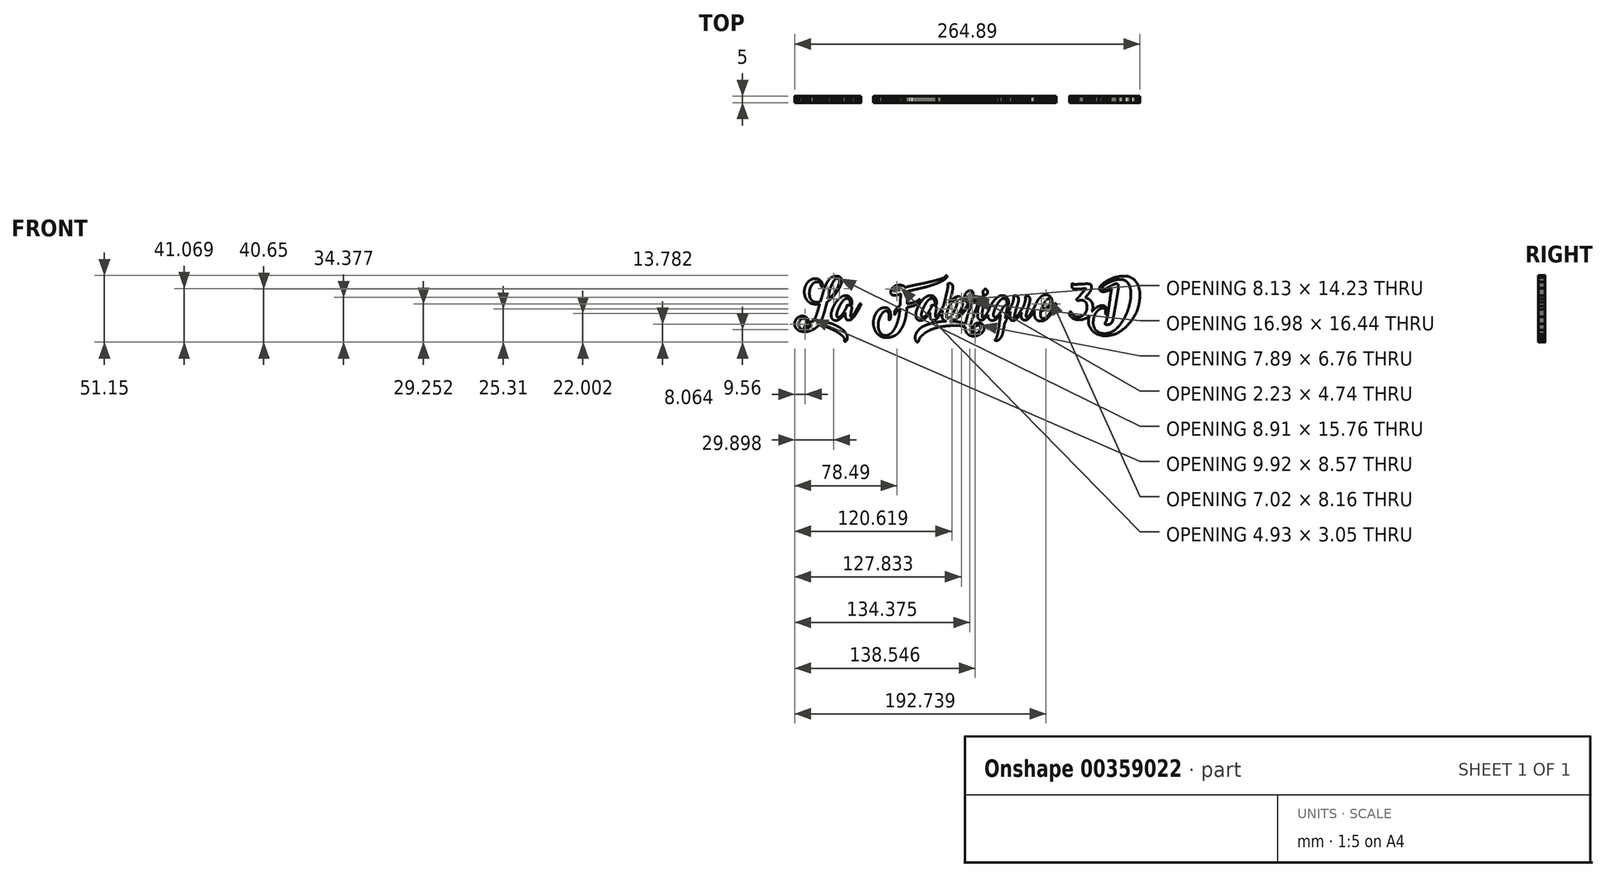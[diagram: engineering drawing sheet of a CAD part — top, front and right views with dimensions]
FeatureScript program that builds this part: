
annotation { "Feature Type Name" : "Feature", "Feature Type Description" : "" }
export const myFeature = defineFeature(function(context is Context, id is Id, definition is map)
    precondition{}
    {
        {
            var Q0;
            Q0=qCreatedBy(makeId("Front.planeOp"),FACE);
            var sketch = newSketch(context, id + "F0", { "sketchPlane" : qUnion([Q0])});
            skLineSegment(sketch, "E0", {"start": v(-112.6, 5.58) * mm, "end": v(-111.78, 8.4) * mm});
            skLineSegment(sketch, "E1", {"start": v(-107.62, 5.33) * mm, "end": v(-108.37, 2.37) * mm});
            skLineSegment(sketch, "E2", {"start": v(-126.72, -17.45) * mm, "end": v(-126.72, -17.45) * mm});
            skLineSegment(sketch, "E3", {"start": v(-106.57, 9.68) * mm, "end": v(-107, 7.62) * mm});
            skLineSegment(sketch, "E4", {"start": v(-125.15, -13.95) * mm, "end": v(-125.15, -13.93) * mm});
            skLineSegment(sketch, "E5", {"start": v(-81.47, 3.42) * mm, "end": v(-81.73, 2.87) * mm});
            skLineSegment(sketch, "E6", {"start": v(-88.86, 2.94) * mm, "end": v(-88.89, 2.92) * mm});
            skLineSegment(sketch, "E7", {"start": v(-19.52, 23.18) * mm, "end": v(-19.54, 23.18) * mm});
            skLineSegment(sketch, "E8", {"start": v(-16.3, 25.55) * mm, "end": v(-16.34, 25.55) * mm});
            skLineSegment(sketch, "E9", {"start": v(-40.07, 14.74) * mm, "end": v(-41.35, 14.43) * mm});
            skLineSegment(sketch, "E10", {"start": v(-45.54, 3.9) * mm, "end": v(-45.56, 3.9) * mm});
            skLineSegment(sketch, "E11", {"start": v(-44.8, 1.44) * mm, "end": v(-45.54, 1.31) * mm});
            skLineSegment(sketch, "E12", {"start": v(-46.28, 1.16) * mm, "end": v(-46.28, 0.6) * mm});
            skLineSegment(sketch, "E13", {"start": v(-46.3, 0.48) * mm, "end": v(-46.3, 0.38) * mm});
            skLineSegment(sketch, "E14", {"start": v(-46.3, 0.38) * mm, "end": v(-46.28, 0.38) * mm});
            skLineSegment(sketch, "E15", {"start": v(-61.75, -22.15) * mm, "end": v(-62.86, -22.15) * mm});
            skLineSegment(sketch, "E16", {"start": v(-58.98, -7.82) * mm, "end": v(-58.98, -7.8) * mm});
            skLineSegment(sketch, "E17", {"start": v(-60.11, -7.9) * mm, "end": v(-60.11, -6.28) * mm});
            skLineSegment(sketch, "E18", {"start": v(-51.67, -0.47) * mm, "end": v(-51.72, -0.45) * mm});
            skLineSegment(sketch, "E19", {"start": v(-51.72, -0.45) * mm, "end": v(-51.72, -0.45) * mm});
            skLineSegment(sketch, "E20", {"start": v(-53.83, 14.06) * mm, "end": v(-53.39, 14.18) * mm});
            skLineSegment(sketch, "E21", {"start": v(-51.52, 14.94) * mm, "end": v(-51.52, 14.96) * mm});
            skLineSegment(sketch, "E22", {"start": v(-23.91, 2.94) * mm, "end": v(-23.94, 2.92) * mm});
            skLineSegment(sketch, "E23", {"start": v(0.38, 3.72) * mm, "end": v(0.4, 3.75) * mm});
            skLineSegment(sketch, "E24", {"start": v(0.4, 3.75) * mm, "end": v(0.4, 3.75) * mm});
            skLineSegment(sketch, "E25", {"start": v(-14.71, 0.48) * mm, "end": v(-14.69, 0.5) * mm});
            skLineSegment(sketch, "E26", {"start": v(-14.69, 0.5) * mm, "end": v(-14.84, -0.1) * mm});
            skLineSegment(sketch, "E27", {"start": v(-9, 6.84) * mm, "end": v(-9, 6.84) * mm});
            skLineSegment(sketch, "E28", {"start": v(2.1, 4.65) * mm, "end": v(0.36, 1.1) * mm});
            skLineSegment(sketch, "E29", {"start": v(4.87, -20.97) * mm, "end": v(4.87, -20.97) * mm});
            skLineSegment(sketch, "E30", {"start": v(5.62, -17.67) * mm, "end": v(5.6, -17.65) * mm});
            skLineSegment(sketch, "E31", {"start": v(4.7, -18) * mm, "end": v(4.7, -17.97) * mm});
            skLineSegment(sketch, "E32", {"start": v(10.17, 6.56) * mm, "end": v(10.53, 7.72) * mm});
            skLineSegment(sketch, "E33", {"start": v(10.53, 7.72) * mm, "end": v(10.53, 7.7) * mm});
            skLineSegment(sketch, "E34", {"start": v(10.53, 7.7) * mm, "end": v(10.53, 7.7) * mm});
            skLineSegment(sketch, "E35", {"start": v(26.44, -1.03) * mm, "end": v(26.41, -1.03) * mm});
            skLineSegment(sketch, "E36", {"start": v(27.8, 1.46) * mm, "end": v(27.8, 1.44) * mm});
            skLineSegment(sketch, "E37", {"start": v(27.8, 1.44) * mm, "end": v(27.93, 1.71) * mm});
            skLineSegment(sketch, "E38", {"start": v(27.93, 1.71) * mm, "end": v(28.03, 1.71) * mm});
            skLineSegment(sketch, "E39", {"start": v(29.19, -7.29) * mm, "end": v(29.29, -7.04) * mm});
            skLineSegment(sketch, "E40", {"start": v(28.52, -11.59) * mm, "end": v(28.52, -11.56) * mm});
            skLineSegment(sketch, "E41", {"start": v(24, -15.66) * mm, "end": v(24.46, -12.22) * mm});
            skLineSegment(sketch, "E42", {"start": v(43.3, 2.14) * mm, "end": v(43.28, 2.11) * mm});
            skLineSegment(sketch, "E43", {"start": v(41.36, -5.43) * mm, "end": v(41.36, -4.7) * mm});
            skLineSegment(sketch, "E44", {"start": v(35.43, 9.18) * mm, "end": v(35.43, 9.15) * mm});
            skLineSegment(sketch, "E45", {"start": v(38.13, 9.7) * mm, "end": v(38.13, 9.7) * mm});
            skLineSegment(sketch, "E46", {"start": v(51.34, -1.5) * mm, "end": v(51.34, -1.53) * mm});
            skLineSegment(sketch, "E47", {"start": v(64.2, -1.8) * mm, "end": v(64.2, -1.83) * mm});
            skLineSegment(sketch, "E48", {"start": v(68.22, 3.42) * mm, "end": v(67.97, 2.87) * mm});
            skLineSegment(sketch, "E49", {"start": v(79.76, -2.84) * mm, "end": v(79.79, -2.84) * mm});
            skLineSegment(sketch, "E50", {"start": v(115.95, 16.04) * mm, "end": v(115.97, 16.04) * mm});
            skLineSegment(sketch, "E51", {"start": v(111.69, -8.77) * mm, "end": v(111.69, -8.75) * mm});
            skLineSegment(sketch, "E52", {"start": v(106.55, -12.24) * mm, "end": v(106.58, -12.24) * mm});
            skLineSegment(sketch, "E53", {"start": v(109.22, 5.6) * mm, "end": v(109.4, 6.97) * mm});
            skLineSegment(sketch, "E54", {"start": v(107.12, -3.77) * mm, "end": v(107.12, -3.74) * mm});
            skLineSegment(sketch, "E55", {"start": v(109.69, 17.25) * mm, "end": v(110.74, 17.85) * mm});
            skLineSegment(sketch, "E56", {"start": v(115.97, 16.07) * mm, "end": v(115.95, 16.04) * mm});
            skFitSpline(sketch, "E57", {"points": [v(-126.72, -17.45) * mm, v(-127.8, -17.21) * mm, v(-128.7, -16.88) * mm, v(-129.46, -16.47) * mm]});
            skFitSpline(sketch, "E58", {"points": [v(-129.46, -16.47) * mm, v(-130.2, -16.05) * mm, v(-130.8, -15.56) * mm, v(-131.26, -15) * mm]});
            skFitSpline(sketch, "E59", {"points": [v(-131.26, -15) * mm, v(-131.7, -14.47) * mm, v(-132.02, -13.9) * mm, v(-132.2, -13.27) * mm]});
            skFitSpline(sketch, "E60", {"points": [v(-132.2, -13.27) * mm, v(-132.38, -12.65) * mm, v(-132.45, -12.02) * mm, v(-132.41, -11.39) * mm]});
            skFitSpline(sketch, "E61", {"points": [v(-132.41, -11.39) * mm, v(-132.38, -10.7) * mm, v(-132.23, -10.03) * mm, v(-131.98, -9.38) * mm]});
            skFitSpline(sketch, "E62", {"points": [v(-131.98, -9.38) * mm, v(-131.7, -8.72) * mm, v(-131.34, -8.13) * mm, v(-130.9, -7.6) * mm]});
            skFitSpline(sketch, "E63", {"points": [v(-130.9, -7.6) * mm, v(-130.32, -6.95) * mm, v(-129.63, -6.47) * mm, v(-128.85, -6.13) * mm]});
            skFitSpline(sketch, "E64", {"points": [v(-128.85, -6.13) * mm, v(-128.04, -5.78) * mm, v(-127.25, -5.6) * mm, v(-126.48, -5.6) * mm]});
            skFitSpline(sketch, "E65", {"points": [v(-126.48, -5.6) * mm, v(-125.94, -5.6) * mm, v(-125.4, -5.69) * mm, v(-124.9, -5.86) * mm]});
            skFitSpline(sketch, "E66", {"points": [v(-124.9, -5.86) * mm, v(-124.38, -6) * mm, v(-123.93, -6.24) * mm, v(-123.53, -6.56) * mm]});
            skFitSpline(sketch, "E67", {"points": [v(-123.53, -6.56) * mm, v(-123.12, -6.88) * mm, v(-122.79, -7.28) * mm, v(-122.53, -7.77) * mm]});
            skFitSpline(sketch, "E68", {"points": [v(-122.53, -7.77) * mm, v(-122.28, -8.24) * mm, v(-122.12, -8.78) * mm, v(-122.07, -9.4) * mm]});
            skFitSpline(sketch, "E69", {"points": [v(-122.07, -9.4) * mm, v(-122.07, -10.04) * mm, v(-122.2, -10.62) * mm, v(-122.43, -11.16) * mm]});
            skFitSpline(sketch, "E70", {"points": [v(-122.43, -11.16) * mm, v(-121.81, -10.72) * mm, v(-121.13, -10.37) * mm, v(-120.38, -10.1) * mm]});
            skFitSpline(sketch, "E71", {"points": [v(-120.38, -10.1) * mm, v(-119.6, -9.85) * mm, v(-118.76, -9.66) * mm, v(-117.84, -9.53) * mm]});
            skFitSpline(sketch, "E72", {"points": [v(-117.84, -9.53) * mm, v(-117.32, -8.55) * mm, v(-116.85, -7.5) * mm, v(-116.43, -6.38) * mm]});
            skFitSpline(sketch, "E73", {"points": [v(-116.43, -6.38) * mm, v(-115.98, -5.26) * mm, v(-115.58, -4.14) * mm, v(-115.22, -3.01) * mm]});
            skFitSpline(sketch, "E74", {"points": [v(-115.22, -3.01) * mm, v(-114.84, -1.87) * mm, v(-114.5, -0.77) * mm, v(-114.22, 0.3) * mm]});
            skFitSpline(sketch, "E75", {"points": [v(-114.22, 0.3) * mm, v(-113.91, 1.4) * mm, v(-113.64, 2.38) * mm, v(-113.4, 3.27) * mm]});
            skFitSpline(sketch, "E76", {"points": [v(-113.4, 3.27) * mm, v(-113.36, 3.35) * mm, v(-113.34, 3.44) * mm, v(-113.32, 3.52) * mm]});
            skFitSpline(sketch, "E77", {"points": [v(-113.32, 3.52) * mm, v(-113.29, 3.6) * mm, v(-113.26, 3.69) * mm, v(-113.24, 3.77) * mm]});
            skFitSpline(sketch, "E78", {"points": [v(-113.24, 3.77) * mm, v(-113.65, 3.64) * mm, v(-114.06, 3.55) * mm, v(-114.45, 3.5) * mm]});
            skFitSpline(sketch, "E79", {"points": [v(-114.45, 3.5) * mm, v(-114.84, 3.45) * mm, v(-115.25, 3.42) * mm, v(-115.66, 3.42) * mm]});
            skFitSpline(sketch, "E80", {"points": [v(-115.66, 3.42) * mm, v(-116.12, 3.42) * mm, v(-116.57, 3.45) * mm, v(-117.02, 3.5) * mm]});
            skFitSpline(sketch, "E81", {"points": [v(-117.02, 3.5) * mm, v(-117.46, 3.56) * mm, v(-117.89, 3.64) * mm, v(-118.3, 3.72) * mm]});
            skFitSpline(sketch, "E82", {"points": [v(-118.3, 3.72) * mm, v(-119.51, 4) * mm, v(-120.56, 4.45) * mm, v(-121.43, 5.1) * mm]});
            skFitSpline(sketch, "E83", {"points": [v(-121.43, 5.1) * mm, v(-122.28, 5.78) * mm, v(-122.99, 6.56) * mm, v(-123.53, 7.44) * mm]});
            skFitSpline(sketch, "E84", {"points": [v(-123.53, 7.44) * mm, v(-124.08, 8.33) * mm, v(-124.47, 9.3) * mm, v(-124.71, 10.36) * mm]});
            skFitSpline(sketch, "E85", {"points": [v(-124.71, 10.36) * mm, v(-124.95, 11.42) * mm, v(-125.05, 12.49) * mm, v(-125, 13.58) * mm]});
            skFitSpline(sketch, "E86", {"points": [v(-125, 13.58) * mm, v(-124.94, 14.69) * mm, v(-124.74, 15.77) * mm, v(-124.38, 16.82) * mm]});
            skFitSpline(sketch, "E87", {"points": [v(-124.38, 16.82) * mm, v(-124, 17.88) * mm, v(-123.5, 18.83) * mm, v(-122.87, 19.69) * mm]});
            skFitSpline(sketch, "E88", {"points": [v(-122.87, 19.69) * mm, v(-122.23, 20.56) * mm, v(-121.47, 21.29) * mm, v(-120.58, 21.88) * mm]});
            skFitSpline(sketch, "E89", {"points": [v(-120.58, 21.88) * mm, v(-119.7, 22.46) * mm, v(-118.7, 22.85) * mm, v(-117.58, 23.03) * mm]});
            skFitSpline(sketch, "E90", {"points": [v(-117.58, 23.03) * mm, v(-117.44, 23.07) * mm, v(-117.29, 23.08) * mm, v(-117.12, 23.08) * mm]});
            skFitSpline(sketch, "E91", {"points": [v(-117.12, 23.08) * mm, v(-116.93, 23.1) * mm, v(-116.77, 23.1) * mm, v(-116.63, 23.1) * mm]});
            skFitSpline(sketch, "E92", {"points": [v(-116.63, 23.1) * mm, v(-115.7, 23.1) * mm, v(-114.89, 22.92) * mm, v(-114.17, 22.56) * mm]});
            skFitSpline(sketch, "E93", {"points": [v(-114.17, 22.56) * mm, v(-113.43, 22.2) * mm, v(-112.82, 21.75) * mm, v(-112.35, 21.2) * mm]});
            skFitSpline(sketch, "E94", {"points": [v(-112.35, 21.2) * mm, v(-111.85, 20.64) * mm, v(-111.5, 20.04) * mm, v(-111.27, 19.39) * mm]});
            skFitSpline(sketch, "E95", {"points": [v(-111.27, 19.39) * mm, v(-111.05, 18.73) * mm, v(-110.99, 18.12) * mm, v(-111.09, 17.55) * mm]});
            skFitSpline(sketch, "E96", {"points": [v(-111.09, 17.55) * mm, v(-111.28, 17.15) * mm, v(-111.46, 16.95) * mm, v(-111.63, 16.95) * mm]});
            skFitSpline(sketch, "E97", {"points": [v(-111.63, 16.95) * mm, v(-111.8, 16.97) * mm, v(-111.96, 17.05) * mm, v(-112.11, 17.2) * mm]});
            skFitSpline(sketch, "E98", {"points": [v(-112.11, 17.2) * mm, v(-112.13, 17.79) * mm, v(-112.22, 18.28) * mm, v(-112.37, 18.68) * mm]});
            skFitSpline(sketch, "E99", {"points": [v(-112.37, 18.68) * mm, v(-112.5, 19.09) * mm, v(-112.69, 19.41) * mm, v(-112.91, 19.66) * mm]});
            skFitSpline(sketch, "E100", {"points": [v(-112.91, 19.66) * mm, v(-113.12, 19.93) * mm, v(-113.34, 20.12) * mm, v(-113.58, 20.24) * mm]});
            skFitSpline(sketch, "E101", {"points": [v(-113.58, 20.24) * mm, v(-113.8, 20.38) * mm, v(-114.01, 20.47) * mm, v(-114.22, 20.52) * mm]});
            skFitSpline(sketch, "E102", {"points": [v(-114.22, 20.52) * mm, v(-114.5, 20.57) * mm, v(-114.8, 20.6) * mm, v(-115.1, 20.6) * mm]});
            skFitSpline(sketch, "E103", {"points": [v(-115.1, 20.6) * mm, v(-116, 20.6) * mm, v(-116.82, 20.35) * mm, v(-117.55, 19.87) * mm]});
            skFitSpline(sketch, "E104", {"points": [v(-117.55, 19.87) * mm, v(-118.27, 19.4) * mm, v(-118.89, 18.78) * mm, v(-119.4, 18) * mm]});
            skFitSpline(sketch, "E105", {"points": [v(-119.4, 18) * mm, v(-119.92, 17.25) * mm, v(-120.33, 16.39) * mm, v(-120.63, 15.41) * mm]});
            skFitSpline(sketch, "E106", {"points": [v(-120.63, 15.41) * mm, v(-120.92, 14.44) * mm, v(-121.1, 13.46) * mm, v(-121.15, 12.47) * mm]});
            skFitSpline(sketch, "E107", {"points": [v(-121.15, 12.47) * mm, v(-121.18, 11.82) * mm, v(-121.16, 11.17) * mm, v(-121.1, 10.54) * mm]});
            skFitSpline(sketch, "E108", {"points": [v(-121.1, 10.54) * mm, v(-121.01, 9.9) * mm, v(-120.87, 9.3) * mm, v(-120.69, 8.73) * mm]});
            skFitSpline(sketch, "E109", {"points": [v(-120.69, 8.73) * mm, v(-120.48, 8.16) * mm, v(-120.22, 7.64) * mm, v(-119.92, 7.17) * mm]});
            skFitSpline(sketch, "E110", {"points": [v(-119.92, 7.17) * mm, v(-119.6, 6.7) * mm, v(-119.24, 6.31) * mm, v(-118.81, 6.01) * mm]});
            skFitSpline(sketch, "E111", {"points": [v(-118.81, 6.01) * mm, v(-118.35, 5.68) * mm, v(-117.84, 5.4) * mm, v(-117.27, 5.2) * mm]});
            skFitSpline(sketch, "E112", {"points": [v(-117.27, 5.2) * mm, v(-116.7, 5.02) * mm, v(-116.1, 4.93) * mm, v(-115.48, 4.93) * mm]});
            skFitSpline(sketch, "E113", {"points": [v(-115.48, 4.93) * mm, v(-115.05, 4.93) * mm, v(-114.59, 4.99) * mm, v(-114.1, 5.1) * mm]});
            skFitSpline(sketch, "E114", {"points": [v(-114.1, 5.1) * mm, v(-113.58, 5.24) * mm, v(-113.08, 5.4) * mm, v(-112.6, 5.58) * mm]});
            skFitSpline(sketch, "E115", {"points": [v(-111.78, 8.4) * mm, v(-111.35, 9.98) * mm, v(-110.9, 11.56) * mm, v(-110.42, 13.15) * mm]});
            skFitSpline(sketch, "E116", {"points": [v(-110.42, 13.15) * mm, v(-109.94, 14.74) * mm, v(-109.41, 16.24) * mm, v(-108.83, 17.63) * mm]});
            skFitSpline(sketch, "E117", {"points": [v(-108.83, 17.63) * mm, v(-108.25, 19.04) * mm, v(-107.6, 20.28) * mm, v(-106.88, 21.37) * mm]});
            skFitSpline(sketch, "E118", {"points": [v(-106.88, 21.37) * mm, v(-106.16, 22.46) * mm, v(-105.34, 23.3) * mm, v(-104.42, 23.91) * mm]});
            skFitSpline(sketch, "E119", {"points": [v(-104.42, 23.91) * mm, v(-103.83, 24.25) * mm, v(-103.18, 24.52) * mm, v(-102.47, 24.72) * mm]});
            skFitSpline(sketch, "E120", {"points": [v(-102.47, 24.72) * mm, v(-101.75, 24.94) * mm, v(-101.04, 25.04) * mm, v(-100.34, 25.04) * mm]});
            skFitSpline(sketch, "E121", {"points": [v(-100.34, 25.04) * mm, v(-99.5, 25.04) * mm, v(-98.74, 24.86) * mm, v(-98.05, 24.5) * mm]});
            skFitSpline(sketch, "E122", {"points": [v(-98.05, 24.5) * mm, v(-97.37, 24.12) * mm, v(-96.9, 23.51) * mm, v(-96.67, 22.66) * mm]});
            skFitSpline(sketch, "E123", {"points": [v(-96.67, 22.66) * mm, v(-96.55, 22.19) * mm, v(-96.5, 21.67) * mm, v(-96.51, 21.1) * mm]});
            skFitSpline(sketch, "E124", {"points": [v(-96.51, 21.1) * mm, v(-96.56, 20.28) * mm, v(-96.77, 19.37) * mm, v(-97.13, 18.38) * mm]});
            skFitSpline(sketch, "E125", {"points": [v(-97.13, 18.38) * mm, v(-97.49, 17.4) * mm, v(-97.96, 16.38) * mm, v(-98.54, 15.34) * mm]});
            skFitSpline(sketch, "E126", {"points": [v(-98.54, 15.34) * mm, v(-99.12, 14.3) * mm, v(-99.79, 13.27) * mm, v(-100.54, 12.25) * mm]});
            skFitSpline(sketch, "E127", {"points": [v(-100.54, 12.25) * mm, v(-101.28, 11.22) * mm, v(-102.06, 10.26) * mm, v(-102.88, 9.36) * mm]});
            skFitSpline(sketch, "E128", {"points": [v(-102.88, 9.36) * mm, v(-103.68, 8.47) * mm, v(-104.5, 7.67) * mm, v(-105.31, 6.97) * mm]});
            skFitSpline(sketch, "E129", {"points": [v(-105.31, 6.97) * mm, v(-106.14, 6.26) * mm, v(-106.9, 5.72) * mm, v(-107.62, 5.33) * mm]});
            skFitSpline(sketch, "E130", {"points": [v(-108.37, 2.37) * mm, v(-108.6, 1.48) * mm, v(-108.86, 0.54) * mm, v(-109.11, -0.45) * mm]});
            skFitSpline(sketch, "E131", {"points": [v(-109.11, -0.45) * mm, v(-109.37, -1.44) * mm, v(-109.65, -2.44) * mm, v(-109.96, -3.47) * mm]});
            skFitSpline(sketch, "E132", {"points": [v(-109.96, -3.47) * mm, v(-110.27, -4.47) * mm, v(-110.6, -5.49) * mm, v(-110.99, -6.5) * mm]});
            skFitSpline(sketch, "E133", {"points": [v(-110.99, -6.5) * mm, v(-111.36, -7.53) * mm, v(-111.79, -8.52) * mm, v(-112.27, -9.48) * mm]});
            skFitSpline(sketch, "E134", {"points": [v(-112.27, -9.48) * mm, v(-111.12, -9.56) * mm, v(-110.02, -9.74) * mm, v(-108.96, -10) * mm]});
            skFitSpline(sketch, "E135", {"points": [v(-108.96, -10) * mm, v(-107.88, -10.27) * mm, v(-106.77, -10.58) * mm, v(-105.62, -10.93) * mm]});
            skFitSpline(sketch, "E136", {"points": [v(-105.62, -10.93) * mm, v(-103.8, -11.5) * mm, v(-102.07, -12.2) * mm, v(-100.41, -13.05) * mm]});
            skFitSpline(sketch, "E137", {"points": [v(-100.41, -13.05) * mm, v(-98.75, -13.88) * mm, v(-97.3, -14.8) * mm, v(-96.05, -15.81) * mm]});
            skFitSpline(sketch, "E138", {"points": [v(-96.05, -15.81) * mm, v(-94.79, -16.82) * mm, v(-93.8, -17.9) * mm, v(-93.07, -19.03) * mm]});
            skFitSpline(sketch, "E139", {"points": [v(-93.07, -19.03) * mm, v(-92.34, -20.17) * mm, v(-92, -21.33) * mm, v(-92.07, -22.52) * mm]});
            skFitSpline(sketch, "E140", {"points": [v(-92.07, -22.52) * mm, v(-92.1, -22.68) * mm, v(-92.1, -22.84) * mm, v(-92.13, -23) * mm]});
            skFitSpline(sketch, "E141", {"points": [v(-92.13, -23) * mm, v(-92.14, -23.19) * mm, v(-92.17, -23.35) * mm, v(-92.2, -23.48) * mm]});
            skFitSpline(sketch, "E142", {"points": [v(-92.2, -23.48) * mm, v(-92.24, -23.61) * mm, v(-92.31, -23.78) * mm, v(-92.43, -23.98) * mm]});
            skFitSpline(sketch, "E143", {"points": [v(-92.43, -23.98) * mm, v(-92.55, -24.18) * mm, v(-92.7, -24.38) * mm, v(-92.87, -24.56) * mm]});
            skFitSpline(sketch, "E144", {"points": [v(-92.87, -24.56) * mm, v(-93.04, -24.76) * mm, v(-93.22, -24.92) * mm, v(-93.4, -25.04) * mm]});
            skFitSpline(sketch, "E145", {"points": [v(-93.4, -25.04) * mm, v(-93.6, -25.17) * mm, v(-93.76, -25.22) * mm, v(-93.9, -25.2) * mm]});
            skFitSpline(sketch, "E146", {"points": [v(-93.9, -25.2) * mm, v(-94.02, -25.16) * mm, v(-94.1, -25.09) * mm, v(-94.15, -24.99) * mm]});
            skFitSpline(sketch, "E147", {"points": [v(-94.15, -24.99) * mm, v(-94.2, -24.89) * mm, v(-94.24, -24.78) * mm, v(-94.26, -24.66) * mm]});
            skFitSpline(sketch, "E148", {"points": [v(-94.26, -24.66) * mm, v(-94.26, -24.54) * mm, v(-94.25, -24.43) * mm, v(-94.23, -24.31) * mm]});
            skFitSpline(sketch, "E149", {"points": [v(-94.23, -24.31) * mm, v(-94.21, -24.2) * mm, v(-94.19, -24.1) * mm, v(-94.15, -24.03) * mm]});
            skFitSpline(sketch, "E150", {"points": [v(-94.15, -24.03) * mm, v(-94.12, -23.45) * mm, v(-94.29, -22.85) * mm, v(-94.67, -22.25) * mm]});
            skFitSpline(sketch, "E151", {"points": [v(-94.67, -22.25) * mm, v(-95.04, -21.66) * mm, v(-95.56, -21.07) * mm, v(-96.2, -20.46) * mm]});
            skFitSpline(sketch, "E152", {"points": [v(-96.2, -20.46) * mm, v(-96.84, -19.88) * mm, v(-97.58, -19.3) * mm, v(-98.44, -18.73) * mm]});
            skFitSpline(sketch, "E153", {"points": [v(-98.44, -18.73) * mm, v(-99.3, -18.18) * mm, v(-100.18, -17.64) * mm, v(-101.1, -17.12) * mm]});
            skFitSpline(sketch, "E154", {"points": [v(-101.1, -17.12) * mm, v(-102.03, -16.62) * mm, v(-102.96, -16.14) * mm, v(-103.9, -15.69) * mm]});
            skFitSpline(sketch, "E155", {"points": [v(-103.9, -15.69) * mm, v(-104.84, -15.25) * mm, v(-105.73, -14.86) * mm, v(-106.55, -14.5) * mm]});
            skFitSpline(sketch, "E156", {"points": [v(-106.55, -14.5) * mm, v(-107.37, -14.17) * mm, v(-108.1, -13.88) * mm, v(-108.75, -13.65) * mm]});
            skFitSpline(sketch, "E157", {"points": [v(-108.75, -13.65) * mm, v(-109.39, -13.42) * mm, v(-109.87, -13.26) * mm, v(-110.2, -13.17) * mm]});
            skFitSpline(sketch, "E158", {"points": [v(-110.2, -13.17) * mm, v(-110.52, -13.05) * mm, v(-110.8, -12.96) * mm, v(-111.04, -12.9) * mm]});
            skFitSpline(sketch, "E159", {"points": [v(-111.04, -12.9) * mm, v(-111.28, -12.83) * mm, v(-111.5, -12.77) * mm, v(-111.7, -12.72) * mm]});
            skFitSpline(sketch, "E160", {"points": [v(-111.7, -12.72) * mm, v(-111.9, -12.69) * mm, v(-112.1, -12.65) * mm, v(-112.3, -12.62) * mm]});
            skFitSpline(sketch, "E161", {"points": [v(-112.3, -12.62) * mm, v(-112.48, -12.6) * mm, v(-112.69, -12.58) * mm, v(-112.91, -12.54) * mm]});
            skFitSpline(sketch, "E162", {"points": [v(-112.91, -12.54) * mm, v(-113.06, -12.5) * mm, v(-113.23, -12.48) * mm, v(-113.4, -12.47) * mm]});
            skFitSpline(sketch, "E163", {"points": [v(-113.4, -12.47) * mm, v(-113.55, -12.45) * mm, v(-113.73, -12.43) * mm, v(-113.94, -12.4) * mm]});
            skFitSpline(sketch, "E164", {"points": [v(-113.94, -12.4) * mm, v(-114.57, -13.16) * mm, v(-115.3, -13.87) * mm, v(-116.14, -14.5) * mm]});
            skFitSpline(sketch, "E165", {"points": [v(-116.14, -14.5) * mm, v(-116.98, -15.14) * mm, v(-117.88, -15.69) * mm, v(-118.84, -16.14) * mm]});
            skFitSpline(sketch, "E166", {"points": [v(-118.84, -16.14) * mm, v(-119.78, -16.6) * mm, v(-120.75, -16.97) * mm, v(-121.76, -17.22) * mm]});
            skFitSpline(sketch, "E167", {"points": [v(-121.76, -17.22) * mm, v(-122.76, -17.49) * mm, v(-123.74, -17.62) * mm, v(-124.71, -17.62) * mm]});
            skFitSpline(sketch, "E168", {"points": [v(-124.71, -17.62) * mm, v(-125.06, -17.62) * mm, v(-125.4, -17.6) * mm, v(-125.74, -17.57) * mm]});
            skFitSpline(sketch, "E169", {"points": [v(-125.74, -17.57) * mm, v(-126.07, -17.56) * mm, v(-126.4, -17.51) * mm, v(-126.72, -17.45) * mm]});
            skFitSpline(sketch, "E170", {"points": [v(-107, 7.62) * mm, v(-106.5, 7.84) * mm, v(-105.93, 8.2) * mm, v(-105.31, 8.73) * mm]});
            skFitSpline(sketch, "E171", {"points": [v(-105.31, 8.73) * mm, v(-104.68, 9.26) * mm, v(-104.05, 9.9) * mm, v(-103.42, 10.61) * mm]});
            skFitSpline(sketch, "E172", {"points": [v(-103.42, 10.61) * mm, v(-102.77, 11.35) * mm, v(-102.13, 12.15) * mm, v(-101.52, 13.03) * mm]});
            skFitSpline(sketch, "E173", {"points": [v(-101.52, 13.03) * mm, v(-100.9, 13.9) * mm, v(-100.35, 14.79) * mm, v(-99.87, 15.7) * mm]});
            skFitSpline(sketch, "E174", {"points": [v(-99.87, 15.7) * mm, v(-99.38, 16.6) * mm, v(-98.98, 17.48) * mm, v(-98.67, 18.36) * mm]});
            skFitSpline(sketch, "E175", {"points": [v(-98.67, 18.36) * mm, v(-98.34, 19.24) * mm, v(-98.16, 20.07) * mm, v(-98.13, 20.82) * mm]});
            skFitSpline(sketch, "E176", {"points": [v(-98.13, 20.82) * mm, v(-98.1, 21.37) * mm, v(-98.15, 21.85) * mm, v(-98.28, 22.25) * mm]});
            skFitSpline(sketch, "E177", {"points": [v(-98.28, 22.25) * mm, v(-98.42, 22.66) * mm, v(-98.63, 22.95) * mm, v(-98.9, 23.13) * mm]});
            skFitSpline(sketch, "E178", {"points": [v(-98.9, 23.13) * mm, v(-99.16, 23.32) * mm, v(-99.48, 23.38) * mm, v(-99.87, 23.3) * mm]});
            skFitSpline(sketch, "E179", {"points": [v(-99.87, 23.3) * mm, v(-100.25, 23.24) * mm, v(-100.67, 23.02) * mm, v(-101.13, 22.63) * mm]});
            skFitSpline(sketch, "E180", {"points": [v(-101.13, 22.63) * mm, v(-101.97, 21.9) * mm, v(-102.69, 21.01) * mm, v(-103.29, 19.94) * mm]});
            skFitSpline(sketch, "E181", {"points": [v(-103.29, 19.94) * mm, v(-103.87, 18.87) * mm, v(-104.37, 17.73) * mm, v(-104.8, 16.52) * mm]});
            skFitSpline(sketch, "E182", {"points": [v(-104.8, 16.52) * mm, v(-105.23, 15.33) * mm, v(-105.58, 14.13) * mm, v(-105.85, 12.93) * mm]});
            skFitSpline(sketch, "E183", {"points": [v(-105.85, 12.93) * mm, v(-106.13, 11.72) * mm, v(-106.37, 10.64) * mm, v(-106.57, 9.68) * mm]});
            skFitSpline(sketch, "E184", {"points": [v(-125.15, -13.93) * mm, v(-124.94, -13.67) * mm, v(-124.74, -13.4) * mm, v(-124.53, -13.1) * mm]});
            skFitSpline(sketch, "E185", {"points": [v(-124.53, -13.1) * mm, v(-124.33, -12.8) * mm, v(-124.14, -12.48) * mm, v(-123.97, -12.14) * mm]});
            skFitSpline(sketch, "E186", {"points": [v(-123.97, -12.14) * mm, v(-123.8, -11.82) * mm, v(-123.66, -11.5) * mm, v(-123.56, -11.16) * mm]});
            skFitSpline(sketch, "E187", {"points": [v(-123.56, -11.16) * mm, v(-123.44, -10.83) * mm, v(-123.37, -10.5) * mm, v(-123.35, -10.16) * mm]});
            skFitSpline(sketch, "E188", {"points": [v(-123.35, -10.16) * mm, v(-123.34, -9.9) * mm, v(-123.35, -9.64) * mm, v(-123.4, -9.35) * mm]});
            skFitSpline(sketch, "E189", {"points": [v(-123.4, -9.35) * mm, v(-123.56, -8.73) * mm, v(-123.88, -8.27) * mm, v(-124.35, -7.97) * mm]});
            skFitSpline(sketch, "E190", {"points": [v(-124.35, -7.97) * mm, v(-124.82, -7.67) * mm, v(-125.32, -7.52) * mm, v(-125.87, -7.52) * mm]});
            skFitSpline(sketch, "E191", {"points": [v(-125.87, -7.52) * mm, v(-126.3, -7.52) * mm, v(-126.72, -7.6) * mm, v(-127.15, -7.8) * mm]});
            skFitSpline(sketch, "E192", {"points": [v(-127.15, -7.8) * mm, v(-127.56, -7.98) * mm, v(-127.91, -8.24) * mm, v(-128.2, -8.57) * mm]});
            skFitSpline(sketch, "E193", {"points": [v(-128.2, -8.57) * mm, v(-128.55, -8.96) * mm, v(-128.81, -9.4) * mm, v(-129, -9.9) * mm]});
            skFitSpline(sketch, "E194", {"points": [v(-129, -9.9) * mm, v(-129.17, -10.42) * mm, v(-129.27, -10.94) * mm, v(-129.3, -11.46) * mm]});
            skFitSpline(sketch, "E195", {"points": [v(-129.3, -11.46) * mm, v(-129.34, -12.23) * mm, v(-129.22, -12.98) * mm, v(-128.95, -13.7) * mm]});
            skFitSpline(sketch, "E196", {"points": [v(-128.95, -13.7) * mm, v(-128.67, -14.42) * mm, v(-128.21, -14.97) * mm, v(-127.56, -15.36) * mm]});
            skFitSpline(sketch, "E197", {"points": [v(-127.56, -15.36) * mm, v(-127.17, -15.61) * mm, v(-126.78, -15.79) * mm, v(-126.4, -15.89) * mm]});
            skFitSpline(sketch, "E198", {"points": [v(-126.4, -15.89) * mm, v(-126.01, -16) * mm, v(-125.64, -16.06) * mm, v(-125.28, -16.06) * mm]});
            skFitSpline(sketch, "E199", {"points": [v(-125.28, -16.06) * mm, v(-124.7, -16.06) * mm, v(-124.13, -15.95) * mm, v(-123.58, -15.71) * mm]});
            skFitSpline(sketch, "E200", {"points": [v(-123.58, -15.71) * mm, v(-123.04, -15.48) * mm, v(-122.52, -15.17) * mm, v(-122.02, -14.78) * mm]});
            skFitSpline(sketch, "E201", {"points": [v(-122.02, -14.78) * mm, v(-121.52, -14.41) * mm, v(-121.06, -14) * mm, v(-120.63, -13.52) * mm]});
            skFitSpline(sketch, "E202", {"points": [v(-120.63, -13.52) * mm, v(-120.19, -13.07) * mm, v(-119.79, -12.61) * mm, v(-119.43, -12.14) * mm]});
            skFitSpline(sketch, "E203", {"points": [v(-119.43, -12.14) * mm, v(-120.44, -12.24) * mm, v(-121.33, -12.48) * mm, v(-122.1, -12.85) * mm]});
            skFitSpline(sketch, "E204", {"points": [v(-122.1, -12.85) * mm, v(-122.87, -13.21) * mm, v(-123.45, -13.73) * mm, v(-123.84, -14.4) * mm]});
            skFitSpline(sketch, "E205", {"points": [v(-123.84, -14.4) * mm, v(-123.98, -14.52) * mm, v(-124.12, -14.59) * mm, v(-124.28, -14.6) * mm]});
            skFitSpline(sketch, "E206", {"points": [v(-124.28, -14.6) * mm, v(-124.43, -14.64) * mm, v(-124.58, -14.63) * mm, v(-124.71, -14.58) * mm]});
            skFitSpline(sketch, "E207", {"points": [v(-124.71, -14.58) * mm, v(-124.85, -14.55) * mm, v(-124.96, -14.47) * mm, v(-125.05, -14.35) * mm]});
            skFitSpline(sketch, "E208", {"points": [v(-125.05, -14.35) * mm, v(-125.13, -14.25) * mm, v(-125.17, -14.12) * mm, v(-125.15, -13.95) * mm]});
            skFitSpline(sketch, "E209", {"points": [v(-88.89, 2.92) * mm, v(-88.92, 2.87) * mm, v(-89.03, 2.82) * mm, v(-89.2, 2.77) * mm]});
            skFitSpline(sketch, "E210", {"points": [v(-89.2, 2.77) * mm, v(-89.35, 2.72) * mm, v(-89.46, 2.7) * mm, v(-89.53, 2.7) * mm]});
            skFitSpline(sketch, "E211", {"points": [v(-89.53, 2.7) * mm, v(-89.74, 2.7) * mm, v(-89.92, 2.8) * mm, v(-90.07, 3) * mm]});
            skFitSpline(sketch, "E212", {"points": [v(-90.07, 3) * mm, v(-90, 3.18) * mm, v(-89.96, 3.35) * mm, v(-89.94, 3.5) * mm]});
            skFitSpline(sketch, "E213", {"points": [v(-89.94, 3.5) * mm, v(-89.9, 3.66) * mm, v(-89.87, 3.84) * mm, v(-89.84, 4.03) * mm]});
            skFitSpline(sketch, "E214", {"points": [v(-89.84, 4.03) * mm, v(-89.82, 4.44) * mm, v(-89.86, 4.88) * mm, v(-89.94, 5.33) * mm]});
            skFitSpline(sketch, "E215", {"points": [v(-89.94, 5.33) * mm, v(-90, 5.8) * mm, v(-90.15, 6.22) * mm, v(-90.35, 6.59) * mm]});
            skFitSpline(sketch, "E216", {"points": [v(-90.35, 6.59) * mm, v(-90.56, 6.96) * mm, v(-90.82, 7.26) * mm, v(-91.15, 7.5) * mm]});
            skFitSpline(sketch, "E217", {"points": [v(-91.15, 7.5) * mm, v(-91.47, 7.75) * mm, v(-91.87, 7.87) * mm, v(-92.33, 7.87) * mm]});
            skFitSpline(sketch, "E218", {"points": [v(-92.33, 7.87) * mm, v(-92.93, 7.87) * mm, v(-93.53, 7.64) * mm, v(-94.15, 7.17) * mm]});
            skFitSpline(sketch, "E219", {"points": [v(-94.15, 7.17) * mm, v(-94.77, 6.72) * mm, v(-95.36, 6.12) * mm, v(-95.92, 5.38) * mm]});
            skFitSpline(sketch, "E220", {"points": [v(-95.92, 5.38) * mm, v(-96.48, 4.66) * mm, v(-97.02, 3.85) * mm, v(-97.51, 2.94) * mm]});
            skFitSpline(sketch, "E221", {"points": [v(-97.51, 2.94) * mm, v(-98, 2.04) * mm, v(-98.45, 1.13) * mm, v(-98.85, 0.23) * mm]});
            skFitSpline(sketch, "E222", {"points": [v(-98.85, 0.23) * mm, v(-99.22, -0.66) * mm, v(-99.53, -1.5) * mm, v(-99.77, -2.29) * mm]});
            skFitSpline(sketch, "E223", {"points": [v(-99.77, -2.29) * mm, v(-100, -3.07) * mm, v(-100.15, -3.71) * mm, v(-100.18, -4.2) * mm]});
            skFitSpline(sketch, "E224", {"points": [v(-100.18, -4.2) * mm, v(-100.2, -4.43) * mm, v(-100.2, -4.68) * mm, v(-100.2, -4.95) * mm]});
            skFitSpline(sketch, "E225", {"points": [v(-100.2, -4.95) * mm, v(-100.19, -5.22) * mm, v(-100.14, -5.47) * mm, v(-100.05, -5.7) * mm]});
            skFitSpline(sketch, "E226", {"points": [v(-100.05, -5.7) * mm, v(-99.97, -5.92) * mm, v(-99.84, -6.1) * mm, v(-99.67, -6.26) * mm]});
            skFitSpline(sketch, "E227", {"points": [v(-99.67, -6.26) * mm, v(-99.5, -6.4) * mm, v(-99.26, -6.46) * mm, v(-98.95, -6.46) * mm]});
            skFitSpline(sketch, "E228", {"points": [v(-98.95, -6.46) * mm, v(-98.42, -6.46) * mm, v(-97.86, -6.2) * mm, v(-97.28, -5.68) * mm]});
            skFitSpline(sketch, "E229", {"points": [v(-97.28, -5.68) * mm, v(-96.68, -5.14) * mm, v(-96.1, -4.5) * mm, v(-95.56, -3.74) * mm]});
            skFitSpline(sketch, "E230", {"points": [v(-95.56, -3.74) * mm, v(-95, -2.99) * mm, v(-94.47, -2.2) * mm, v(-94, -1.38) * mm]});
            skFitSpline(sketch, "E231", {"points": [v(-94, -1.38) * mm, v(-93.52, -0.54) * mm, v(-93.11, 0.19) * mm, v(-92.79, 0.8) * mm]});
            skFitSpline(sketch, "E232", {"points": [v(-92.79, 0.8) * mm, v(-92.74, 1) * mm, v(-92.66, 1.2) * mm, v(-92.56, 1.46) * mm]});
            skFitSpline(sketch, "E233", {"points": [v(-92.56, 1.46) * mm, v(-92.44, 1.71) * mm, v(-92.4, 1.99) * mm, v(-92.43, 2.3) * mm]});
            skFitSpline(sketch, "E234", {"points": [v(-92.43, 2.3) * mm, v(-92.46, 2.53) * mm, v(-92.37, 2.68) * mm, v(-92.15, 2.74) * mm]});
            skFitSpline(sketch, "E235", {"points": [v(-92.15, 2.74) * mm, v(-91.93, 2.83) * mm, v(-91.69, 2.88) * mm, v(-91.43, 2.9) * mm]});
            skFitSpline(sketch, "E236", {"points": [v(-91.43, 2.9) * mm, v(-90.42, 2.8) * mm, v(-89.72, 2.58) * mm, v(-89.33, 2.19) * mm]});
            skFitSpline(sketch, "E237", {"points": [v(-89.33, 2.19) * mm, v(-88.92, 1.82) * mm, v(-88.68, 1.38) * mm, v(-88.63, 0.86) * mm]});
            skFitSpline(sketch, "E238", {"points": [v(-88.63, 0.86) * mm, v(-88.58, 0.32) * mm, v(-88.64, -0.26) * mm, v(-88.81, -0.88) * mm]});
            skFitSpline(sketch, "E239", {"points": [v(-88.81, -0.88) * mm, v(-88.97, -1.5) * mm, v(-89.09, -2.08) * mm, v(-89.17, -2.61) * mm]});
            skFitSpline(sketch, "E240", {"points": [v(-89.17, -2.61) * mm, v(-89.19, -2.73) * mm, v(-89.22, -2.92) * mm, v(-89.27, -3.2) * mm]});
            skFitSpline(sketch, "E241", {"points": [v(-89.27, -3.2) * mm, v(-89.3, -3.46) * mm, v(-89.34, -3.75) * mm, v(-89.38, -4.07) * mm]});
            skFitSpline(sketch, "E242", {"points": [v(-89.38, -4.07) * mm, v(-89.41, -4.39) * mm, v(-89.44, -4.72) * mm, v(-89.45, -5.05) * mm]});
            skFitSpline(sketch, "E243", {"points": [v(-89.45, -5.05) * mm, v(-89.47, -5.37) * mm, v(-89.46, -5.64) * mm, v(-89.43, -5.86) * mm]});
            skFitSpline(sketch, "E244", {"points": [v(-89.43, -5.86) * mm, v(-89.38, -6.07) * mm, v(-89.3, -6.22) * mm, v(-89.2, -6.28) * mm]});
            skFitSpline(sketch, "E245", {"points": [v(-89.2, -6.28) * mm, v(-89.08, -6.35) * mm, v(-88.9, -6.3) * mm, v(-88.68, -6.1) * mm]});
            skFitSpline(sketch, "E246", {"points": [v(-88.68, -6.1) * mm, v(-88.27, -5.7) * mm, v(-87.84, -5.19) * mm, v(-87.38, -4.55) * mm]});
            skFitSpline(sketch, "E247", {"points": [v(-87.38, -4.55) * mm, v(-86.91, -3.9) * mm, v(-86.46, -3.2) * mm, v(-86.02, -2.49) * mm]});
            skFitSpline(sketch, "E248", {"points": [v(-86.02, -2.49) * mm, v(-85.55, -1.75) * mm, v(-85.12, -1.01) * mm, v(-84.7, -0.27) * mm]});
            skFitSpline(sketch, "E249", {"points": [v(-84.7, -0.27) * mm, v(-84.28, 0.48) * mm, v(-83.9, 1.17) * mm, v(-83.55, 1.79) * mm]});
            skFitSpline(sketch, "E250", {"points": [v(-83.55, 1.79) * mm, v(-83.36, 2.19) * mm, v(-83.18, 2.57) * mm, v(-82.99, 2.92) * mm]});
            skFitSpline(sketch, "E251", {"points": [v(-82.99, 2.92) * mm, v(-82.78, 3.29) * mm, v(-82.61, 3.59) * mm, v(-82.47, 3.82) * mm]});
            skFitSpline(sketch, "E252", {"points": [v(-82.47, 3.82) * mm, v(-82.35, 3.87) * mm, v(-82.23, 3.9) * mm, v(-82.09, 3.9) * mm]});
            skFitSpline(sketch, "E253", {"points": [v(-82.09, 3.9) * mm, v(-81.94, 3.9) * mm, v(-81.82, 3.85) * mm, v(-81.73, 3.75) * mm]});
            skFitSpline(sketch, "E254", {"points": [v(-81.73, 3.75) * mm, v(-81.63, 3.66) * mm, v(-81.54, 3.56) * mm, v(-81.47, 3.42) * mm]});
            skFitSpline(sketch, "E255", {"points": [v(-81.73, 2.87) * mm, v(-81.97, 2.4) * mm, v(-82.25, 1.85) * mm, v(-82.58, 1.23) * mm]});
            skFitSpline(sketch, "E256", {"points": [v(-82.58, 1.23) * mm, v(-82.88, 0.61) * mm, v(-83.23, -0.04) * mm, v(-83.6, -0.73) * mm]});
            skFitSpline(sketch, "E257", {"points": [v(-83.6, -0.73) * mm, v(-83.96, -1.41) * mm, v(-84.36, -2.1) * mm, v(-84.78, -2.81) * mm]});
            skFitSpline(sketch, "E258", {"points": [v(-84.78, -2.81) * mm, v(-85.2, -3.52) * mm, v(-85.61, -4.19) * mm, v(-86.04, -4.82) * mm]});
            skFitSpline(sketch, "E259", {"points": [v(-86.04, -4.82) * mm, v(-86.45, -5.46) * mm, v(-86.88, -6.05) * mm, v(-87.32, -6.58) * mm]});
            skFitSpline(sketch, "E260", {"points": [v(-87.32, -6.58) * mm, v(-87.75, -7.1) * mm, v(-88.16, -7.52) * mm, v(-88.56, -7.84) * mm]});
            skFitSpline(sketch, "E261", {"points": [v(-88.56, -7.84) * mm, v(-88.9, -8.13) * mm, v(-89.3, -8.36) * mm, v(-89.79, -8.55) * mm]});
            skFitSpline(sketch, "E262", {"points": [v(-89.79, -8.55) * mm, v(-90.27, -8.73) * mm, v(-90.74, -8.82) * mm, v(-91.2, -8.82) * mm]});
            skFitSpline(sketch, "E263", {"points": [v(-91.2, -8.82) * mm, v(-91.81, -8.82) * mm, v(-92.3, -8.61) * mm, v(-92.64, -8.2) * mm]});
            skFitSpline(sketch, "E264", {"points": [v(-92.64, -8.2) * mm, v(-92.98, -7.76) * mm, v(-93.23, -7.25) * mm, v(-93.4, -6.66) * mm]});
            skFitSpline(sketch, "E265", {"points": [v(-93.4, -6.66) * mm, v(-93.56, -6.06) * mm, v(-93.65, -5.44) * mm, v(-93.66, -4.8) * mm]});
            skFitSpline(sketch, "E266", {"points": [v(-93.66, -4.8) * mm, v(-93.68, -4.16) * mm, v(-93.65, -3.63) * mm, v(-93.59, -3.22) * mm]});
            skFitSpline(sketch, "E267", {"points": [v(-93.59, -3.22) * mm, v(-93.59, -3.18) * mm, v(-93.59, -3.17) * mm]});
            skFitSpline(sketch, "E268", {"points": [v(-93.59, -3.17) * mm, v(-93.59, -3.15) * mm, v(-93.58, -3.08) * mm, v(-93.56, -2.96) * mm]});
            skFitSpline(sketch, "E269", {"points": [v(-93.56, -2.96) * mm, v(-94.02, -3.72) * mm, v(-94.53, -4.46) * mm, v(-95.1, -5.18) * mm]});
            skFitSpline(sketch, "E270", {"points": [v(-95.1, -5.18) * mm, v(-95.65, -5.88) * mm, v(-96.24, -6.5) * mm, v(-96.87, -7.06) * mm]});
            skFitSpline(sketch, "E271", {"points": [v(-96.87, -7.06) * mm, v(-97.49, -7.62) * mm, v(-98.14, -8.07) * mm, v(-98.82, -8.42) * mm]});
            skFitSpline(sketch, "E272", {"points": [v(-98.82, -8.42) * mm, v(-99.5, -8.76) * mm, v(-100.2, -8.92) * mm, v(-100.92, -8.92) * mm]});
            skFitSpline(sketch, "E273", {"points": [v(-100.92, -8.92) * mm, v(-101.6, -8.92) * mm, v(-102.16, -8.8) * mm, v(-102.62, -8.57) * mm]});
            skFitSpline(sketch, "E274", {"points": [v(-102.62, -8.57) * mm, v(-103.08, -8.34) * mm, v(-103.45, -8.03) * mm, v(-103.72, -7.64) * mm]});
            skFitSpline(sketch, "E275", {"points": [v(-103.72, -7.64) * mm, v(-104, -7.26) * mm, v(-104.2, -6.8) * mm, v(-104.31, -6.28) * mm]});
            skFitSpline(sketch, "E276", {"points": [v(-104.31, -6.28) * mm, v(-104.43, -5.76) * mm, v(-104.5, -5.22) * mm, v(-104.5, -4.65) * mm]});
            skFitSpline(sketch, "E277", {"points": [v(-104.5, -4.65) * mm, v(-104.5, -4.55) * mm, v(-104.5, -4.43) * mm, v(-104.5, -4.3) * mm]});
            skFitSpline(sketch, "E278", {"points": [v(-104.5, -4.3) * mm, v(-104.5, -4.16) * mm, v(-104.48, -4.04) * mm, v(-104.47, -3.92) * mm]});
            skFitSpline(sketch, "E279", {"points": [v(-104.47, -3.92) * mm, v(-104.36, -3.08) * mm, v(-104.14, -2.15) * mm, v(-103.8, -1.13) * mm]});
            skFitSpline(sketch, "E280", {"points": [v(-103.8, -1.13) * mm, v(-103.47, -0.1) * mm, v(-103.05, 0.92) * mm, v(-102.54, 1.96) * mm]});
            skFitSpline(sketch, "E281", {"points": [v(-102.54, 1.96) * mm, v(-102.01, 3.02) * mm, v(-101.4, 4.04) * mm, v(-100.72, 5.03) * mm]});
            skFitSpline(sketch, "E282", {"points": [v(-100.72, 5.03) * mm, v(-100.03, 6.02) * mm, v(-99.3, 6.9) * mm, v(-98.49, 7.65) * mm]});
            skFitSpline(sketch, "E283", {"points": [v(-98.49, 7.65) * mm, v(-97.67, 8.42) * mm, v(-96.8, 9.03) * mm, v(-95.9, 9.48) * mm]});
            skFitSpline(sketch, "E284", {"points": [v(-95.9, 9.48) * mm, v(-94.99, 9.95) * mm, v(-94.05, 10.19) * mm, v(-93.07, 10.19) * mm]});
            skFitSpline(sketch, "E285", {"points": [v(-93.07, 10.19) * mm, v(-92.32, 10.19) * mm, v(-91.65, 10) * mm, v(-91.07, 9.66) * mm]});
            skFitSpline(sketch, "E286", {"points": [v(-91.07, 9.66) * mm, v(-90.49, 9.3) * mm, v(-90, 8.84) * mm, v(-89.6, 8.27) * mm]});
            skFitSpline(sketch, "E287", {"points": [v(-89.6, 8.27) * mm, v(-89.21, 7.72) * mm, v(-88.93, 7.1) * mm, v(-88.76, 6.39) * mm]});
            skFitSpline(sketch, "E288", {"points": [v(-88.76, 6.39) * mm, v(-88.57, 5.7) * mm, v(-88.5, 5) * mm, v(-88.56, 4.3) * mm]});
            skFitSpline(sketch, "E289", {"points": [v(-88.56, 4.3) * mm, v(-88.6, 3.82) * mm, v(-88.7, 3.36) * mm, v(-88.86, 2.94) * mm]});
            skFitSpline(sketch, "E290", {"points": [v(-51.72, -0.45) * mm, v(-52.53, -0.87) * mm, v(-53.25, -1.4) * mm, v(-53.9, -2.03) * mm]});
            skFitSpline(sketch, "E291", {"points": [v(-53.9, -2.03) * mm, v(-54.54, -2.67) * mm, v(-55.03, -3.43) * mm, v(-55.4, -4.32) * mm]});
            skFitSpline(sketch, "E292", {"points": [v(-55.4, -4.32) * mm, v(-55.5, -4.44) * mm, v(-55.63, -4.45) * mm, v(-55.8, -4.35) * mm]});
            skFitSpline(sketch, "E293", {"points": [v(-55.8, -4.35) * mm, v(-55.96, -4.25) * mm, v(-56.05, -4.12) * mm, v(-56.08, -3.97) * mm]});
            skFitSpline(sketch, "E294", {"points": [v(-56.08, -3.97) * mm, v(-55.86, -2.41) * mm, v(-55.34, -1.09) * mm, v(-54.52, 0) * mm]});
            skFitSpline(sketch, "E295", {"points": [v(-54.52, 0) * mm, v(-53.68, 1.1) * mm, v(-52.68, 1.89) * mm, v(-51.52, 2.4) * mm]});
            skFitSpline(sketch, "E296", {"points": [v(-51.52, 2.4) * mm, v(-51.48, 2.81) * mm, v(-51.46, 3.24) * mm, v(-51.46, 3.67) * mm]});
            skFitSpline(sketch, "E297", {"points": [v(-51.46, 3.67) * mm, v(-51.45, 4.1) * mm, v(-51.43, 4.55) * mm, v(-51.41, 5) * mm]});
            skFitSpline(sketch, "E298", {"points": [v(-51.41, 5) * mm, v(-51.41, 5.07) * mm, v(-51.41, 5.16) * mm, v(-51.41, 5.26) * mm]});
            skFitSpline(sketch, "E299", {"points": [v(-51.41, 5.26) * mm, v(-51.4, 5.37) * mm, v(-51.39, 5.47) * mm, v(-51.39, 5.53) * mm]});
            skFitSpline(sketch, "E300", {"points": [v(-51.39, 5.53) * mm, v(-51.37, 5.62) * mm, v(-51.36, 5.7) * mm, v(-51.36, 5.81) * mm]});
            skFitSpline(sketch, "E301", {"points": [v(-51.36, 5.81) * mm, v(-51.36, 5.93) * mm, v(-51.36, 6.03) * mm, v(-51.36, 6.11) * mm]});
            skFitSpline(sketch, "E302", {"points": [v(-51.36, 6.11) * mm, v(-51.36, 6.33) * mm, v(-51.35, 6.54) * mm, v(-51.34, 6.74) * mm]});
            skFitSpline(sketch, "E303", {"points": [v(-51.34, 6.74) * mm, v(-51.32, 6.96) * mm, v(-51.31, 7.18) * mm, v(-51.31, 7.4) * mm]});
            skFitSpline(sketch, "E304", {"points": [v(-51.31, 7.4) * mm, v(-51.26, 8.58) * mm, v(-51.18, 9.95) * mm, v(-51.08, 11.5) * mm]});
            skFitSpline(sketch, "E305", {"points": [v(-51.08, 11.5) * mm, v(-51.35, 11.36) * mm, v(-51.68, 11.22) * mm, v(-52.05, 11.07) * mm]});
            skFitSpline(sketch, "E306", {"points": [v(-52.05, 11.07) * mm, v(-52.43, 10.93) * mm, v(-52.84, 10.8) * mm, v(-53.29, 10.69) * mm]});
            skFitSpline(sketch, "E307", {"points": [v(-53.29, 10.69) * mm, v(-53.71, 10.59) * mm, v(-54.16, 10.5) * mm, v(-54.62, 10.41) * mm]});
            skFitSpline(sketch, "E308", {"points": [v(-54.62, 10.41) * mm, v(-55.08, 10.34) * mm, v(-55.54, 10.31) * mm, v(-55.98, 10.31) * mm]});
            skFitSpline(sketch, "E309", {"points": [v(-55.98, 10.31) * mm, v(-56.61, 10.31) * mm, v(-57.18, 10.44) * mm, v(-57.67, 10.69) * mm]});
            skFitSpline(sketch, "E310", {"points": [v(-57.67, 10.69) * mm, v(-58.17, 10.96) * mm, v(-58.48, 11.38) * mm, v(-58.6, 11.95) * mm]});
            skFitSpline(sketch, "E311", {"points": [v(-58.6, 11.95) * mm, v(-58.67, 12.21) * mm, v(-58.7, 12.5) * mm, v(-58.7, 12.8) * mm]});
            skFitSpline(sketch, "E312", {"points": [v(-58.7, 12.8) * mm, v(-58.7, 13.44) * mm, v(-58.55, 14.05) * mm, v(-58.24, 14.64) * mm]});
            skFitSpline(sketch, "E313", {"points": [v(-58.24, 14.64) * mm, v(-57.91, 15.24) * mm, v(-57.5, 15.78) * mm, v(-57, 16.24) * mm]});
            skFitSpline(sketch, "E314", {"points": [v(-57, 16.24) * mm, v(-56.5, 16.73) * mm, v(-55.93, 17.13) * mm, v(-55.31, 17.45) * mm]});
            skFitSpline(sketch, "E315", {"points": [v(-55.31, 17.45) * mm, v(-54.68, 17.77) * mm, v(-54.05, 17.97) * mm, v(-53.41, 18.05) * mm]});
            skFitSpline(sketch, "E316", {"points": [v(-53.41, 18.05) * mm, v(-53.35, 18.05) * mm, v(-53.27, 18.05) * mm, v(-53.18, 18.05) * mm]});
            skFitSpline(sketch, "E317", {"points": [v(-53.18, 18.05) * mm, v(-53.08, 18.07) * mm, v(-52.99, 18.09) * mm, v(-52.9, 18.1) * mm]});
            skFitSpline(sketch, "E318", {"points": [v(-52.9, 18.1) * mm, v(-52.76, 18.12) * mm, v(-52.63, 18.13) * mm, v(-52.5, 18.13) * mm]});
            skFitSpline(sketch, "E319", {"points": [v(-52.5, 18.13) * mm, v(-52.34, 18.15) * mm, v(-52.2, 18.16) * mm, v(-52.05, 18.16) * mm]});
            skFitSpline(sketch, "E320", {"points": [v(-52.05, 18.16) * mm, v(-51.22, 18.16) * mm, v(-50.41, 18.01) * mm, v(-49.64, 17.73) * mm]});
            skFitSpline(sketch, "E321", {"points": [v(-49.64, 17.73) * mm, v(-48.86, 17.46) * mm, v(-48.15, 17.02) * mm, v(-47.51, 16.42) * mm]});
            skFitSpline(sketch, "E322", {"points": [v(-47.51, 16.42) * mm, v(-45.78, 16.9) * mm, v(-43.97, 17.36) * mm, v(-42.07, 17.78) * mm]});
            skFitSpline(sketch, "E323", {"points": [v(-42.07, 17.78) * mm, v(-40.17, 18.2) * mm, v(-38.25, 18.6) * mm, v(-36.3, 18.99) * mm]});
            skFitSpline(sketch, "E324", {"points": [v(-36.3, 18.99) * mm, v(-34.9, 19.27) * mm, v(-33.46, 19.57) * mm, v(-31.99, 19.9) * mm]});
            skFitSpline(sketch, "E325", {"points": [v(-31.99, 19.9) * mm, v(-30.52, 20.2) * mm, v(-29.06, 20.54) * mm, v(-27.63, 20.87) * mm]});
            skFitSpline(sketch, "E326", {"points": [v(-27.63, 20.87) * mm, v(-26.19, 21.22) * mm, v(-24.79, 21.6) * mm, v(-23.42, 21.98) * mm]});
            skFitSpline(sketch, "E327", {"points": [v(-23.42, 21.98) * mm, v(-22.03, 22.36) * mm, v(-20.73, 22.76) * mm, v(-19.52, 23.18) * mm]});
            skFitSpline(sketch, "E328", {"points": [v(-19.54, 23.18) * mm, v(-19.4, 23.23) * mm, v(-19.2, 23.3) * mm, v(-18.9, 23.41) * mm]});
            skFitSpline(sketch, "E329", {"points": [v(-18.9, 23.41) * mm, v(-18.6, 23.53) * mm, v(-18.29, 23.65) * mm, v(-17.98, 23.79) * mm]});
            skFitSpline(sketch, "E330", {"points": [v(-17.98, 23.79) * mm, v(-17.65, 23.92) * mm, v(-17.36, 24.07) * mm, v(-17.1, 24.24) * mm]});
            skFitSpline(sketch, "E331", {"points": [v(-17.1, 24.24) * mm, v(-16.83, 24.4) * mm, v(-16.66, 24.58) * mm, v(-16.6, 24.77) * mm]});
            skFitSpline(sketch, "E332", {"points": [v(-16.6, 24.77) * mm, v(-16.57, 24.85) * mm, v(-16.56, 24.93) * mm, v(-16.54, 25) * mm]});
            skFitSpline(sketch, "E333", {"points": [v(-16.54, 25) * mm, v(-16.52, 25.06) * mm, v(-16.52, 25.12) * mm, v(-16.52, 25.17) * mm]});
            skFitSpline(sketch, "E334", {"points": [v(-16.52, 25.17) * mm, v(-16.52, 25.25) * mm, v(-16.5, 25.33) * mm, v(-16.49, 25.4) * mm]});
            skFitSpline(sketch, "E335", {"points": [v(-16.49, 25.4) * mm, v(-16.47, 25.46) * mm, v(-16.41, 25.51) * mm, v(-16.3, 25.55) * mm]});
            skFitSpline(sketch, "E336", {"points": [v(-16.34, 25.55) * mm, v(-16.23, 25.58) * mm, v(-16.12, 25.57) * mm, v(-16, 25.52) * mm]});
            skFitSpline(sketch, "E337", {"points": [v(-16, 25.52) * mm, v(-15.88, 25.47) * mm, v(-15.79, 25.38) * mm, v(-15.72, 25.25) * mm]});
            skFitSpline(sketch, "E338", {"points": [v(-15.72, 25.25) * mm, v(-15.55, 24.94) * mm, v(-15.56, 24.62) * mm, v(-15.75, 24.26) * mm]});
            skFitSpline(sketch, "E339", {"points": [v(-15.75, 24.26) * mm, v(-15.92, 23.91) * mm, v(-16.16, 23.57) * mm, v(-16.49, 23.23) * mm]});
            skFitSpline(sketch, "E340", {"points": [v(-16.49, 23.23) * mm, v(-16.81, 22.92) * mm, v(-17.17, 22.63) * mm, v(-17.54, 22.38) * mm]});
            skFitSpline(sketch, "E341", {"points": [v(-17.54, 22.38) * mm, v(-17.9, 22.13) * mm, v(-18.17, 21.94) * mm, v(-18.36, 21.83) * mm]});
            skFitSpline(sketch, "E342", {"points": [v(-18.36, 21.83) * mm, v(-19.8, 20.97) * mm, v(-21.44, 20.2) * mm, v(-23.29, 19.49) * mm]});
            skFitSpline(sketch, "E343", {"points": [v(-23.29, 19.49) * mm, v(-25.14, 18.78) * mm, v(-27.04, 18.14) * mm, v(-29.01, 17.55) * mm]});
            skFitSpline(sketch, "E344", {"points": [v(-29.01, 17.55) * mm, v(-30.96, 16.97) * mm, v(-32.9, 16.44) * mm, v(-34.81, 15.97) * mm]});
            skFitSpline(sketch, "E345", {"points": [v(-34.81, 15.97) * mm, v(-36.73, 15.52) * mm, v(-38.48, 15.1) * mm, v(-40.07, 14.74) * mm]});
            skFitSpline(sketch, "E346", {"points": [v(-41.35, 14.43) * mm, v(-42.28, 14.23) * mm, v(-43.13, 14.04) * mm, v(-43.92, 13.86) * mm]});
            skFitSpline(sketch, "E347", {"points": [v(-43.92, 13.86) * mm, v(-44.7, 13.67) * mm, v(-45.35, 13.48) * mm, v(-45.9, 13.28) * mm]});
            skFitSpline(sketch, "E348", {"points": [v(-45.9, 13.28) * mm, v(-45.9, 13.18) * mm, v(-45.9, 13.08) * mm, v(-45.9, 12.98) * mm]});
            skFitSpline(sketch, "E349", {"points": [v(-45.9, 12.98) * mm, v(-45.88, 12.88) * mm, v(-45.87, 12.74) * mm, v(-45.87, 12.57) * mm]});
            skFitSpline(sketch, "E350", {"points": [v(-45.87, 12.57) * mm, v(-45.85, 12.42) * mm, v(-45.84, 12.23) * mm, v(-45.84, 12) * mm]});
            skFitSpline(sketch, "E351", {"points": [v(-45.84, 12) * mm, v(-45.83, 11.76) * mm, v(-45.82, 11.47) * mm, v(-45.82, 11.12) * mm]});
            skFitSpline(sketch, "E352", {"points": [v(-45.82, 11.12) * mm, v(-45.82, 10.8) * mm, v(-45.82, 10.42) * mm, v(-45.82, 9.98) * mm]});
            skFitSpline(sketch, "E353", {"points": [v(-45.82, 9.98) * mm, v(-45.82, 9.57) * mm, v(-45.83, 9.06) * mm, v(-45.84, 8.48) * mm]});
            skFitSpline(sketch, "E354", {"points": [v(-45.84, 8.48) * mm, v(-45.86, 7.9) * mm, v(-45.89, 7.24) * mm, v(-45.92, 6.46) * mm]});
            skFitSpline(sketch, "E355", {"points": [v(-45.92, 6.46) * mm, v(-45.94, 5.7) * mm, v(-45.98, 4.84) * mm, v(-46.05, 3.85) * mm]});
            skFitSpline(sketch, "E356", {"points": [v(-46.05, 3.85) * mm, v(-46.02, 3.85) * mm, v(-45.96, 3.85) * mm, v(-45.9, 3.85) * mm]});
            skFitSpline(sketch, "E357", {"points": [v(-45.9, 3.85) * mm, v(-45.83, 3.85) * mm, v(-45.77, 3.86) * mm, v(-45.72, 3.87) * mm]});
            skFitSpline(sketch, "E358", {"points": [v(-45.72, 3.87) * mm, v(-45.68, 3.87) * mm, v(-45.65, 3.87) * mm, v(-45.61, 3.87) * mm]});
            skFitSpline(sketch, "E359", {"points": [v(-45.61, 3.87) * mm, v(-45.58, 3.87) * mm, v(-45.55, 3.88) * mm, v(-45.54, 3.9) * mm]});
            skFitSpline(sketch, "E360", {"points": [v(-45.56, 3.9) * mm, v(-44.76, 4.05) * mm, v(-43.95, 4.2) * mm, v(-43.15, 4.38) * mm]});
            skFitSpline(sketch, "E361", {"points": [v(-43.15, 4.38) * mm, v(-42.35, 4.54) * mm, v(-41.58, 4.75) * mm, v(-40.84, 4.98) * mm]});
            skFitSpline(sketch, "E362", {"points": [v(-40.84, 4.98) * mm, v(-40.09, 5.23) * mm, v(-39.4, 5.52) * mm, v(-38.76, 5.84) * mm]});
            skFitSpline(sketch, "E363", {"points": [v(-38.76, 5.84) * mm, v(-38.13, 6.17) * mm, v(-37.6, 6.57) * mm, v(-37.15, 7.04) * mm]});
            skFitSpline(sketch, "E364", {"points": [v(-37.15, 7.04) * mm, v(-37.06, 7.16) * mm, v(-36.98, 7.22) * mm, v(-36.91, 7.22) * mm]});
            skFitSpline(sketch, "E365", {"points": [v(-36.91, 7.22) * mm, v(-36.85, 7.22) * mm, v(-36.79, 7.18) * mm, v(-36.74, 7.1) * mm]});
            skFitSpline(sketch, "E366", {"points": [v(-36.74, 7.1) * mm, v(-36.68, 7.03) * mm, v(-36.64, 6.93) * mm, v(-36.6, 6.82) * mm]});
            skFitSpline(sketch, "E367", {"points": [v(-36.6, 6.82) * mm, v(-36.57, 6.7) * mm, v(-36.55, 6.59) * mm, v(-36.53, 6.49) * mm]});
            skFitSpline(sketch, "E368", {"points": [v(-36.53, 6.49) * mm, v(-36.65, 5.7) * mm, v(-36.97, 5.03) * mm, v(-37.48, 4.48) * mm]});
            skFitSpline(sketch, "E369", {"points": [v(-37.48, 4.48) * mm, v(-38, 3.92) * mm, v(-38.63, 3.46) * mm, v(-39.38, 3.07) * mm]});
            skFitSpline(sketch, "E370", {"points": [v(-39.38, 3.07) * mm, v(-40.13, 2.7) * mm, v(-40.98, 2.38) * mm, v(-41.92, 2.11) * mm]});
            skFitSpline(sketch, "E371", {"points": [v(-41.92, 2.11) * mm, v(-42.86, 1.86) * mm, v(-43.82, 1.64) * mm, v(-44.8, 1.44) * mm]});
            skFitSpline(sketch, "E372", {"points": [v(-45.54, 1.31) * mm, v(-45.64, 1.28) * mm, v(-45.74, 1.24) * mm, v(-45.84, 1.2) * mm]});
            skFitSpline(sketch, "E373", {"points": [v(-45.84, 1.2) * mm, v(-45.95, 1.2) * mm, v(-46.1, 1.18) * mm, v(-46.28, 1.16) * mm]});
            skFitSpline(sketch, "E374", {"points": [v(-46.28, 0.6) * mm, v(-46.28, 0.57) * mm, v(-46.29, 0.55) * mm, v(-46.3, 0.53) * mm]});
            skFitSpline(sketch, "E375", {"points": [v(-46.3, 0.53) * mm, v(-46.3, 0.51) * mm, v(-46.3, 0.5) * mm, v(-46.3, 0.48) * mm]});
            skFitSpline(sketch, "E376", {"points": [v(-46.28, 0.38) * mm, v(-46.45, -1.35) * mm, v(-46.7, -3.15) * mm, v(-47.03, -5.03) * mm]});
            skFitSpline(sketch, "E377", {"points": [v(-47.03, -5.03) * mm, v(-47.35, -6.9) * mm, v(-47.82, -8.74) * mm, v(-48.44, -10.53) * mm]});
            skFitSpline(sketch, "E378", {"points": [v(-48.44, -10.53) * mm, v(-49.05, -12.33) * mm, v(-49.85, -14.03) * mm, v(-50.82, -15.64) * mm]});
            skFitSpline(sketch, "E379", {"points": [v(-50.82, -15.64) * mm, v(-51.78, -17.24) * mm, v(-52.98, -18.64) * mm, v(-54.42, -19.8) * mm]});
            skFitSpline(sketch, "E380", {"points": [v(-54.42, -19.8) * mm, v(-54.91, -20.16) * mm, v(-55.45, -20.48) * mm, v(-56.03, -20.76) * mm]});
            skFitSpline(sketch, "E381", {"points": [v(-56.03, -20.76) * mm, v(-56.61, -21.05) * mm, v(-57.22, -21.3) * mm, v(-57.85, -21.5) * mm]});
            skFitSpline(sketch, "E382", {"points": [v(-57.85, -21.5) * mm, v(-58.49, -21.7) * mm, v(-59.14, -21.85) * mm, v(-59.8, -21.97) * mm]});
            skFitSpline(sketch, "E383", {"points": [v(-59.8, -21.97) * mm, v(-60.47, -22.09) * mm, v(-61.12, -22.15) * mm, v(-61.75, -22.15) * mm]});
            skFitSpline(sketch, "E384", {"points": [v(-62.86, -22.15) * mm, v(-64.3, -21.95) * mm, v(-65.59, -21.51) * mm, v(-66.73, -20.84) * mm]});
            skFitSpline(sketch, "E385", {"points": [v(-66.73, -20.84) * mm, v(-67.86, -20.17) * mm, v(-68.82, -19.32) * mm, v(-69.6, -18.3) * mm]});
            skFitSpline(sketch, "E386", {"points": [v(-69.6, -18.3) * mm, v(-70.4, -17.28) * mm, v(-71, -16.1) * mm, v(-71.4, -14.78) * mm]});
            skFitSpline(sketch, "E387", {"points": [v(-71.4, -14.78) * mm, v(-71.83, -13.46) * mm, v(-72.04, -12.05) * mm, v(-72.04, -10.56) * mm]});
            skFitSpline(sketch, "E388", {"points": [v(-72.04, -10.56) * mm, v(-72.04, -9.37) * mm, v(-71.88, -8.19) * mm, v(-71.56, -7.01) * mm]});
            skFitSpline(sketch, "E389", {"points": [v(-71.56, -7.01) * mm, v(-71.25, -5.84) * mm, v(-70.8, -4.75) * mm, v(-70.22, -3.74) * mm]});
            skFitSpline(sketch, "E390", {"points": [v(-70.22, -3.74) * mm, v(-69.62, -2.74) * mm, v(-68.9, -1.85) * mm, v(-68.04, -1.08) * mm]});
            skFitSpline(sketch, "E391", {"points": [v(-68.04, -1.08) * mm, v(-67.19, -0.3) * mm, v(-66.22, 0.27) * mm, v(-65.14, 0.66) * mm]});
            skFitSpline(sketch, "E392", {"points": [v(-65.14, 0.66) * mm, v(-64.8, 0.77) * mm, v(-64.47, 0.85) * mm, v(-64.14, 0.88) * mm]});
            skFitSpline(sketch, "E393", {"points": [v(-64.14, 0.88) * mm, v(-63.8, 0.93) * mm, v(-63.47, 0.96) * mm, v(-63.17, 0.96) * mm]});
            skFitSpline(sketch, "E394", {"points": [v(-63.17, 0.96) * mm, v(-62.36, 0.96) * mm, v(-61.69, 0.8) * mm, v(-61.14, 0.46) * mm]});
            skFitSpline(sketch, "E395", {"points": [v(-61.14, 0.46) * mm, v(-60.6, 0.14) * mm, v(-60.15, -0.3) * mm, v(-59.8, -0.85) * mm]});
            skFitSpline(sketch, "E396", {"points": [v(-59.8, -0.85) * mm, v(-59.46, -1.4) * mm, v(-59.21, -2.05) * mm, v(-59.06, -2.79) * mm]});
            skFitSpline(sketch, "E397", {"points": [v(-59.06, -2.79) * mm, v(-58.9, -3.5) * mm, v(-58.83, -4.27) * mm, v(-58.83, -5.08) * mm]});
            skFitSpline(sketch, "E398", {"points": [v(-58.83, -5.08) * mm, v(-58.83, -5.66) * mm, v(-58.85, -6.18) * mm, v(-58.88, -6.63) * mm]});
            skFitSpline(sketch, "E399", {"points": [v(-58.88, -6.63) * mm, v(-58.91, -7.09) * mm, v(-58.95, -7.48) * mm, v(-58.98, -7.82) * mm]});
            skFitSpline(sketch, "E400", {"points": [v(-58.98, -7.8) * mm, v(-59.09, -8) * mm, v(-59.2, -8.17) * mm, v(-59.32, -8.27) * mm]});
            skFitSpline(sketch, "E401", {"points": [v(-59.32, -8.27) * mm, v(-59.42, -8.37) * mm, v(-59.52, -8.44) * mm, v(-59.62, -8.47) * mm]});
            skFitSpline(sketch, "E402", {"points": [v(-59.62, -8.47) * mm, v(-59.73, -8.49) * mm, v(-59.82, -8.49) * mm, v(-59.9, -8.47) * mm]});
            skFitSpline(sketch, "E403", {"points": [v(-59.9, -8.47) * mm, v(-60, -8.44) * mm, v(-60.06, -8.4) * mm, v(-60.11, -8.37) * mm]});
            skFitSpline(sketch, "E404", {"points": [v(-60.11, -8.37) * mm, v(-60.13, -8.29) * mm, v(-60.14, -8.21) * mm, v(-60.14, -8.14) * mm]});
            skFitSpline(sketch, "E405", {"points": [v(-60.14, -8.14) * mm, v(-60.12, -8.06) * mm, v(-60.11, -7.98) * mm, v(-60.11, -7.9) * mm]});
            skFitSpline(sketch, "E406", {"points": [v(-60.11, -6.28) * mm, v(-60.11, -6.23) * mm, v(-60.11, -6.18) * mm, v(-60.11, -6.13) * mm]});
            skFitSpline(sketch, "E407", {"points": [v(-60.11, -6.13) * mm, v(-60.1, -6.08) * mm, v(-60.09, -6.02) * mm, v(-60.09, -5.96) * mm]});
            skFitSpline(sketch, "E408", {"points": [v(-60.09, -5.96) * mm, v(-60.09, -5.45) * mm, v(-60.11, -4.95) * mm, v(-60.16, -4.45) * mm]});
            skFitSpline(sketch, "E409", {"points": [v(-60.16, -4.45) * mm, v(-60.2, -3.94) * mm, v(-60.3, -3.5) * mm, v(-60.45, -3.09) * mm]});
            skFitSpline(sketch, "E410", {"points": [v(-60.45, -3.09) * mm, v(-60.6, -2.69) * mm, v(-60.82, -2.36) * mm, v(-61.11, -2.1) * mm]});
            skFitSpline(sketch, "E411", {"points": [v(-61.11, -2.1) * mm, v(-61.39, -1.84) * mm, v(-61.76, -1.7) * mm, v(-62.24, -1.68) * mm]});
            skFitSpline(sketch, "E412", {"points": [v(-62.24, -1.68) * mm, v(-62.67, -1.65) * mm, v(-63.1, -1.74) * mm, v(-63.52, -1.96) * mm]});
            skFitSpline(sketch, "E413", {"points": [v(-63.52, -1.96) * mm, v(-63.94, -2.18) * mm, v(-64.35, -2.5) * mm, v(-64.76, -2.91) * mm]});
            skFitSpline(sketch, "E414", {"points": [v(-64.76, -2.91) * mm, v(-65.17, -3.33) * mm, v(-65.56, -3.84) * mm, v(-65.94, -4.42) * mm]});
            skFitSpline(sketch, "E415", {"points": [v(-65.94, -4.42) * mm, v(-66.3, -5) * mm, v(-66.63, -5.62) * mm, v(-66.94, -6.3) * mm]});
            skFitSpline(sketch, "E416", {"points": [v(-66.94, -6.3) * mm, v(-67.25, -6.98) * mm, v(-67.52, -7.7) * mm, v(-67.76, -8.45) * mm]});
            skFitSpline(sketch, "E417", {"points": [v(-67.76, -8.45) * mm, v(-67.98, -9.18) * mm, v(-68.15, -9.93) * mm, v(-68.27, -10.68) * mm]});
            skFitSpline(sketch, "E418", {"points": [v(-68.27, -10.68) * mm, v(-68.34, -11.12) * mm, v(-68.38, -11.48) * mm, v(-68.4, -11.76) * mm]});
            skFitSpline(sketch, "E419", {"points": [v(-68.4, -11.76) * mm, v(-68.42, -12.05) * mm, v(-68.43, -12.28) * mm, v(-68.43, -12.44) * mm]});
            skFitSpline(sketch, "E420", {"points": [v(-68.43, -12.44) * mm, v(-68.43, -13.53) * mm, v(-68.29, -14.56) * mm, v(-68.02, -15.54) * mm]});
            skFitSpline(sketch, "E421", {"points": [v(-68.02, -15.54) * mm, v(-67.74, -16.5) * mm, v(-67.37, -17.36) * mm, v(-66.89, -18.1) * mm]});
            skFitSpline(sketch, "E422", {"points": [v(-66.89, -18.1) * mm, v(-66.4, -18.84) * mm, v(-65.8, -19.42) * mm, v(-65.14, -19.86) * mm]});
            skFitSpline(sketch, "E423", {"points": [v(-65.14, -19.86) * mm, v(-64.47, -20.31) * mm, v(-63.74, -20.55) * mm, v(-62.93, -20.56) * mm]});
            skFitSpline(sketch, "E424", {"points": [v(-62.93, -20.56) * mm, v(-61.87, -20.5) * mm, v(-60.9, -20.21) * mm, v(-60.03, -19.7) * mm]});
            skFitSpline(sketch, "E425", {"points": [v(-60.03, -19.7) * mm, v(-59.15, -19.22) * mm, v(-58.34, -18.58) * mm, v(-57.62, -17.77) * mm]});
            skFitSpline(sketch, "E426", {"points": [v(-57.62, -17.77) * mm, v(-56.89, -16.99) * mm, v(-56.24, -16.07) * mm, v(-55.67, -15.03) * mm]});
            skFitSpline(sketch, "E427", {"points": [v(-55.67, -15.03) * mm, v(-55.1, -14) * mm, v(-54.61, -12.93) * mm, v(-54.18, -11.79) * mm]});
            skFitSpline(sketch, "E428", {"points": [v(-54.18, -11.79) * mm, v(-53.74, -10.65) * mm, v(-53.36, -9.48) * mm, v(-53.06, -8.3) * mm]});
            skFitSpline(sketch, "E429", {"points": [v(-53.06, -8.3) * mm, v(-52.75, -7.1) * mm, v(-52.5, -5.96) * mm, v(-52.29, -4.85) * mm]});
            skFitSpline(sketch, "E430", {"points": [v(-52.29, -4.85) * mm, v(-52.01, -3.37) * mm, v(-51.8, -1.92) * mm, v(-51.67, -0.47) * mm]});
            skFitSpline(sketch, "E431", {"points": [v(-51.52, 14.96) * mm, v(-51.55, 15.53) * mm, v(-51.72, 15.94) * mm, v(-52.03, 16.2) * mm]});
            skFitSpline(sketch, "E432", {"points": [v(-52.03, 16.2) * mm, v(-52.32, 16.46) * mm, v(-52.66, 16.6) * mm, v(-53.06, 16.6) * mm]});
            skFitSpline(sketch, "E433", {"points": [v(-53.06, 16.6) * mm, v(-53.38, 16.6) * mm, v(-53.72, 16.52) * mm, v(-54.08, 16.37) * mm]});
            skFitSpline(sketch, "E434", {"points": [v(-54.08, 16.37) * mm, v(-54.44, 16.24) * mm, v(-54.78, 16.03) * mm, v(-55.1, 15.77) * mm]});
            skFitSpline(sketch, "E435", {"points": [v(-55.1, 15.77) * mm, v(-55.43, 15.52) * mm, v(-55.72, 15.21) * mm, v(-55.96, 14.86) * mm]});
            skFitSpline(sketch, "E436", {"points": [v(-55.96, 14.86) * mm, v(-56.2, 14.5) * mm, v(-56.35, 14.13) * mm, v(-56.42, 13.73) * mm]});
            skFitSpline(sketch, "E437", {"points": [v(-56.42, 13.73) * mm, v(-56.42, 13.63) * mm, v(-56.34, 13.57) * mm, v(-56.19, 13.55) * mm]});
            skFitSpline(sketch, "E438", {"points": [v(-56.19, 13.55) * mm, v(-56.02, 13.55) * mm, v(-55.8, 13.57) * mm, v(-55.57, 13.6) * mm]});
            skFitSpline(sketch, "E439", {"points": [v(-55.57, 13.6) * mm, v(-55.31, 13.65) * mm, v(-55.04, 13.72) * mm, v(-54.75, 13.8) * mm]});
            skFitSpline(sketch, "E440", {"points": [v(-54.75, 13.8) * mm, v(-54.44, 13.89) * mm, v(-54.13, 13.97) * mm, v(-53.83, 14.06) * mm]});
            skFitSpline(sketch, "E441", {"points": [v(-53.39, 14.18) * mm, v(-52.88, 14.33) * mm, v(-52.43, 14.48) * mm, v(-52.05, 14.61) * mm]});
            skFitSpline(sketch, "E442", {"points": [v(-52.05, 14.61) * mm, v(-51.68, 14.74) * mm, v(-51.5, 14.85) * mm, v(-51.52, 14.94) * mm]});
            skFitSpline(sketch, "E443", {"points": [v(-23.94, 2.92) * mm, v(-23.97, 2.87) * mm, v(-24.07, 2.82) * mm, v(-24.24, 2.77) * mm]});
            skFitSpline(sketch, "E444", {"points": [v(-24.24, 2.77) * mm, v(-24.4, 2.72) * mm, v(-24.5, 2.7) * mm, v(-24.58, 2.7) * mm]});
            skFitSpline(sketch, "E445", {"points": [v(-24.58, 2.7) * mm, v(-24.78, 2.7) * mm, v(-24.96, 2.8) * mm, v(-25.12, 3) * mm]});
            skFitSpline(sketch, "E446", {"points": [v(-25.12, 3) * mm, v(-25.05, 3.18) * mm, v(-25, 3.35) * mm, v(-24.99, 3.5) * mm]});
            skFitSpline(sketch, "E447", {"points": [v(-24.99, 3.5) * mm, v(-24.95, 3.66) * mm, v(-24.92, 3.84) * mm, v(-24.89, 4.03) * mm]});
            skFitSpline(sketch, "E448", {"points": [v(-24.89, 4.03) * mm, v(-24.87, 4.44) * mm, v(-24.9, 4.88) * mm, v(-24.99, 5.33) * mm]});
            skFitSpline(sketch, "E449", {"points": [v(-24.99, 5.33) * mm, v(-25.06, 5.8) * mm, v(-25.2, 6.22) * mm, v(-25.4, 6.59) * mm]});
            skFitSpline(sketch, "E450", {"points": [v(-25.4, 6.59) * mm, v(-25.6, 6.96) * mm, v(-25.87, 7.26) * mm, v(-26.2, 7.5) * mm]});
            skFitSpline(sketch, "E451", {"points": [v(-26.2, 7.5) * mm, v(-26.52, 7.75) * mm, v(-26.91, 7.87) * mm, v(-27.38, 7.87) * mm]});
            skFitSpline(sketch, "E452", {"points": [v(-27.38, 7.87) * mm, v(-27.97, 7.87) * mm, v(-28.58, 7.64) * mm, v(-29.2, 7.17) * mm]});
            skFitSpline(sketch, "E453", {"points": [v(-29.2, 7.17) * mm, v(-29.81, 6.72) * mm, v(-30.4, 6.12) * mm, v(-30.97, 5.38) * mm]});
            skFitSpline(sketch, "E454", {"points": [v(-30.97, 5.38) * mm, v(-31.53, 4.66) * mm, v(-32.06, 3.85) * mm, v(-32.56, 2.94) * mm]});
            skFitSpline(sketch, "E455", {"points": [v(-32.56, 2.94) * mm, v(-33.05, 2.04) * mm, v(-33.5, 1.13) * mm, v(-33.9, 0.23) * mm]});
            skFitSpline(sketch, "E456", {"points": [v(-33.9, 0.23) * mm, v(-34.27, -0.66) * mm, v(-34.58, -1.5) * mm, v(-34.82, -2.29) * mm]});
            skFitSpline(sketch, "E457", {"points": [v(-34.82, -2.29) * mm, v(-35.06, -3.07) * mm, v(-35.2, -3.71) * mm, v(-35.23, -4.2) * mm]});
            skFitSpline(sketch, "E458", {"points": [v(-35.23, -4.2) * mm, v(-35.24, -4.43) * mm, v(-35.25, -4.68) * mm, v(-35.25, -4.95) * mm]});
            skFitSpline(sketch, "E459", {"points": [v(-35.25, -4.95) * mm, v(-35.24, -5.22) * mm, v(-35.18, -5.47) * mm, v(-35.1, -5.7) * mm]});
            skFitSpline(sketch, "E460", {"points": [v(-35.1, -5.7) * mm, v(-35.01, -5.92) * mm, v(-34.89, -6.1) * mm, v(-34.71, -6.26) * mm]});
            skFitSpline(sketch, "E461", {"points": [v(-34.71, -6.26) * mm, v(-34.54, -6.4) * mm, v(-34.3, -6.46) * mm, v(-34, -6.46) * mm]});
            skFitSpline(sketch, "E462", {"points": [v(-34, -6.46) * mm, v(-33.47, -6.46) * mm, v(-32.9, -6.2) * mm, v(-32.33, -5.68) * mm]});
            skFitSpline(sketch, "E463", {"points": [v(-32.33, -5.68) * mm, v(-31.73, -5.14) * mm, v(-31.16, -4.5) * mm, v(-30.6, -3.74) * mm]});
            skFitSpline(sketch, "E464", {"points": [v(-30.6, -3.74) * mm, v(-30.04, -2.99) * mm, v(-29.52, -2.2) * mm, v(-29.04, -1.38) * mm]});
            skFitSpline(sketch, "E465", {"points": [v(-29.04, -1.38) * mm, v(-28.56, -0.54) * mm, v(-28.16, 0.19) * mm, v(-27.84, 0.8) * mm]});
            skFitSpline(sketch, "E466", {"points": [v(-27.84, 0.8) * mm, v(-27.79, 1) * mm, v(-27.7, 1.2) * mm, v(-27.6, 1.46) * mm]});
            skFitSpline(sketch, "E467", {"points": [v(-27.6, 1.46) * mm, v(-27.49, 1.71) * mm, v(-27.44, 1.99) * mm, v(-27.48, 2.3) * mm]});
            skFitSpline(sketch, "E468", {"points": [v(-27.48, 2.3) * mm, v(-27.51, 2.53) * mm, v(-27.42, 2.68) * mm, v(-27.2, 2.74) * mm]});
            skFitSpline(sketch, "E469", {"points": [v(-27.2, 2.74) * mm, v(-26.97, 2.83) * mm, v(-26.73, 2.88) * mm, v(-26.48, 2.9) * mm]});
            skFitSpline(sketch, "E470", {"points": [v(-26.48, 2.9) * mm, v(-25.47, 2.8) * mm, v(-24.77, 2.58) * mm, v(-24.37, 2.19) * mm]});
            skFitSpline(sketch, "E471", {"points": [v(-24.37, 2.19) * mm, v(-23.96, 1.82) * mm, v(-23.73, 1.38) * mm, v(-23.68, 0.86) * mm]});
            skFitSpline(sketch, "E472", {"points": [v(-23.68, 0.86) * mm, v(-23.63, 0.32) * mm, v(-23.69, -0.26) * mm, v(-23.86, -0.88) * mm]});
            skFitSpline(sketch, "E473", {"points": [v(-23.86, -0.88) * mm, v(-24.01, -1.5) * mm, v(-24.13, -2.08) * mm, v(-24.22, -2.61) * mm]});
            skFitSpline(sketch, "E474", {"points": [v(-24.22, -2.61) * mm, v(-24.24, -2.73) * mm, v(-24.27, -2.92) * mm, v(-24.32, -3.2) * mm]});
            skFitSpline(sketch, "E475", {"points": [v(-24.32, -3.2) * mm, v(-24.36, -3.46) * mm, v(-24.4, -3.75) * mm, v(-24.42, -4.07) * mm]});
            skFitSpline(sketch, "E476", {"points": [v(-24.42, -4.07) * mm, v(-24.46, -4.39) * mm, v(-24.48, -4.72) * mm, v(-24.5, -5.05) * mm]});
            skFitSpline(sketch, "E477", {"points": [v(-24.5, -5.05) * mm, v(-24.52, -5.37) * mm, v(-24.5, -5.64) * mm, v(-24.48, -5.86) * mm]});
            skFitSpline(sketch, "E478", {"points": [v(-24.48, -5.86) * mm, v(-24.42, -6.07) * mm, v(-24.35, -6.22) * mm, v(-24.24, -6.28) * mm]});
            skFitSpline(sketch, "E479", {"points": [v(-24.24, -6.28) * mm, v(-24.12, -6.35) * mm, v(-23.95, -6.3) * mm, v(-23.73, -6.1) * mm]});
            skFitSpline(sketch, "E480", {"points": [v(-23.73, -6.1) * mm, v(-23.32, -5.7) * mm, v(-22.88, -5.19) * mm, v(-22.42, -4.55) * mm]});
            skFitSpline(sketch, "E481", {"points": [v(-22.42, -4.55) * mm, v(-21.96, -3.9) * mm, v(-21.5, -3.2) * mm, v(-21.06, -2.49) * mm]});
            skFitSpline(sketch, "E482", {"points": [v(-21.06, -2.49) * mm, v(-20.6, -1.75) * mm, v(-20.16, -1.01) * mm, v(-19.75, -0.27) * mm]});
            skFitSpline(sketch, "E483", {"points": [v(-19.75, -0.27) * mm, v(-19.33, 0.48) * mm, v(-18.94, 1.17) * mm, v(-18.6, 1.79) * mm]});
            skFitSpline(sketch, "E484", {"points": [v(-18.6, 1.79) * mm, v(-18.42, 2.16) * mm, v(-18.25, 2.52) * mm, v(-18.07, 2.85) * mm]});
            skFitSpline(sketch, "E485", {"points": [v(93.67, -5.32) * mm, v(93.63, -5.37) * mm, v(93.58, -5.41) * mm, v(93.54, -5.45) * mm]});
            skFitSpline(sketch, "E486", {"points": [v(-18.89, -1.17) * mm, v(-19.18, -1.71) * mm, v(-19.5, -2.26) * mm, v(-19.83, -2.81) * mm]});
            skFitSpline(sketch, "E487", {"points": [v(-19.83, -2.81) * mm, v(-20.24, -3.52) * mm, v(-20.66, -4.19) * mm, v(-21.09, -4.82) * mm]});
            skFitSpline(sketch, "E488", {"points": [v(-21.09, -4.82) * mm, v(-21.5, -5.46) * mm, v(-21.93, -6.05) * mm, v(-22.37, -6.58) * mm]});
            skFitSpline(sketch, "E489", {"points": [v(-22.37, -6.58) * mm, v(-22.8, -7.1) * mm, v(-23.2, -7.52) * mm, v(-23.6, -7.84) * mm]});
            skFitSpline(sketch, "E490", {"points": [v(-23.6, -7.84) * mm, v(-23.95, -8.13) * mm, v(-24.36, -8.36) * mm, v(-24.83, -8.55) * mm]});
            skFitSpline(sketch, "E491", {"points": [v(-24.83, -8.55) * mm, v(-25.31, -8.73) * mm, v(-25.78, -8.82) * mm, v(-26.25, -8.82) * mm]});
            skFitSpline(sketch, "E492", {"points": [v(-26.25, -8.82) * mm, v(-26.86, -8.82) * mm, v(-27.34, -8.61) * mm, v(-27.68, -8.2) * mm]});
            skFitSpline(sketch, "E493", {"points": [v(-27.68, -8.2) * mm, v(-28.03, -7.76) * mm, v(-28.28, -7.25) * mm, v(-28.45, -6.66) * mm]});
            skFitSpline(sketch, "E494", {"points": [v(-28.45, -6.66) * mm, v(-28.6, -6.06) * mm, v(-28.7, -5.44) * mm, v(-28.7, -4.8) * mm]});
            skFitSpline(sketch, "E495", {"points": [v(-28.7, -4.8) * mm, v(-28.73, -4.16) * mm, v(-28.7, -3.63) * mm, v(-28.63, -3.22) * mm]});
            skFitSpline(sketch, "E496", {"points": [v(-28.63, -3.22) * mm, v(-28.63, -3.18) * mm, v(-28.63, -3.17) * mm]});
            skFitSpline(sketch, "E497", {"points": [v(-28.63, -3.17) * mm, v(-28.63, -3.15) * mm, v(-28.62, -3.08) * mm, v(-28.6, -2.96) * mm]});
            skFitSpline(sketch, "E498", {"points": [v(-28.6, -2.96) * mm, v(-29.07, -3.72) * mm, v(-29.58, -4.46) * mm, v(-30.15, -5.18) * mm]});
            skFitSpline(sketch, "E499", {"points": [v(-30.15, -5.18) * mm, v(-30.7, -5.88) * mm, v(-31.28, -6.5) * mm, v(-31.92, -7.06) * mm]});
            skFitSpline(sketch, "E500", {"points": [v(-31.92, -7.06) * mm, v(-32.53, -7.62) * mm, v(-33.18, -8.07) * mm, v(-33.87, -8.42) * mm]});
            skFitSpline(sketch, "E501", {"points": [v(-33.87, -8.42) * mm, v(-34.55, -8.76) * mm, v(-35.25, -8.92) * mm, v(-35.97, -8.92) * mm]});
            skFitSpline(sketch, "E502", {"points": [v(-35.97, -8.92) * mm, v(-36.64, -8.92) * mm, v(-37.2, -8.8) * mm, v(-37.66, -8.57) * mm]});
            skFitSpline(sketch, "E503", {"points": [v(-37.66, -8.57) * mm, v(-38.13, -8.34) * mm, v(-38.5, -8.03) * mm, v(-38.77, -7.64) * mm]});
            skFitSpline(sketch, "E504", {"points": [v(-38.77, -7.64) * mm, v(-39.04, -7.26) * mm, v(-39.24, -6.8) * mm, v(-39.36, -6.28) * mm]});
            skFitSpline(sketch, "E505", {"points": [v(-39.36, -6.28) * mm, v(-39.48, -5.76) * mm, v(-39.54, -5.22) * mm, v(-39.54, -4.65) * mm]});
            skFitSpline(sketch, "E506", {"points": [v(-39.54, -4.65) * mm, v(-39.54, -4.55) * mm, v(-39.54, -4.43) * mm, v(-39.54, -4.3) * mm]});
            skFitSpline(sketch, "E507", {"points": [v(-39.54, -4.3) * mm, v(-39.54, -4.16) * mm, v(-39.53, -4.04) * mm, v(-39.51, -3.92) * mm]});
            skFitSpline(sketch, "E508", {"points": [v(-39.51, -3.92) * mm, v(-39.4, -3.08) * mm, v(-39.19, -2.15) * mm, v(-38.85, -1.13) * mm]});
            skFitSpline(sketch, "E509", {"points": [v(-38.85, -1.13) * mm, v(-38.52, -0.1) * mm, v(-38.1, 0.92) * mm, v(-37.59, 1.96) * mm]});
            skFitSpline(sketch, "E510", {"points": [v(-37.59, 1.96) * mm, v(-37.06, 3.02) * mm, v(-36.45, 4.04) * mm, v(-35.77, 5.03) * mm]});
            skFitSpline(sketch, "E511", {"points": [v(-35.77, 5.03) * mm, v(-35.08, 6.02) * mm, v(-34.34, 6.9) * mm, v(-33.53, 7.65) * mm]});
            skFitSpline(sketch, "E512", {"points": [v(-33.53, 7.65) * mm, v(-32.71, 8.42) * mm, v(-31.85, 9.03) * mm, v(-30.94, 9.48) * mm]});
            skFitSpline(sketch, "E513", {"points": [v(-30.94, 9.48) * mm, v(-30.04, 9.95) * mm, v(-29.1, 10.19) * mm, v(-28.12, 10.19) * mm]});
            skFitSpline(sketch, "E514", {"points": [v(-28.12, 10.19) * mm, v(-27.37, 10.19) * mm, v(-26.7, 10) * mm, v(-26.12, 9.66) * mm]});
            skFitSpline(sketch, "E515", {"points": [v(-26.12, 9.66) * mm, v(-25.54, 9.3) * mm, v(-25.05, 8.84) * mm, v(-24.66, 8.27) * mm]});
            skFitSpline(sketch, "E516", {"points": [v(-24.66, 8.27) * mm, v(-24.26, 7.72) * mm, v(-23.98, 7.1) * mm, v(-23.8, 6.39) * mm]});
            skFitSpline(sketch, "E517", {"points": [v(-23.8, 6.39) * mm, v(-23.62, 5.7) * mm, v(-23.55, 5) * mm, v(-23.6, 4.3) * mm]});
            skFitSpline(sketch, "E518", {"points": [v(-23.6, 4.3) * mm, v(-23.65, 3.82) * mm, v(-23.76, 3.36) * mm, v(-23.91, 2.94) * mm]});
            skFitSpline(sketch, "E519", {"points": [v(0.4, 3.75) * mm, v(0.45, 3.8) * mm, v(0.5, 3.85) * mm, v(0.55, 3.89) * mm]});
            skFitSpline(sketch, "E520", {"points": [v(0.2, 1.15) * mm, v(0.08, 0.97) * mm, v(-0.04, 0.79) * mm, v(-0.16, 0.6) * mm]});
            skFitSpline(sketch, "E521", {"points": [v(-0.16, 0.6) * mm, v(-0.9, -0.52) * mm, v(-1.78, -1.65) * mm, v(-2.8, -2.79) * mm]});
            skFitSpline(sketch, "E522", {"points": [v(-2.8, -2.79) * mm, v(-3.82, -3.91) * mm, v(-4.94, -4.98) * mm, v(-6.2, -6) * mm]});
            skFitSpline(sketch, "E523", {"points": [v(-6.2, -6) * mm, v(-7.44, -7.01) * mm, v(-8.74, -7.83) * mm, v(-10.1, -8.45) * mm]});
            skFitSpline(sketch, "E524", {"points": [v(-10.1, -8.45) * mm, v(-10.8, -8.76) * mm, v(-11.57, -9.06) * mm, v(-12.43, -9.33) * mm]});
            skFitSpline(sketch, "E525", {"points": [v(-12.43, -9.33) * mm, v(-12.65, -9.4) * mm, v(-12.88, -9.46) * mm, v(-13.1, -9.51) * mm]});
            skFitSpline(sketch, "E526", {"points": [v(-16.4, -9.52) * mm, v(-17.3, -9.24) * mm, v(-18.03, -8.73) * mm, v(-18.59, -8) * mm]});
            skFitSpline(sketch, "E527", {"points": [v(-18.59, -8) * mm, v(-19.17, -7.19) * mm, v(-19.43, -6.13) * mm, v(-19.36, -4.82) * mm]});
            skFitSpline(sketch, "E528", {"points": [v(-19.36, -4.82) * mm, v(-19.34, -4.09) * mm, v(-19.24, -3.17) * mm, v(-19.05, -2.08) * mm]});
            skFitSpline(sketch, "E529", {"points": [v(-19.05, -2.08) * mm, v(-19, -1.79) * mm, v(-18.94, -1.48) * mm, v(-18.89, -1.17) * mm]});
            skFitSpline(sketch, "E530", {"points": [v(-18.07, 2.85) * mm, v(-17.89, 3.68) * mm, v(-17.7, 4.52) * mm, v(-17.48, 5.38) * mm]});
            skFitSpline(sketch, "E531", {"points": [v(-17.48, 5.38) * mm, v(-17.14, 6.74) * mm, v(-16.82, 8.06) * mm, v(-16.5, 9.33) * mm]});
            skFitSpline(sketch, "E532", {"points": [v(-16.5, 9.33) * mm, v(-16.3, 10.2) * mm, v(-16.1, 11.04) * mm, v(-15.92, 11.84) * mm]});
            skFitSpline(sketch, "E533", {"points": [v(-15.92, 11.84) * mm, v(-15.71, 12.67) * mm, v(-15.53, 13.41) * mm, v(-15.38, 14.08) * mm]});
            skFitSpline(sketch, "E534", {"points": [v(-15.38, 14.08) * mm, v(-15.23, 14.77) * mm, v(-15.1, 15.37) * mm, v(-15, 15.9) * mm]});
            skFitSpline(sketch, "E535", {"points": [v(-15, 15.9) * mm, v(-14.9, 16.41) * mm, v(-14.82, 16.83) * mm, v(-14.79, 17.15) * mm]});
            skFitSpline(sketch, "E536", {"points": [v(-14.79, 17.15) * mm, v(-14.77, 17.43) * mm, v(-14.78, 17.68) * mm, v(-14.82, 17.88) * mm]});
            skFitSpline(sketch, "E537", {"points": [v(-14.82, 17.88) * mm, v(-14.83, 18.08) * mm, v(-14.86, 18.26) * mm, v(-14.9, 18.4) * mm]});
            skFitSpline(sketch, "E538", {"points": [v(-14.9, 18.4) * mm, v(-14.9, 18.5) * mm, v(-14.93, 18.57) * mm, v(-14.94, 18.63) * mm]});
            skFitSpline(sketch, "E539", {"points": [v(-14.94, 18.63) * mm, v(-14.94, 18.72) * mm, v(-14.94, 18.8) * mm, v(-14.94, 18.86) * mm]});
            skFitSpline(sketch, "E540", {"points": [v(-14.94, 18.86) * mm, v(-14.93, 19.1) * mm, v(-14.83, 19.24) * mm, v(-14.66, 19.31) * mm]});
            skFitSpline(sketch, "E541", {"points": [v(-14.66, 19.31) * mm, v(-14.47, 19.4) * mm, v(-14.26, 19.44) * mm, v(-14.02, 19.44) * mm]});
            skFitSpline(sketch, "E542", {"points": [v(-14.02, 19.44) * mm, v(-13.35, 19.44) * mm, v(-12.82, 19.34) * mm, v(-12.43, 19.14) * mm]});
            skFitSpline(sketch, "E543", {"points": [v(-12.43, 19.14) * mm, v(-12.02, 18.93) * mm, v(-11.71, 18.67) * mm, v(-11.5, 18.33) * mm]});
            skFitSpline(sketch, "E544", {"points": [v(-11.5, 18.33) * mm, v(-11.28, 18.01) * mm, v(-11.15, 17.64) * mm, v(-11.1, 17.22) * mm]});
            skFitSpline(sketch, "E545", {"points": [v(-11.1, 17.22) * mm, v(-11.04, 16.8) * mm, v(-11.03, 16.38) * mm, v(-11.07, 15.94) * mm]});
            skFitSpline(sketch, "E546", {"points": [v(-11.07, 15.94) * mm, v(-11.14, 15.26) * mm, v(-11.26, 14.5) * mm, v(-11.43, 13.65) * mm]});
            skFitSpline(sketch, "E547", {"points": [v(-11.43, 13.65) * mm, v(-11.58, 12.83) * mm, v(-11.77, 11.96) * mm, v(-12, 11.04) * mm]});
            skFitSpline(sketch, "E548", {"points": [v(-12, 11.04) * mm, v(-12.2, 10.13) * mm, v(-12.43, 9.2) * mm, v(-12.69, 8.22) * mm]});
            skFitSpline(sketch, "E549", {"points": [v(-12.69, 8.22) * mm, v(-12.93, 7.27) * mm, v(-13.17, 6.32) * mm, v(-13.43, 5.38) * mm]});
            skFitSpline(sketch, "E550", {"points": [v(-13.43, 5.38) * mm, v(-13.46, 5.27) * mm, v(-13.49, 5.17) * mm, v(-13.5, 5.1) * mm]});
            skFitSpline(sketch, "E551", {"points": [v(-13.5, 5.1) * mm, v(-13.52, 5.06) * mm, v(-13.54, 5) * mm, v(-13.56, 4.93) * mm]});
            skFitSpline(sketch, "E552", {"points": [v(-13.56, 4.93) * mm, v(-13.58, 4.88) * mm, v(-13.6, 4.81) * mm, v(-13.6, 4.73) * mm]});
            skFitSpline(sketch, "E553", {"points": [v(-13.6, 4.73) * mm, v(-13.63, 4.66) * mm, v(-13.65, 4.57) * mm, v(-13.69, 4.45) * mm]});
            skFitSpline(sketch, "E554", {"points": [v(-13.69, 4.45) * mm, v(-13.24, 5.1) * mm, v(-12.76, 5.73) * mm, v(-12.25, 6.31) * mm]});
            skFitSpline(sketch, "E555", {"points": [v(-12.25, 6.31) * mm, v(-11.74, 6.9) * mm, v(-11.2, 7.41) * mm, v(-10.63, 7.85) * mm]});
            skFitSpline(sketch, "E556", {"points": [v(-10.63, 7.85) * mm, v(-10.07, 8.3) * mm, v(-9.49, 8.65) * mm, v(-8.89, 8.9) * mm]});
            skFitSpline(sketch, "E557", {"points": [v(-8.89, 8.9) * mm, v(-8.27, 9.17) * mm, v(-7.65, 9.3) * mm, v(-7.01, 9.3) * mm]});
            skFitSpline(sketch, "E558", {"points": [v(-7.01, 9.3) * mm, v(-6.35, 9.3) * mm, v(-5.78, 9.19) * mm, v(-5.32, 8.95) * mm]});
            skFitSpline(sketch, "E559", {"points": [v(-5.32, 8.95) * mm, v(-4.86, 8.74) * mm, v(-4.5, 8.43) * mm, v(-4.22, 8.05) * mm]});
            skFitSpline(sketch, "E560", {"points": [v(-4.22, 8.05) * mm, v(-3.93, 7.68) * mm, v(-3.72, 7.24) * mm, v(-3.6, 6.72) * mm]});
            skFitSpline(sketch, "E561", {"points": [v(-3.6, 6.72) * mm, v(-3.48, 6.21) * mm, v(-3.42, 5.68) * mm, v(-3.42, 5.13) * mm]});
            skFitSpline(sketch, "E562", {"points": [v(-3.42, 5.13) * mm, v(-3.42, 5) * mm, v(-3.43, 4.85) * mm, v(-3.45, 4.7) * mm]});
            skFitSpline(sketch, "E563", {"points": [v(-3.45, 4.7) * mm, v(-3.45, 4.57) * mm, v(-3.46, 4.44) * mm, v(-3.47, 4.3) * mm]});
            skFitSpline(sketch, "E564", {"points": [v(-3.47, 4.3) * mm, v(-3.54, 3.63) * mm, v(-3.7, 2.87) * mm, v(-3.96, 2.01) * mm]});
            skFitSpline(sketch, "E565", {"points": [v(-3.96, 2.01) * mm, v(-4.2, 1.18) * mm, v(-4.52, 0.3) * mm, v(-4.91, -0.6) * mm]});
            skFitSpline(sketch, "E566", {"points": [v(-4.91, -0.6) * mm, v(-5.3, -1.49) * mm, v(-5.76, -2.38) * mm, v(-6.27, -3.27) * mm]});
            skFitSpline(sketch, "E567", {"points": [v(-6.27, -3.27) * mm, v(-6.78, -4.15) * mm, v(-7.34, -4.98) * mm, v(-7.94, -5.73) * mm]});
            skFitSpline(sketch, "E568", {"points": [v(-7.94, -5.73) * mm, v(-7.15, -5.16) * mm, v(-6.36, -4.52) * mm, v(-5.58, -3.82) * mm]});
            skFitSpline(sketch, "E569", {"points": [v(-5.58, -3.82) * mm, v(-4.77, -3.1) * mm, v(-4.01, -2.34) * mm, v(-3.3, -1.53) * mm]});
            skFitSpline(sketch, "E570", {"points": [v(-3.3, -1.53) * mm, v(-2.56, -0.73) * mm, v(-1.88, 0.11) * mm, v(-1.27, 0.98) * mm]});
            skFitSpline(sketch, "E571", {"points": [v(-1.27, 0.98) * mm, v(-0.63, 1.87) * mm, v(-0.09, 2.78) * mm, v(0.38, 3.72) * mm]});
            skFitSpline(sketch, "E572", {"points": [v(-9, 6.84) * mm, v(-9.49, 6.84) * mm, v(-10, 6.62) * mm, v(-10.53, 6.19) * mm]});
            skFitSpline(sketch, "E573", {"points": [v(-10.53, 6.19) * mm, v(-11.04, 5.77) * mm, v(-11.56, 5.24) * mm, v(-12.07, 4.6) * mm]});
            skFitSpline(sketch, "E574", {"points": [v(-12.07, 4.6) * mm, v(-12.57, 3.97) * mm, v(-13.04, 3.28) * mm, v(-13.5, 2.54) * mm]});
            skFitSpline(sketch, "E575", {"points": [v(-13.5, 2.54) * mm, v(-13.97, 1.8) * mm, v(-14.37, 1.12) * mm, v(-14.71, 0.48) * mm]});
            skFitSpline(sketch, "E576", {"points": [v(-14.84, -0.1) * mm, v(-14.94, -0.45) * mm, v(-15.05, -0.87) * mm, v(-15.17, -1.36) * mm]});
            skFitSpline(sketch, "E577", {"points": [v(-15.17, -1.36) * mm, v(-15.3, -1.84) * mm, v(-15.4, -2.34) * mm, v(-15.5, -2.86) * mm]});
            skFitSpline(sketch, "E578", {"points": [v(-15.5, -2.86) * mm, v(-15.61, -3.37) * mm, v(-15.7, -3.88) * mm, v(-15.8, -4.4) * mm]});
            skFitSpline(sketch, "E579", {"points": [v(-15.8, -4.4) * mm, v(-15.86, -4.9) * mm, v(-15.9, -5.36) * mm, v(-15.9, -5.78) * mm]});
            skFitSpline(sketch, "E580", {"points": [v(-15.9, -5.78) * mm, v(-15.9, -6.25) * mm, v(-15.84, -6.64) * mm, v(-15.74, -6.94) * mm]});
            skFitSpline(sketch, "E581", {"points": [v(-15.74, -6.94) * mm, v(-15.64, -7.22) * mm, v(-15.44, -7.36) * mm, v(-15.15, -7.36) * mm]});
            skFitSpline(sketch, "E582", {"points": [v(-15.15, -7.36) * mm, v(-14.94, -7.36) * mm, v(-14.7, -7.29) * mm, v(-14.4, -7.14) * mm]});
            skFitSpline(sketch, "E583", {"points": [v(-14.4, -7.14) * mm, v(-13.86, -6.87) * mm, v(-13.33, -6.45) * mm, v(-12.81, -5.88) * mm]});
            skFitSpline(sketch, "E584", {"points": [v(-12.81, -5.88) * mm, v(-12.28, -5.31) * mm, v(-11.78, -4.67) * mm, v(-11.3, -3.94) * mm]});
            skFitSpline(sketch, "E585", {"points": [v(-11.3, -3.94) * mm, v(-10.82, -3.22) * mm, v(-10.38, -2.45) * mm, v(-9.97, -1.63) * mm]});
            skFitSpline(sketch, "E586", {"points": [v(-9.97, -1.63) * mm, v(-9.55, -0.81) * mm, v(-9.2, -0.01) * mm, v(-8.89, 0.76) * mm]});
            skFitSpline(sketch, "E587", {"points": [v(-8.89, 0.76) * mm, v(-8.58, 1.53) * mm, v(-8.33, 2.25) * mm, v(-8.14, 2.92) * mm]});
            skFitSpline(sketch, "E588", {"points": [v(-8.14, 2.92) * mm, v(-7.94, 3.59) * mm, v(-7.82, 4.14) * mm, v(-7.78, 4.58) * mm]});
            skFitSpline(sketch, "E589", {"points": [v(-7.78, 4.58) * mm, v(-7.77, 4.81) * mm, v(-7.77, 5.06) * mm, v(-7.78, 5.33) * mm]});
            skFitSpline(sketch, "E590", {"points": [v(-7.78, 5.33) * mm, v(-7.78, 5.6) * mm, v(-7.83, 5.84) * mm, v(-7.91, 6.06) * mm]});
            skFitSpline(sketch, "E591", {"points": [v(-7.91, 6.06) * mm, v(-7.98, 6.3) * mm, v(-8.1, 6.48) * mm, v(-8.27, 6.61) * mm]});
            skFitSpline(sketch, "E592", {"points": [v(-8.27, 6.61) * mm, v(-8.44, 6.77) * mm, v(-8.68, 6.84) * mm, v(-9, 6.84) * mm]});
            skFitSpline(sketch, "E593", {"points": [v(4.87, -20.97) * mm, v(3.97, -20.97) * mm, v(3.12, -20.82) * mm, v(2.33, -20.54) * mm]});
            skFitSpline(sketch, "E594", {"points": [v(2.33, -20.54) * mm, v(1.54, -20.25) * mm, v(0.85, -19.82) * mm, v(0.25, -19.23) * mm]});
            skFitSpline(sketch, "E595", {"points": [v(0.25, -19.23) * mm, v(-0.35, -18.64) * mm, v(-0.82, -17.9) * mm, v(-1.18, -17.02) * mm]});
            skFitSpline(sketch, "E596", {"points": [v(-1.18, -17.02) * mm, v(-1.54, -16.15) * mm, v(-1.73, -15.12) * mm, v(-1.75, -13.93) * mm]});
            skFitSpline(sketch, "E597", {"points": [v(-1.75, -13.93) * mm, v(-4.2, -13.22) * mm, v(-6.96, -12.87) * mm, v(-10.04, -12.87) * mm]});
            skFitSpline(sketch, "E598", {"points": [v(-10.04, -12.87) * mm, v(-11.32, -12.87) * mm, v(-12.65, -12.92) * mm, v(-14.01, -13.02) * mm]});
            skFitSpline(sketch, "E599", {"points": [v(-14.01, -13.02) * mm, v(-15.4, -13.14) * mm, v(-16.83, -13.3) * mm, v(-18.3, -13.52) * mm]});
            skFitSpline(sketch, "E600", {"points": [v(-18.3, -13.52) * mm, v(-20.34, -13.83) * mm, v(-22.33, -14.25) * mm, v(-24.28, -14.8) * mm]});
            skFitSpline(sketch, "E601", {"points": [v(-24.28, -14.8) * mm, v(-26.23, -15.38) * mm, v(-28.03, -16.09) * mm, v(-29.7, -16.94) * mm]});
            skFitSpline(sketch, "E602", {"points": [v(-29.7, -16.94) * mm, v(-31.37, -17.8) * mm, v(-32.85, -18.81) * mm, v(-34.13, -19.99) * mm]});
            skFitSpline(sketch, "E603", {"points": [v(-34.13, -19.99) * mm, v(-35.43, -21.16) * mm, v(-36.44, -22.5) * mm, v(-37.16, -24) * mm]});
            skFitSpline(sketch, "E604", {"points": [v(-37.16, -24) * mm, v(-37.18, -24.04) * mm, v(-37.2, -24.08) * mm, v(-37.21, -24.13) * mm]});
            skFitSpline(sketch, "E605", {"points": [v(-37.21, -24.13) * mm, v(-37.25, -24.2) * mm, v(-37.27, -24.26) * mm, v(-37.29, -24.31) * mm]});
            skFitSpline(sketch, "E606", {"points": [v(-37.29, -24.31) * mm, v(-37.37, -24.54) * mm, v(-37.5, -24.8) * mm, v(-37.65, -25.09) * mm]});
            skFitSpline(sketch, "E607", {"points": [v(-37.65, -25.09) * mm, v(-37.8, -25.37) * mm, v(-38.03, -25.53) * mm, v(-38.34, -25.57) * mm]});
            skFitSpline(sketch, "E608", {"points": [v(-38.34, -25.57) * mm, v(-38.68, -25.55) * mm, v(-38.96, -25.36) * mm, v(-39.19, -24.99) * mm]});
            skFitSpline(sketch, "E609", {"points": [v(-39.19, -24.99) * mm, v(-39.43, -24.62) * mm, v(-39.61, -24.2) * mm, v(-39.75, -23.73) * mm]});
            skFitSpline(sketch, "E610", {"points": [v(-39.75, -23.73) * mm, v(-39.92, -23.21) * mm, v(-40, -22.64) * mm, v(-40, -22.02) * mm]});
            skFitSpline(sketch, "E611", {"points": [v(-40, -22.02) * mm, v(-40, -21.33) * mm, v(-39.89, -20.65) * mm, v(-39.65, -19.96) * mm]});
            skFitSpline(sketch, "E612", {"points": [v(-39.65, -19.96) * mm, v(-39.43, -19.3) * mm, v(-39.12, -18.64) * mm, v(-38.73, -18) * mm]});
            skFitSpline(sketch, "E613", {"points": [v(-38.73, -18) * mm, v(-38.33, -17.38) * mm, v(-37.87, -16.78) * mm, v(-37.34, -16.21) * mm]});
            skFitSpline(sketch, "E614", {"points": [v(-37.34, -16.21) * mm, v(-36.83, -15.64) * mm, v(-36.29, -15.13) * mm, v(-35.72, -14.68) * mm]});
            skFitSpline(sketch, "E615", {"points": [v(-35.72, -14.68) * mm, v(-34.73, -13.96) * mm, v(-33.6, -13.32) * mm, v(-32.31, -12.77) * mm]});
            skFitSpline(sketch, "E616", {"points": [v(-32.31, -12.77) * mm, v(-31.03, -12.22) * mm, v(-29.65, -11.74) * mm, v(-28.18, -11.34) * mm]});
            skFitSpline(sketch, "E617", {"points": [v(-28.18, -11.34) * mm, v(-26.72, -10.93) * mm, v(-25.21, -10.6) * mm, v(-23.64, -10.33) * mm]});
            skFitSpline(sketch, "E618", {"points": [v(-23.64, -10.33) * mm, v(-22.08, -10.06) * mm, v(-20.53, -9.85) * mm, v(-19, -9.7) * mm]});
            skFitSpline(sketch, "E619", {"points": [v(-19, -9.7) * mm, v(-18.17, -9.62) * mm, v(-17.34, -9.56) * mm, v(-16.5, -9.53) * mm]});
            skFitSpline(sketch, "E620", {"points": [v(-16.5, -9.53) * mm, v(-16.47, -9.53) * mm, v(-16.44, -9.53) * mm, v(-16.4, -9.52) * mm]});
            skFitSpline(sketch, "E621", {"points": [v(-13.1, -9.51) * mm, v(-11.1, -9.56) * mm, v(-9.19, -9.73) * mm, v(-7.34, -10.03) * mm]});
            skFitSpline(sketch, "E622", {"points": [v(-7.34, -10.03) * mm, v(-5.19, -10.38) * mm, v(-3.2, -10.97) * mm, v(-1.39, -11.79) * mm]});
            skFitSpline(sketch, "E623", {"points": [v(-1.39, -11.79) * mm, v(-1.12, -10.25) * mm, v(-0.8, -8.8) * mm, v(-0.44, -7.46) * mm]});
            skFitSpline(sketch, "E624", {"points": [v(-0.44, -7.46) * mm, v(-0.08, -6.12) * mm, v(0.3, -4.87) * mm, v(0.69, -3.7) * mm]});
            skFitSpline(sketch, "E625", {"points": [v(0.69, -3.7) * mm, v(1.08, -2.5) * mm, v(1.48, -1.4) * mm, v(1.9, -0.37) * mm]});
            skFitSpline(sketch, "E626", {"points": [v(1.9, -0.37) * mm, v(2.3, 0.65) * mm, v(2.7, 1.6) * mm, v(3.05, 2.5) * mm]});
            skFitSpline(sketch, "E627", {"points": [v(3.05, 2.5) * mm, v(3.19, 2.84) * mm, v(3.31, 3.19) * mm, v(3.43, 3.52) * mm]});
            skFitSpline(sketch, "E628", {"points": [v(3.43, 3.52) * mm, v(3.57, 3.87) * mm, v(3.72, 4.23) * mm, v(3.87, 4.58) * mm]});
            skFitSpline(sketch, "E629", {"points": [v(3.87, 4.58) * mm, v(3.72, 4.58) * mm, v(3.57, 4.58) * mm, v(3.43, 4.58) * mm]});
            skFitSpline(sketch, "E630", {"points": [v(3.43, 4.58) * mm, v(3.31, 4.58) * mm, v(3.2, 4.59) * mm, v(3.08, 4.6) * mm]});
            skFitSpline(sketch, "E631", {"points": [v(3.08, 4.6) * mm, v(2.94, 4.6) * mm, v(2.78, 4.6) * mm, v(2.59, 4.6) * mm]});
            skFitSpline(sketch, "E632", {"points": [v(2.59, 4.6) * mm, v(2.4, 4.62) * mm, v(2.24, 4.64) * mm, v(2.1, 4.65) * mm]});
            skFitSpline(sketch, "E633", {"points": [v(0.36, 1.1) * mm, v(0.3, 1.12) * mm, v(0.24, 1.13) * mm, v(0.2, 1.15) * mm]});
            skFitSpline(sketch, "E634", {"points": [v(0.55, 3.89) * mm, v(0.71, 4.19) * mm, v(0.87, 4.5) * mm, v(1.02, 4.8) * mm]});
            skFitSpline(sketch, "E635", {"points": [v(1.02, 4.8) * mm, v(0.39, 4.84) * mm, v(-0.14, 4.98) * mm, v(-0.57, 5.23) * mm]});
            skFitSpline(sketch, "E636", {"points": [v(-0.57, 5.23) * mm, v(-1, 5.48) * mm, v(-1.34, 5.8) * mm, v(-1.6, 6.19) * mm]});
            skFitSpline(sketch, "E637", {"points": [v(-1.6, 6.19) * mm, v(-1.85, 6.59) * mm, v(-2.02, 7.03) * mm, v(-2.1, 7.52) * mm]});
            skFitSpline(sketch, "E638", {"points": [v(-2.1, 7.52) * mm, v(-2.21, 8.02) * mm, v(-2.24, 8.53) * mm, v(-2.18, 9.05) * mm]});
            skFitSpline(sketch, "E639", {"points": [v(-2.18, 9.05) * mm, v(-2.13, 9.62) * mm, v(-1.99, 10.2) * mm, v(-1.75, 10.76) * mm]});
            skFitSpline(sketch, "E640", {"points": [v(-1.75, 10.76) * mm, v(-1.53, 11.35) * mm, v(-1.22, 11.87) * mm, v(-0.82, 12.32) * mm]});
            skFitSpline(sketch, "E641", {"points": [v(-0.82, 12.32) * mm, v(-0.43, 12.8) * mm, v(0.02, 13.17) * mm, v(0.54, 13.45) * mm]});
            skFitSpline(sketch, "E642", {"points": [v(0.54, 13.45) * mm, v(1.07, 13.74) * mm, v(1.66, 13.88) * mm, v(2.3, 13.88) * mm]});
            skFitSpline(sketch, "E643", {"points": [v(2.3, 13.88) * mm, v(3.02, 13.88) * mm, v(3.55, 13.65) * mm, v(3.87, 13.2) * mm]});
            skFitSpline(sketch, "E644", {"points": [v(3.87, 13.2) * mm, v(4.21, 12.77) * mm, v(4.36, 12.13) * mm, v(4.3, 11.3) * mm]});
            skFitSpline(sketch, "E645", {"points": [v(4.3, 11.3) * mm, v(4.26, 10.87) * mm, v(4.17, 10.43) * mm, v(4.05, 9.96) * mm]});
            skFitSpline(sketch, "E646", {"points": [v(4.05, 9.96) * mm, v(3.95, 9.5) * mm, v(3.83, 9.06) * mm, v(3.7, 8.63) * mm]});
            skFitSpline(sketch, "E647", {"points": [v(3.7, 8.63) * mm, v(3.57, 8.2) * mm, v(3.44, 7.79) * mm, v(3.3, 7.42) * mm]});
            skFitSpline(sketch, "E648", {"points": [v(3.3, 7.42) * mm, v(3.17, 7.05) * mm, v(3.06, 6.75) * mm, v(2.97, 6.51) * mm]});
            skFitSpline(sketch, "E649", {"points": [v(2.97, 6.51) * mm, v(2.94, 6.46) * mm, v(2.92, 6.42) * mm, v(2.92, 6.39) * mm]});
            skFitSpline(sketch, "E650", {"points": [v(2.92, 6.39) * mm, v(2.92, 6.36) * mm, v(2.9, 6.3) * mm, v(2.87, 6.24) * mm]});
            skFitSpline(sketch, "E651", {"points": [v(2.87, 6.24) * mm, v(3.06, 6.2) * mm, v(3.27, 6.18) * mm, v(3.51, 6.16) * mm]});
            skFitSpline(sketch, "E652", {"points": [v(3.51, 6.16) * mm, v(3.77, 6.15) * mm, v(4.02, 6.14) * mm, v(4.26, 6.14) * mm]});
            skFitSpline(sketch, "E653", {"points": [v(4.26, 6.14) * mm, v(4.4, 6.14) * mm, v(4.53, 6.14) * mm, v(4.67, 6.14) * mm]});
            skFitSpline(sketch, "E654", {"points": [v(4.67, 6.14) * mm, v(4.82, 6.15) * mm, v(4.97, 6.16) * mm, v(5.13, 6.16) * mm]});
            skFitSpline(sketch, "E655", {"points": [v(5.13, 6.16) * mm, v(5.27, 6.16) * mm, v(5.4, 6.16) * mm, v(5.54, 6.16) * mm]});
            skFitSpline(sketch, "E656", {"points": [v(5.54, 6.16) * mm, v(5.68, 6.18) * mm, v(5.8, 6.19) * mm, v(5.92, 6.19) * mm]});
            skFitSpline(sketch, "E657", {"points": [v(5.92, 6.19) * mm, v(6.23, 6.19) * mm, v(6.51, 6.17) * mm, v(6.77, 6.14) * mm]});
            skFitSpline(sketch, "E658", {"points": [v(6.77, 6.14) * mm, v(7.03, 6.12) * mm, v(7.26, 6.07) * mm, v(7.46, 5.99) * mm]});
            skFitSpline(sketch, "E659", {"points": [v(7.46, 5.99) * mm, v(7.9, 5.8) * mm, v(8.1, 5.37) * mm, v(8.1, 4.68) * mm]});
            skFitSpline(sketch, "E660", {"points": [v(8.1, 4.68) * mm, v(8.1, 4.28) * mm, v(8.04, 3.8) * mm, v(7.9, 3.27) * mm]});
            skFitSpline(sketch, "E661", {"points": [v(7.9, 3.27) * mm, v(7.76, 2.75) * mm, v(7.6, 2.22) * mm, v(7.41, 1.66) * mm]});
            skFitSpline(sketch, "E662", {"points": [v(7.41, 1.66) * mm, v(7.22, 1.1) * mm, v(7.02, 0.56) * mm, v(6.8, 0.03) * mm]});
            skFitSpline(sketch, "E663", {"points": [v(6.8, 0.03) * mm, v(6.57, -0.5) * mm, v(6.38, -0.98) * mm, v(6.2, -1.38) * mm]});
            skFitSpline(sketch, "E664", {"points": [v(6.2, -1.38) * mm, v(6.14, -1.53) * mm, v(6.06, -1.7) * mm, v(5.97, -1.88) * mm]});
            skFitSpline(sketch, "E665", {"points": [v(5.97, -1.88) * mm, v(5.89, -2.07) * mm, v(5.82, -2.24) * mm, v(5.77, -2.39) * mm]});
            skFitSpline(sketch, "E666", {"points": [v(5.77, -2.39) * mm, v(5.44, -3.3) * mm, v(5.11, -4.23) * mm, v(4.77, -5.2) * mm]});
            skFitSpline(sketch, "E667", {"points": [v(4.77, -5.2) * mm, v(4.43, -6.16) * mm, v(4.1, -7.11) * mm, v(3.77, -8.07) * mm]});
            skFitSpline(sketch, "E668", {"points": [v(3.77, -8.07) * mm, v(3.46, -9.02) * mm, v(3.18, -9.96) * mm, v(2.92, -10.88) * mm]});
            skFitSpline(sketch, "E669", {"points": [v(2.92, -10.88) * mm, v(2.66, -11.8) * mm, v(2.45, -12.69) * mm, v(2.28, -13.52) * mm]});
            skFitSpline(sketch, "E670", {"points": [v(2.28, -13.52) * mm, v(2.67, -13.8) * mm, v(3.02, -14.09) * mm, v(3.33, -14.35) * mm]});
            skFitSpline(sketch, "E671", {"points": [v(3.33, -14.35) * mm, v(3.66, -14.62) * mm, v(3.97, -14.92) * mm, v(4.28, -15.26) * mm]});
            skFitSpline(sketch, "E672", {"points": [v(4.28, -15.26) * mm, v(4.28, -14.2) * mm, v(4.54, -13.33) * mm, v(5.05, -12.64) * mm]});
            skFitSpline(sketch, "E673", {"points": [v(5.05, -12.64) * mm, v(5.56, -11.96) * mm, v(6.2, -11.47) * mm, v(6.98, -11.19) * mm]});
            skFitSpline(sketch, "E674", {"points": [v(6.98, -11.19) * mm, v(7.64, -10.95) * mm, v(8.27, -10.83) * mm, v(8.85, -10.83) * mm]});
            skFitSpline(sketch, "E675", {"points": [v(8.85, -10.83) * mm, v(9.46, -10.83) * mm, v(10.02, -10.94) * mm, v(10.52, -11.16) * mm]});
            skFitSpline(sketch, "E676", {"points": [v(10.52, -11.16) * mm, v(11.01, -11.4) * mm, v(11.43, -11.7) * mm, v(11.77, -12.07) * mm]});
            skFitSpline(sketch, "E677", {"points": [v(11.77, -12.07) * mm, v(12.13, -12.45) * mm, v(12.4, -12.89) * mm, v(12.6, -13.37) * mm]});
            skFitSpline(sketch, "E678", {"points": [v(12.6, -13.37) * mm, v(12.78, -13.88) * mm, v(12.88, -14.4) * mm, v(12.88, -14.96) * mm]});
            skFitSpline(sketch, "E679", {"points": [v(12.88, -14.96) * mm, v(12.88, -15.53) * mm, v(12.74, -16.1) * mm, v(12.47, -16.7) * mm]});
            skFitSpline(sketch, "E680", {"points": [v(12.47, -16.7) * mm, v(12.2, -17.3) * mm, v(11.78, -17.87) * mm, v(11.24, -18.4) * mm]});
            skFitSpline(sketch, "E681", {"points": [v(11.24, -18.4) * mm, v(10.7, -18.94) * mm, v(10.04, -19.42) * mm, v(9.23, -19.83) * mm]});
            skFitSpline(sketch, "E682", {"points": [v(9.23, -19.83) * mm, v(8.45, -20.27) * mm, v(7.53, -20.6) * mm, v(6.49, -20.84) * mm]});
            skFitSpline(sketch, "E683", {"points": [v(6.49, -20.84) * mm, v(6.23, -20.87) * mm, v(5.96, -20.9) * mm, v(5.67, -20.92) * mm]});
            skFitSpline(sketch, "E684", {"points": [v(5.67, -20.92) * mm, v(5.4, -20.95) * mm, v(5.13, -20.97) * mm, v(4.87, -20.97) * mm]});
            skFitSpline(sketch, "E685", {"points": [v(4.7, -17.97) * mm, v(4.57, -17.62) * mm, v(4.32, -17.21) * mm, v(3.95, -16.74) * mm]});
            skFitSpline(sketch, "E686", {"points": [v(3.95, -16.74) * mm, v(3.57, -16.29) * mm, v(2.97, -15.83) * mm, v(2.15, -15.36) * mm]});
            skFitSpline(sketch, "E687", {"points": [v(2.15, -15.36) * mm, v(2.2, -15.86) * mm, v(2.3, -16.36) * mm, v(2.43, -16.84) * mm]});
            skFitSpline(sketch, "E688", {"points": [v(2.43, -16.84) * mm, v(2.59, -17.35) * mm, v(2.8, -17.79) * mm, v(3.08, -18.18) * mm]});
            skFitSpline(sketch, "E689", {"points": [v(3.08, -18.18) * mm, v(3.37, -18.58) * mm, v(3.72, -18.89) * mm, v(4.13, -19.1) * mm]});
            skFitSpline(sketch, "E690", {"points": [v(4.13, -19.1) * mm, v(4.54, -19.32) * mm, v(5.03, -19.4) * mm, v(5.62, -19.3) * mm]});
            skFitSpline(sketch, "E691", {"points": [v(5.62, -19.3) * mm, v(6.35, -19.22) * mm, v(7, -19.02) * mm, v(7.54, -18.7) * mm]});
            skFitSpline(sketch, "E692", {"points": [v(7.54, -18.7) * mm, v(8.09, -18.38) * mm, v(8.54, -18) * mm, v(8.9, -17.55) * mm]});
            skFitSpline(sketch, "E693", {"points": [v(8.9, -17.55) * mm, v(9.28, -17.11) * mm, v(9.56, -16.64) * mm, v(9.75, -16.14) * mm]});
            skFitSpline(sketch, "E694", {"points": [v(9.75, -16.14) * mm, v(9.94, -15.64) * mm, v(10.03, -15.15) * mm, v(10.03, -14.68) * mm]});
            skFitSpline(sketch, "E695", {"points": [v(10.03, -14.68) * mm, v(10.03, -14.11) * mm, v(9.9, -13.62) * mm, v(9.62, -13.22) * mm]});
            skFitSpline(sketch, "E696", {"points": [v(9.62, -13.22) * mm, v(9.35, -12.84) * mm, v(8.9, -12.64) * mm, v(8.31, -12.64) * mm]});
            skFitSpline(sketch, "E697", {"points": [v(8.31, -12.64) * mm, v(8.2, -12.64) * mm, v(8.08, -12.65) * mm, v(7.93, -12.67) * mm]});
            skFitSpline(sketch, "E698", {"points": [v(7.93, -12.67) * mm, v(7.79, -12.69) * mm, v(7.64, -12.72) * mm, v(7.49, -12.77) * mm]});
            skFitSpline(sketch, "E699", {"points": [v(7.49, -12.77) * mm, v(7.2, -12.85) * mm, v(6.92, -13) * mm, v(6.64, -13.2) * mm]});
            skFitSpline(sketch, "E700", {"points": [v(6.64, -13.2) * mm, v(6.39, -13.42) * mm, v(6.15, -13.67) * mm, v(5.95, -13.95) * mm]});
            skFitSpline(sketch, "E701", {"points": [v(5.95, -13.95) * mm, v(5.74, -14.25) * mm, v(5.58, -14.59) * mm, v(5.46, -14.96) * mm]});
            skFitSpline(sketch, "E702", {"points": [v(5.46, -14.96) * mm, v(5.34, -15.33) * mm, v(5.28, -15.71) * mm, v(5.28, -16.11) * mm]});
            skFitSpline(sketch, "E703", {"points": [v(5.28, -16.11) * mm, v(5.28, -16.62) * mm, v(5.4, -17.14) * mm, v(5.62, -17.67) * mm]});
            skFitSpline(sketch, "E704", {"points": [v(5.6, -17.65) * mm, v(5.7, -17.83) * mm, v(5.71, -17.97) * mm, v(5.64, -18.05) * mm]});
            skFitSpline(sketch, "E705", {"points": [v(5.64, -18.05) * mm, v(5.6, -18.15) * mm, v(5.48, -18.25) * mm, v(5.3, -18.35) * mm]});
            skFitSpline(sketch, "E706", {"points": [v(5.3, -18.35) * mm, v(5.14, -18.42) * mm, v(5, -18.41) * mm, v(4.9, -18.33) * mm]});
            skFitSpline(sketch, "E707", {"points": [v(4.9, -18.33) * mm, v(4.81, -18.24) * mm, v(4.74, -18.13) * mm, v(4.7, -18) * mm]});
            skFitSpline(sketch, "E708", {"points": [v(0.84, 7.67) * mm, v(0.8, 7.35) * mm, v(0.84, 7.08) * mm, v(0.95, 6.87) * mm]});
            skFitSpline(sketch, "E709", {"points": [v(0.95, 6.87) * mm, v(1.07, 6.67) * mm, v(1.29, 6.52) * mm, v(1.61, 6.44) * mm]});
            skFitSpline(sketch, "E710", {"points": [v(1.61, 6.44) * mm, v(1.68, 6.59) * mm, v(1.78, 6.83) * mm, v(1.92, 7.17) * mm]});
            skFitSpline(sketch, "E711", {"points": [v(1.92, 7.17) * mm, v(2.07, 7.5) * mm, v(2.23, 7.87) * mm, v(2.38, 8.27) * mm]});
            skFitSpline(sketch, "E712", {"points": [v(2.38, 8.27) * mm, v(2.54, 8.7) * mm, v(2.67, 9.11) * mm, v(2.8, 9.53) * mm]});
            skFitSpline(sketch, "E713", {"points": [v(2.8, 9.53) * mm, v(2.91, 9.95) * mm, v(3, 10.32) * mm, v(3.02, 10.64) * mm]});
            skFitSpline(sketch, "E714", {"points": [v(3.02, 10.64) * mm, v(3.04, 10.99) * mm, v(3, 11.17) * mm, v(2.92, 11.17) * mm]});
            skFitSpline(sketch, "E715", {"points": [v(2.92, 11.17) * mm, v(2.78, 11.17) * mm, v(2.6, 11.05) * mm, v(2.38, 10.81) * mm]});
            skFitSpline(sketch, "E716", {"points": [v(2.38, 10.81) * mm, v(2.16, 10.6) * mm, v(1.94, 10.31) * mm, v(1.72, 9.96) * mm]});
            skFitSpline(sketch, "E717", {"points": [v(1.72, 9.96) * mm, v(1.51, 9.6) * mm, v(1.32, 9.22) * mm, v(1.15, 8.8) * mm]});
            skFitSpline(sketch, "E718", {"points": [v(1.15, 8.8) * mm, v(0.98, 8.4) * mm, v(0.88, 8.02) * mm, v(0.84, 7.67) * mm]});
            skFitSpline(sketch, "E719", {"points": [v(10.53, 7.7) * mm, v(10.58, 7.96) * mm, v(10.6, 8.2) * mm, v(10.6, 8.4) * mm]});
            skFitSpline(sketch, "E720", {"points": [v(10.6, 8.4) * mm, v(10.6, 8.58) * mm, v(10.62, 8.74) * mm, v(10.66, 8.88) * mm]});
            skFitSpline(sketch, "E721", {"points": [v(10.66, 8.88) * mm, v(10.73, 9.1) * mm, v(10.86, 9.22) * mm, v(11.07, 9.25) * mm]});
            skFitSpline(sketch, "E722", {"points": [v(11.07, 9.25) * mm, v(11.27, 9.3) * mm, v(11.5, 9.3) * mm, v(11.74, 9.23) * mm]});
            skFitSpline(sketch, "E723", {"points": [v(11.74, 9.23) * mm, v(12.45, 8.98) * mm, v(12.98, 8.7) * mm, v(13.3, 8.4) * mm]});
            skFitSpline(sketch, "E724", {"points": [v(13.3, 8.4) * mm, v(13.63, 8.1) * mm, v(13.79, 7.7) * mm, v(13.79, 7.22) * mm]});
            skFitSpline(sketch, "E725", {"points": [v(13.79, 7.22) * mm, v(13.79, 6.98) * mm, v(13.75, 6.72) * mm, v(13.69, 6.44) * mm]});
            skFitSpline(sketch, "E726", {"points": [v(13.69, 6.44) * mm, v(13.63, 6.15) * mm, v(13.56, 5.84) * mm, v(13.45, 5.5) * mm]});
            skFitSpline(sketch, "E727", {"points": [v(13.45, 5.5) * mm, v(13.28, 4.97) * mm, v(13.09, 4.32) * mm, v(12.86, 3.55) * mm]});
            skFitSpline(sketch, "E728", {"points": [v(12.86, 3.55) * mm, v(12.66, 2.8) * mm, v(12.45, 1.99) * mm, v(12.25, 1.13) * mm]});
            skFitSpline(sketch, "E729", {"points": [v(12.25, 1.13) * mm, v(12.04, 0.3) * mm, v(11.86, -0.54) * mm, v(11.68, -1.38) * mm]});
            skFitSpline(sketch, "E730", {"points": [v(11.68, -1.38) * mm, v(11.53, -2.22) * mm, v(11.41, -2.99) * mm, v(11.32, -3.7) * mm]});
            skFitSpline(sketch, "E731", {"points": [v(11.32, -3.7) * mm, v(11.3, -3.86) * mm, v(11.3, -4.05) * mm, v(11.27, -4.25) * mm]});
            skFitSpline(sketch, "E732", {"points": [v(11.27, -4.25) * mm, v(11.27, -4.43) * mm, v(11.27, -4.6) * mm, v(11.27, -4.72) * mm]});
            skFitSpline(sketch, "E733", {"points": [v(11.27, -4.72) * mm, v(11.27, -5.31) * mm, v(11.33, -5.79) * mm, v(11.45, -6.16) * mm]});
            skFitSpline(sketch, "E734", {"points": [v(11.45, -6.16) * mm, v(11.57, -6.5) * mm, v(11.78, -6.7) * mm, v(12.07, -6.71) * mm]});
            skFitSpline(sketch, "E735", {"points": [v(12.07, -6.71) * mm, v(12.3, -6.71) * mm, v(12.58, -6.57) * mm, v(12.89, -6.28) * mm]});
            skFitSpline(sketch, "E736", {"points": [v(12.89, -6.28) * mm, v(13.21, -6) * mm, v(13.56, -5.62) * mm, v(13.92, -5.15) * mm]});
            skFitSpline(sketch, "E737", {"points": [v(13.92, -5.15) * mm, v(14.28, -4.68) * mm, v(14.64, -4.15) * mm, v(15.02, -3.57) * mm]});
            skFitSpline(sketch, "E738", {"points": [v(15.02, -3.57) * mm, v(15.4, -2.96) * mm, v(15.77, -2.34) * mm, v(16.15, -1.7) * mm]});
            skFitSpline(sketch, "E739", {"points": [v(16.15, -1.7) * mm, v(16.22, -1.58) * mm, v(16.3, -1.45) * mm, v(16.37, -1.33) * mm]});
            skFitSpline(sketch, "E740", {"points": [v(15.74, -4.57) * mm, v(15.2, -5.36) * mm, v(14.68, -6.07) * mm, v(14.15, -6.69) * mm]});
            skFitSpline(sketch, "E741", {"points": [v(14.15, -6.69) * mm, v(13.6, -7.32) * mm, v(13.05, -7.83) * mm, v(12.5, -8.22) * mm]});
            skFitSpline(sketch, "E742", {"points": [v(12.5, -8.22) * mm, v(11.96, -8.6) * mm, v(11.44, -8.8) * mm, v(10.94, -8.8) * mm]});
            skFitSpline(sketch, "E743", {"points": [v(10.94, -8.8) * mm, v(10.34, -8.8) * mm, v(9.84, -8.68) * mm, v(9.43, -8.45) * mm]});
            skFitSpline(sketch, "E744", {"points": [v(9.43, -8.45) * mm, v(9.03, -8.21) * mm, v(8.7, -7.9) * mm, v(8.45, -7.49) * mm]});
            skFitSpline(sketch, "E745", {"points": [v(8.45, -7.49) * mm, v(8.21, -7.07) * mm, v(8.04, -6.6) * mm, v(7.94, -6.06) * mm]});
            skFitSpline(sketch, "E746", {"points": [v(7.94, -6.06) * mm, v(7.83, -5.5) * mm, v(7.78, -4.9) * mm, v(7.78, -4.27) * mm]});
            skFitSpline(sketch, "E747", {"points": [v(7.78, -4.27) * mm, v(7.78, -4.07) * mm, v(7.8, -3.87) * mm, v(7.8, -3.67) * mm]});
            skFitSpline(sketch, "E748", {"points": [v(7.8, -3.67) * mm, v(7.8, -3.45) * mm, v(7.82, -3.24) * mm, v(7.83, -3.04) * mm]});
            skFitSpline(sketch, "E749", {"points": [v(7.83, -3.04) * mm, v(7.97, -1.4) * mm, v(8.26, 0.21) * mm, v(8.7, 1.79) * mm]});
            skFitSpline(sketch, "E750", {"points": [v(8.7, 1.79) * mm, v(9.15, 3.38) * mm, v(9.64, 4.97) * mm, v(10.17, 6.56) * mm]});
            skFitSpline(sketch, "E751", {"points": [v(15.17, 14.16) * mm, v(15.36, 13.82) * mm, v(15.5, 13.51) * mm, v(15.56, 13.23) * mm]});
            skFitSpline(sketch, "E752", {"points": [v(15.56, 13.23) * mm, v(15.64, 12.96) * mm, v(15.68, 12.7) * mm, v(15.66, 12.47) * mm]});
            skFitSpline(sketch, "E753", {"points": [v(15.66, 12.47) * mm, v(15.6, 11.9) * mm, v(15.36, 11.46) * mm, v(14.92, 11.14) * mm]});
            skFitSpline(sketch, "E754", {"points": [v(14.92, 11.14) * mm, v(14.47, 10.84) * mm, v(14.01, 10.69) * mm, v(13.53, 10.69) * mm]});
            skFitSpline(sketch, "E755", {"points": [v(13.53, 10.69) * mm, v(13.12, 10.69) * mm, v(12.76, 10.85) * mm, v(12.45, 11.17) * mm]});
            skFitSpline(sketch, "E756", {"points": [v(12.45, 11.17) * mm, v(12.15, 11.5) * mm, v(12, 12.02) * mm, v(12.04, 12.72) * mm]});
            skFitSpline(sketch, "E757", {"points": [v(12.04, 12.72) * mm, v(12.06, 13) * mm, v(12.12, 13.26) * mm, v(12.22, 13.53) * mm]});
            skFitSpline(sketch, "E758", {"points": [v(12.22, 13.53) * mm, v(12.33, 13.81) * mm, v(12.45, 14.07) * mm, v(12.6, 14.28) * mm]});
            skFitSpline(sketch, "E759", {"points": [v(12.6, 14.28) * mm, v(12.76, 14.5) * mm, v(12.94, 14.68) * mm, v(13.15, 14.81) * mm]});
            skFitSpline(sketch, "E760", {"points": [v(13.15, 14.81) * mm, v(13.37, 14.95) * mm, v(13.6, 15.01) * mm, v(13.84, 15.01) * mm]});
            skFitSpline(sketch, "E761", {"points": [v(13.84, 15.01) * mm, v(14.06, 15.01) * mm, v(14.28, 14.95) * mm, v(14.5, 14.81) * mm]});
            skFitSpline(sketch, "E762", {"points": [v(14.5, 14.81) * mm, v(14.75, 14.68) * mm, v(14.97, 14.46) * mm, v(15.17, 14.16) * mm]});
            skFitSpline(sketch, "E763", {"points": [v(24.46, -12.22) * mm, v(24.6, -11.31) * mm, v(24.74, -10.36) * mm, v(24.87, -9.35) * mm]});
            skFitSpline(sketch, "E764", {"points": [v(24.87, -9.35) * mm, v(25.01, -8.34) * mm, v(25.16, -7.36) * mm, v(25.31, -6.38) * mm]});
            skFitSpline(sketch, "E765", {"points": [v(25.31, -6.38) * mm, v(25.34, -6.1) * mm, v(25.37, -5.85) * mm, v(25.39, -5.63) * mm]});
            skFitSpline(sketch, "E766", {"points": [v(25.39, -5.63) * mm, v(25.42, -5.4) * mm, v(25.48, -5.05) * mm, v(25.57, -4.6) * mm]});
            skFitSpline(sketch, "E767", {"points": [v(25.57, -4.6) * mm, v(25.12, -5.2) * mm, v(24.66, -5.77) * mm, v(24.18, -6.3) * mm]});
            skFitSpline(sketch, "E768", {"points": [v(24.18, -6.3) * mm, v(23.7, -6.83) * mm, v(23.2, -7.28) * mm, v(22.67, -7.67) * mm]});
            skFitSpline(sketch, "E769", {"points": [v(22.67, -7.67) * mm, v(22.15, -8.05) * mm, v(21.62, -8.36) * mm, v(21.05, -8.6) * mm]});
            skFitSpline(sketch, "E770", {"points": [v(21.05, -8.6) * mm, v(20.49, -8.81) * mm, v(19.9, -8.92) * mm, v(19.3, -8.92) * mm]});
            skFitSpline(sketch, "E771", {"points": [v(19.3, -8.92) * mm, v(18.62, -8.92) * mm, v(18.06, -8.81) * mm, v(17.61, -8.6) * mm]});
            skFitSpline(sketch, "E772", {"points": [v(17.61, -8.6) * mm, v(17.15, -8.36) * mm, v(16.78, -8.05) * mm, v(16.5, -7.67) * mm]});
            skFitSpline(sketch, "E773", {"points": [v(16.5, -7.67) * mm, v(16.24, -7.26) * mm, v(16.04, -6.81) * mm, v(15.92, -6.3) * mm]});
            skFitSpline(sketch, "E774", {"points": [v(15.92, -6.3) * mm, v(15.8, -5.79) * mm, v(15.74, -5.24) * mm, v(15.74, -4.67) * mm]});
            skFitSpline(sketch, "E775", {"points": [v(15.74, -4.67) * mm, v(15.74, -4.64) * mm, v(15.74, -4.6) * mm, v(15.74, -4.57) * mm]});
            skFitSpline(sketch, "E776", {"points": [v(16.37, -1.33) * mm, v(16.39, -1.26) * mm, v(16.41, -1.2) * mm, v(16.43, -1.13) * mm]});
            skFitSpline(sketch, "E777", {"points": [v(16.43, -1.13) * mm, v(16.76, -0.1) * mm, v(17.18, 0.92) * mm, v(17.72, 1.96) * mm]});
            skFitSpline(sketch, "E778", {"points": [v(17.72, 1.96) * mm, v(18.25, 3.02) * mm, v(18.85, 4.04) * mm, v(19.54, 5.03) * mm]});
            skFitSpline(sketch, "E779", {"points": [v(19.54, 5.03) * mm, v(20.22, 6.02) * mm, v(20.97, 6.9) * mm, v(21.77, 7.65) * mm]});
            skFitSpline(sketch, "E780", {"points": [v(21.77, 7.65) * mm, v(22.57, 8.42) * mm, v(23.43, 9.03) * mm, v(24.34, 9.48) * mm]});
            skFitSpline(sketch, "E781", {"points": [v(24.34, 9.48) * mm, v(25.24, 9.95) * mm, v(26.18, 10.19) * mm, v(27.16, 10.19) * mm]});
            skFitSpline(sketch, "E782", {"points": [v(27.16, 10.19) * mm, v(27.91, 10.19) * mm, v(28.58, 10) * mm, v(29.16, 9.66) * mm]});
            skFitSpline(sketch, "E783", {"points": [v(29.16, 9.66) * mm, v(29.74, 9.3) * mm, v(30.23, 8.84) * mm, v(30.62, 8.27) * mm]});
            skFitSpline(sketch, "E784", {"points": [v(30.62, 8.27) * mm, v(31.02, 7.72) * mm, v(31.3, 7.1) * mm, v(31.47, 6.39) * mm]});
            skFitSpline(sketch, "E785", {"points": [v(31.47, 6.39) * mm, v(31.66, 5.7) * mm, v(31.73, 5) * mm, v(31.67, 4.3) * mm]});
            skFitSpline(sketch, "E786", {"points": [v(31.67, 4.3) * mm, v(31.62, 3.83) * mm, v(31.52, 3.39) * mm, v(31.37, 2.97) * mm]});
            skFitSpline(sketch, "E787", {"points": [v(31.37, 2.97) * mm, v(31.33, 2.9) * mm, v(31.23, 2.84) * mm, v(31.06, 2.77) * mm]});
            skFitSpline(sketch, "E788", {"points": [v(31.06, 2.77) * mm, v(30.89, 2.72) * mm, v(30.77, 2.7) * mm, v(30.7, 2.7) * mm]});
            skFitSpline(sketch, "E789", {"points": [v(30.7, 2.7) * mm, v(30.61, 2.7) * mm, v(30.52, 2.72) * mm, v(30.42, 2.77) * mm]});
            skFitSpline(sketch, "E790", {"points": [v(30.42, 2.77) * mm, v(30.33, 2.82) * mm, v(30.25, 2.9) * mm, v(30.16, 3) * mm]});
            skFitSpline(sketch, "E791", {"points": [v(30.16, 3) * mm, v(30.23, 3.18) * mm, v(30.27, 3.35) * mm, v(30.29, 3.5) * mm]});
            skFitSpline(sketch, "E792", {"points": [v(30.29, 3.5) * mm, v(30.32, 3.66) * mm, v(30.36, 3.84) * mm, v(30.4, 4.03) * mm]});
            skFitSpline(sketch, "E793", {"points": [v(30.4, 4.03) * mm, v(30.4, 4.44) * mm, v(30.37, 4.88) * mm, v(30.29, 5.33) * mm]});
            skFitSpline(sketch, "E794", {"points": [v(30.29, 5.33) * mm, v(30.22, 5.8) * mm, v(30.08, 6.22) * mm, v(29.88, 6.59) * mm]});
            skFitSpline(sketch, "E795", {"points": [v(29.88, 6.59) * mm, v(29.7, 6.96) * mm, v(29.43, 7.26) * mm, v(29.1, 7.5) * mm]});
            skFitSpline(sketch, "E796", {"points": [v(29.1, 7.5) * mm, v(28.78, 7.75) * mm, v(28.39, 7.87) * mm, v(27.93, 7.87) * mm]});
            skFitSpline(sketch, "E797", {"points": [v(27.93, 7.87) * mm, v(27.31, 7.87) * mm, v(26.7, 7.64) * mm, v(26.08, 7.17) * mm]});
            skFitSpline(sketch, "E798", {"points": [v(26.08, 7.17) * mm, v(25.48, 6.72) * mm, v(24.9, 6.12) * mm, v(24.3, 5.38) * mm]});
            skFitSpline(sketch, "E799", {"points": [v(24.3, 5.38) * mm, v(23.75, 4.66) * mm, v(23.22, 3.85) * mm, v(22.72, 2.94) * mm]});
            skFitSpline(sketch, "E800", {"points": [v(22.72, 2.94) * mm, v(22.22, 2.04) * mm, v(21.78, 1.13) * mm, v(21.38, 0.23) * mm]});
            skFitSpline(sketch, "E801", {"points": [v(21.38, 0.23) * mm, v(21, -0.66) * mm, v(20.7, -1.5) * mm, v(20.46, -2.29) * mm]});
            skFitSpline(sketch, "E802", {"points": [v(20.46, -2.29) * mm, v(20.22, -3.07) * mm, v(20.08, -3.71) * mm, v(20.05, -4.2) * mm]});
            skFitSpline(sketch, "E803", {"points": [v(20.05, -4.2) * mm, v(20.03, -4.43) * mm, v(20.02, -4.68) * mm, v(20.02, -4.95) * mm]});
            skFitSpline(sketch, "E804", {"points": [v(20.02, -4.95) * mm, v(20.04, -5.22) * mm, v(20.1, -5.47) * mm, v(20.18, -5.7) * mm]});
            skFitSpline(sketch, "E805", {"points": [v(20.18, -5.7) * mm, v(20.26, -5.92) * mm, v(20.4, -6.1) * mm, v(20.56, -6.26) * mm]});
            skFitSpline(sketch, "E806", {"points": [v(20.56, -6.26) * mm, v(20.73, -6.4) * mm, v(20.97, -6.46) * mm, v(21.28, -6.46) * mm]});
            skFitSpline(sketch, "E807", {"points": [v(21.28, -6.46) * mm, v(21.7, -6.46) * mm, v(22.15, -6.3) * mm, v(22.62, -5.96) * mm]});
            skFitSpline(sketch, "E808", {"points": [v(22.62, -5.96) * mm, v(23.08, -5.62) * mm, v(23.53, -5.2) * mm, v(23.98, -4.67) * mm]});
            skFitSpline(sketch, "E809", {"points": [v(23.98, -4.67) * mm, v(24.42, -4.14) * mm, v(24.86, -3.55) * mm, v(25.29, -2.91) * mm]});
            skFitSpline(sketch, "E810", {"points": [v(25.29, -2.91) * mm, v(25.71, -2.28) * mm, v(26.1, -1.65) * mm, v(26.44, -1.03) * mm]});
            skFitSpline(sketch, "E811", {"points": [v(26.41, -1.03) * mm, v(26.59, -0.54) * mm, v(26.78, -0.09) * mm, v(27, 0.33) * mm]});
            skFitSpline(sketch, "E812", {"points": [v(27, 0.33) * mm, v(27.23, 0.75) * mm, v(27.5, 1.13) * mm, v(27.8, 1.46) * mm]});
            skFitSpline(sketch, "E813", {"points": [v(28.03, 1.71) * mm, v(28.36, 1.95) * mm, v(28.74, 2.12) * mm, v(29.19, 2.24) * mm]});
            skFitSpline(sketch, "E814", {"points": [v(29.19, 2.24) * mm, v(29.63, 2.36) * mm, v(30.1, 2.4) * mm, v(30.6, 2.34) * mm]});
            skFitSpline(sketch, "E815", {"points": [v(30.6, 2.34) * mm, v(30.84, 2.3) * mm, v(31.02, 2.23) * mm, v(31.14, 2.11) * mm]});
            skFitSpline(sketch, "E816", {"points": [v(31.14, 2.11) * mm, v(31.27, 2) * mm, v(31.32, 1.83) * mm, v(31.26, 1.61) * mm]});
            skFitSpline(sketch, "E817", {"points": [v(31.26, 1.61) * mm, v(31.26, 1.6) * mm, v(31.24, 1.54) * mm, v(31.19, 1.44) * mm]});
            skFitSpline(sketch, "E818", {"points": [v(31.19, 1.44) * mm, v(31.14, 1.33) * mm, v(31.08, 1.23) * mm, v(31, 1.1) * mm]});
            skFitSpline(sketch, "E819", {"points": [v(31, 1.1) * mm, v(30.92, 0.97) * mm, v(30.83, 0.8) * mm, v(30.73, 0.6) * mm]});
            skFitSpline(sketch, "E820", {"points": [v(30.73, 0.6) * mm, v(30.64, 0.42) * mm, v(30.55, 0.16) * mm, v(30.47, -0.17) * mm]});
            skFitSpline(sketch, "E821", {"points": [v(30.47, -0.17) * mm, v(30.37, -0.48) * mm, v(30.26, -0.88) * mm, v(30.16, -1.38) * mm]});
            skFitSpline(sketch, "E822", {"points": [v(30.16, -1.38) * mm, v(30.06, -1.87) * mm, v(29.96, -2.42) * mm, v(29.85, -3.04) * mm]});
            skFitSpline(sketch, "E823", {"points": [v(29.85, -3.04) * mm, v(29.75, -3.66) * mm, v(29.64, -4.33) * mm, v(29.52, -5.05) * mm]});
            skFitSpline(sketch, "E824", {"points": [v(29.52, -5.05) * mm, v(29.42, -5.77) * mm, v(29.3, -6.52) * mm, v(29.19, -7.29) * mm]});
            skFitSpline(sketch, "E825", {"points": [v(29.29, -7.04) * mm, v(29.89, -5.8) * mm, v(30.48, -4.57) * mm, v(31.06, -3.37) * mm]});
            skFitSpline(sketch, "E826", {"points": [v(31.06, -3.37) * mm, v(31.64, -2.16) * mm, v(32.17, -1.06) * mm, v(32.65, -0.07) * mm]});
            skFitSpline(sketch, "E827", {"points": [v(32.65, -0.07) * mm, v(33.13, 0.93) * mm, v(33.54, 1.79) * mm, v(33.88, 2.5) * mm]});
            skFitSpline(sketch, "E828", {"points": [v(33.88, 2.5) * mm, v(34.22, 3.21) * mm, v(34.45, 3.72) * mm, v(34.55, 4) * mm]});
            skFitSpline(sketch, "E829", {"points": [v(34.55, 4) * mm, v(34.58, 4.01) * mm, v(34.61, 4.02) * mm, v(34.65, 4.03) * mm]});
            skFitSpline(sketch, "E830", {"points": [v(33, -2.27) * mm, v(32.44, -3.44) * mm, v(31.83, -4.69) * mm, v(31.19, -6.03) * mm]});
            skFitSpline(sketch, "E831", {"points": [v(31.19, -6.03) * mm, v(30.49, -7.5) * mm, v(29.8, -8.96) * mm, v(29.1, -10.38) * mm]});
            skFitSpline(sketch, "E832", {"points": [v(29.1, -10.38) * mm, v(29.02, -10.57) * mm, v(28.92, -10.77) * mm, v(28.8, -10.98) * mm]});
            skFitSpline(sketch, "E833", {"points": [v(28.8, -10.98) * mm, v(28.7, -11.2) * mm, v(28.6, -11.4) * mm, v(28.52, -11.59) * mm]});
            skFitSpline(sketch, "E834", {"points": [v(28.52, -11.56) * mm, v(28.4, -12.32) * mm, v(28.28, -13.05) * mm, v(28.16, -13.78) * mm]});
            skFitSpline(sketch, "E835", {"points": [v(28.16, -13.78) * mm, v(28.04, -14.51) * mm, v(27.91, -15.2) * mm, v(27.77, -15.86) * mm]});
            skFitSpline(sketch, "E836", {"points": [v(27.77, -15.86) * mm, v(27.65, -16.53) * mm, v(27.53, -17.15) * mm, v(27.39, -17.72) * mm]});
            skFitSpline(sketch, "E837", {"points": [v(27.39, -17.72) * mm, v(27.27, -18.3) * mm, v(27.15, -18.8) * mm, v(27.03, -19.23) * mm]});
            skFitSpline(sketch, "E838", {"points": [v(27.03, -19.23) * mm, v(26.84, -19.87) * mm, v(26.59, -20.5) * mm, v(26.26, -21.14) * mm]});
            skFitSpline(sketch, "E839", {"points": [v(26.26, -21.14) * mm, v(25.95, -21.8) * mm, v(25.58, -22.37) * mm, v(25.13, -22.88) * mm]});
            skFitSpline(sketch, "E840", {"points": [v(25.13, -22.88) * mm, v(24.69, -23.4) * mm, v(24.18, -23.8) * mm, v(23.62, -24.08) * mm]});
            skFitSpline(sketch, "E841", {"points": [v(23.62, -24.08) * mm, v(23.05, -24.39) * mm, v(22.44, -24.5) * mm, v(21.77, -24.41) * mm]});
            skFitSpline(sketch, "E842", {"points": [v(21.77, -24.41) * mm, v(21.62, -24.38) * mm, v(21.5, -24.33) * mm, v(21.41, -24.26) * mm]});
            skFitSpline(sketch, "E843", {"points": [v(21.41, -24.26) * mm, v(21.32, -24.2) * mm, v(21.3, -24.1) * mm, v(21.36, -23.96) * mm]});
            skFitSpline(sketch, "E844", {"points": [v(21.36, -23.96) * mm, v(21.38, -23.92) * mm, v(21.4, -23.87) * mm, v(21.44, -23.8) * mm]});
            skFitSpline(sketch, "E845", {"points": [v(21.44, -23.8) * mm, v(21.47, -23.74) * mm, v(21.52, -23.65) * mm, v(21.59, -23.53) * mm]});
            skFitSpline(sketch, "E846", {"points": [v(21.59, -23.53) * mm, v(21.74, -23.3) * mm, v(21.93, -22.97) * mm, v(22.15, -22.55) * mm]});
            skFitSpline(sketch, "E847", {"points": [v(22.15, -22.55) * mm, v(22.38, -22.13) * mm, v(22.6, -21.61) * mm, v(22.8, -21) * mm]});
            skFitSpline(sketch, "E848", {"points": [v(22.8, -21) * mm, v(23.09, -19.99) * mm, v(23.33, -19.05) * mm, v(23.51, -18.18) * mm]});
            skFitSpline(sketch, "E849", {"points": [v(23.51, -18.18) * mm, v(23.7, -17.3) * mm, v(23.87, -16.47) * mm, v(24, -15.66) * mm]});
            skFitSpline(sketch, "E850", {"points": [v(38.13, 9.7) * mm, v(38.62, 9.4) * mm, v(38.96, 8.95) * mm, v(39.13, 8.35) * mm]});
            skFitSpline(sketch, "E851", {"points": [v(39.13, 8.35) * mm, v(39.3, 7.76) * mm, v(39.36, 7.14) * mm, v(39.3, 6.49) * mm]});
            skFitSpline(sketch, "E852", {"points": [v(39.3, 6.49) * mm, v(39.24, 5.75) * mm, v(39.1, 5.01) * mm, v(38.9, 4.28) * mm]});
            skFitSpline(sketch, "E853", {"points": [v(38.9, 4.28) * mm, v(38.7, 3.56) * mm, v(38.5, 2.94) * mm, v(38.3, 2.44) * mm]});
            skFitSpline(sketch, "E854", {"points": [v(38.3, 2.44) * mm, v(38.15, 1.96) * mm, v(37.96, 1.38) * mm, v(37.74, 0.7) * mm]});
            skFitSpline(sketch, "E855", {"points": [v(37.74, 0.7) * mm, v(37.54, 0.04) * mm, v(37.34, -0.66) * mm, v(37.15, -1.38) * mm]});
            skFitSpline(sketch, "E856", {"points": [v(37.15, -1.38) * mm, v(36.96, -2.08) * mm, v(36.78, -2.78) * mm, v(36.61, -3.47) * mm]});
            skFitSpline(sketch, "E857", {"points": [v(36.61, -3.47) * mm, v(36.46, -4.15) * mm, v(36.36, -4.75) * mm, v(36.3, -5.25) * mm]});
            skFitSpline(sketch, "E858", {"points": [v(36.3, -5.25) * mm, v(36.29, -5.62) * mm, v(36.3, -5.94) * mm, v(36.33, -6.2) * mm]});
            skFitSpline(sketch, "E859", {"points": [v(36.33, -6.2) * mm, v(36.38, -6.48) * mm, v(36.48, -6.6) * mm, v(36.64, -6.6) * mm]});
            skFitSpline(sketch, "E860", {"points": [v(36.64, -6.6) * mm, v(36.86, -6.6) * mm, v(37.14, -6.45) * mm, v(37.48, -6.13) * mm]});
            skFitSpline(sketch, "E861", {"points": [v(37.48, -6.13) * mm, v(37.84, -5.81) * mm, v(38.23, -5.4) * mm, v(38.64, -4.88) * mm]});
            skFitSpline(sketch, "E862", {"points": [v(38.64, -4.88) * mm, v(39.07, -4.36) * mm, v(39.5, -3.78) * mm, v(39.92, -3.14) * mm]});
            skFitSpline(sketch, "E863", {"points": [v(39.92, -3.14) * mm, v(40.37, -2.5) * mm, v(40.8, -1.86) * mm, v(41.2, -1.2) * mm]});
            skFitSpline(sketch, "E864", {"points": [v(41.2, -1.2) * mm, v(41.63, -0.55) * mm, v(42.03, 0.07) * mm, v(42.39, 0.66) * mm]});
            skFitSpline(sketch, "E865", {"points": [v(42.39, 0.66) * mm, v(42.74, 1.24) * mm, v(43.05, 1.74) * mm, v(43.3, 2.14) * mm]});
            skFitSpline(sketch, "E866", {"points": [v(43.28, 2.11) * mm, v(43.45, 2.62) * mm, v(43.6, 3.09) * mm, v(43.75, 3.52) * mm]});
            skFitSpline(sketch, "E867", {"points": [v(43.75, 3.52) * mm, v(43.9, 3.97) * mm, v(44.04, 4.41) * mm, v(44.16, 4.83) * mm]});
            skFitSpline(sketch, "E868", {"points": [v(44.16, 4.83) * mm, v(44.28, 5.27) * mm, v(44.38, 5.7) * mm, v(44.46, 6.14) * mm]});
            skFitSpline(sketch, "E869", {"points": [v(44.46, 6.14) * mm, v(44.55, 6.59) * mm, v(44.6, 7.07) * mm, v(44.64, 7.57) * mm]});
            skFitSpline(sketch, "E870", {"points": [v(44.64, 7.57) * mm, v(44.66, 7.7) * mm, v(44.66, 7.84) * mm, v(44.64, 7.97) * mm]});
            skFitSpline(sketch, "E871", {"points": [v(44.64, 7.97) * mm, v(44.63, 8.12) * mm, v(44.6, 8.27) * mm, v(44.57, 8.4) * mm]});
            skFitSpline(sketch, "E872", {"points": [v(44.57, 8.4) * mm, v(44.55, 8.45) * mm, v(44.54, 8.53) * mm, v(44.54, 8.65) * mm]});
            skFitSpline(sketch, "E873", {"points": [v(44.54, 8.65) * mm, v(44.54, 8.7) * mm, v(44.53, 8.74) * mm, v(44.52, 8.78) * mm]});
            skFitSpline(sketch, "E874", {"points": [v(44.52, 8.78) * mm, v(44.55, 9.11) * mm, v(44.69, 9.34) * mm, v(44.93, 9.46) * mm]});
            skFitSpline(sketch, "E875", {"points": [v(44.93, 9.46) * mm, v(45.17, 9.6) * mm, v(45.58, 9.66) * mm, v(46.16, 9.66) * mm]});
            skFitSpline(sketch, "E876", {"points": [v(46.16, 9.66) * mm, v(46.57, 9.66) * mm, v(46.9, 9.57) * mm, v(47.16, 9.4) * mm]});
            skFitSpline(sketch, "E877", {"points": [v(47.16, 9.4) * mm, v(47.41, 9.25) * mm, v(47.61, 9.05) * mm, v(47.75, 8.78) * mm]});
            skFitSpline(sketch, "E878", {"points": [v(47.75, 8.78) * mm, v(47.9, 8.53) * mm, v(48, 8.22) * mm, v(48.03, 7.87) * mm]});
            skFitSpline(sketch, "E879", {"points": [v(48.03, 7.87) * mm, v(48.08, 7.52) * mm, v(48.1, 7.16) * mm, v(48.06, 6.8) * mm]});
            skFitSpline(sketch, "E880", {"points": [v(48.06, 6.8) * mm, v(47.97, 5.87) * mm, v(47.77, 4.83) * mm, v(47.47, 3.67) * mm]});
            skFitSpline(sketch, "E881", {"points": [v(47.47, 3.67) * mm, v(47.16, 2.53) * mm, v(46.83, 1.41) * mm, v(46.5, 0.3) * mm]});
            skFitSpline(sketch, "E882", {"points": [v(46.5, 0.3) * mm, v(46.18, -0.7) * mm, v(45.9, -1.64) * mm, v(45.64, -2.51) * mm]});
            skFitSpline(sketch, "E883", {"points": [v(45.64, -2.51) * mm, v(45.39, -3.38) * mm, v(45.24, -4.12) * mm, v(45.2, -4.72) * mm]});
            skFitSpline(sketch, "E884", {"points": [v(45.2, -4.72) * mm, v(45.2, -4.9) * mm, v(45.18, -5.1) * mm, v(45.18, -5.33) * mm]});
            skFitSpline(sketch, "E885", {"points": [v(45.18, -5.33) * mm, v(45.18, -5.55) * mm, v(45.2, -5.76) * mm, v(45.23, -5.96) * mm]});
            skFitSpline(sketch, "E886", {"points": [v(45.23, -5.96) * mm, v(45.29, -6.16) * mm, v(45.35, -6.33) * mm, v(45.44, -6.48) * mm]});
            skFitSpline(sketch, "E887", {"points": [v(45.44, -6.48) * mm, v(45.52, -6.62) * mm, v(45.64, -6.69) * mm, v(45.77, -6.69) * mm]});
            skFitSpline(sketch, "E888", {"points": [v(45.77, -6.69) * mm, v(46.05, -6.69) * mm, v(46.39, -6.46) * mm, v(46.8, -6) * mm]});
            skFitSpline(sketch, "E889", {"points": [v(46.8, -6) * mm, v(47.23, -5.54) * mm, v(47.68, -4.95) * mm, v(48.16, -4.25) * mm]});
            skFitSpline(sketch, "E890", {"points": [v(48.16, -4.25) * mm, v(48.66, -3.54) * mm, v(49.15, -2.78) * mm, v(49.65, -1.96) * mm]});
            skFitSpline(sketch, "E891", {"points": [v(49.65, -1.96) * mm, v(50.14, -1.14) * mm, v(50.6, -0.36) * mm, v(51, 0.38) * mm]});
            skFitSpline(sketch, "E892", {"points": [v(51, 0.38) * mm, v(51.42, 1.12) * mm, v(51.76, 1.75) * mm, v(52.03, 2.27) * mm]});
            skFitSpline(sketch, "E893", {"points": [v(52.03, 2.27) * mm, v(52.14, 2.46) * mm, v(52.22, 2.62) * mm, v(52.3, 2.75) * mm]});
            skFitSpline(sketch, "E894", {"points": [v(51.36, -1.37) * mm, v(51.12, -1.8) * mm, v(50.88, -2.23) * mm, v(50.62, -2.66) * mm]});
            skFitSpline(sketch, "E895", {"points": [v(50.62, -2.66) * mm, v(50.18, -3.43) * mm, v(49.7, -4.19) * mm, v(49.21, -4.93) * mm]});
            skFitSpline(sketch, "E896", {"points": [v(49.21, -4.93) * mm, v(48.72, -5.65) * mm, v(48.2, -6.3) * mm, v(47.67, -6.86) * mm]});
            skFitSpline(sketch, "E897", {"points": [v(47.67, -6.86) * mm, v(47.16, -7.43) * mm, v(46.64, -7.88) * mm, v(46.1, -8.22) * mm]});
            skFitSpline(sketch, "E898", {"points": [v(46.1, -8.22) * mm, v(45.58, -8.55) * mm, v(45.05, -8.72) * mm, v(44.52, -8.72) * mm]});
            skFitSpline(sketch, "E899", {"points": [v(44.52, -8.72) * mm, v(43.92, -8.72) * mm, v(43.41, -8.65) * mm, v(43, -8.5) * mm]});
            skFitSpline(sketch, "E900", {"points": [v(43, -8.5) * mm, v(42.6, -8.33) * mm, v(42.28, -8.1) * mm, v(42.03, -7.82) * mm]});
            skFitSpline(sketch, "E901", {"points": [v(42.03, -7.82) * mm, v(41.79, -7.52) * mm, v(41.62, -7.16) * mm, v(41.51, -6.76) * mm]});
            skFitSpline(sketch, "E902", {"points": [v(41.51, -6.76) * mm, v(41.41, -6.36) * mm, v(41.36, -5.91) * mm, v(41.36, -5.43) * mm]});
            skFitSpline(sketch, "E903", {"points": [v(41.36, -4.7) * mm, v(41.38, -4.45) * mm, v(41.4, -4.19) * mm, v(41.44, -3.92) * mm]});
            skFitSpline(sketch, "E904", {"points": [v(41.44, -3.92) * mm, v(41.49, -3.63) * mm, v(41.55, -3.35) * mm, v(41.62, -3.06) * mm]});
            skFitSpline(sketch, "E905", {"points": [v(41.62, -3.06) * mm, v(41.58, -3.1) * mm, v(41.56, -3.13) * mm, v(41.54, -3.17) * mm]});
            skFitSpline(sketch, "E906", {"points": [v(41.54, -3.17) * mm, v(41.54, -3.2) * mm, v(41.52, -3.23) * mm, v(41.49, -3.27) * mm]});
            skFitSpline(sketch, "E907", {"points": [v(41.49, -3.27) * mm, v(41.04, -3.95) * mm, v(40.58, -4.63) * mm, v(40.1, -5.3) * mm]});
            skFitSpline(sketch, "E908", {"points": [v(40.1, -5.3) * mm, v(39.62, -5.97) * mm, v(39.12, -6.58) * mm, v(38.59, -7.14) * mm]});
            skFitSpline(sketch, "E909", {"points": [v(38.59, -7.14) * mm, v(38.06, -7.67) * mm, v(37.48, -8.11) * mm, v(36.87, -8.45) * mm]});
            skFitSpline(sketch, "E910", {"points": [v(36.87, -8.45) * mm, v(36.27, -8.78) * mm, v(35.63, -8.95) * mm, v(34.94, -8.95) * mm]});
            skFitSpline(sketch, "E911", {"points": [v(34.94, -8.95) * mm, v(34.05, -8.95) * mm, v(33.44, -8.66) * mm, v(33.1, -8.1) * mm]});
            skFitSpline(sketch, "E912", {"points": [v(33.1, -8.1) * mm, v(32.74, -7.5) * mm, v(32.56, -6.74) * mm, v(32.56, -5.78) * mm]});
            skFitSpline(sketch, "E913", {"points": [v(32.56, -5.78) * mm, v(32.56, -5.61) * mm, v(32.57, -5.45) * mm, v(32.58, -5.28) * mm]});
            skFitSpline(sketch, "E914", {"points": [v(32.58, -5.28) * mm, v(32.58, -5.1) * mm, v(32.6, -4.93) * mm, v(32.6, -4.75) * mm]});
            skFitSpline(sketch, "E915", {"points": [v(32.6, -4.75) * mm, v(32.66, -4.2) * mm, v(32.75, -3.6) * mm, v(32.87, -2.96) * mm]});
            skFitSpline(sketch, "E916", {"points": [v(32.87, -2.96) * mm, v(32.9, -2.73) * mm, v(32.95, -2.5) * mm, v(33, -2.27) * mm]});
            skFitSpline(sketch, "E917", {"points": [v(34.65, 4.03) * mm, v(34.82, 4.66) * mm, v(34.98, 5.27) * mm, v(35.12, 5.86) * mm]});
            skFitSpline(sketch, "E918", {"points": [v(35.12, 5.86) * mm, v(35.36, 6.77) * mm, v(35.5, 7.5) * mm, v(35.56, 8.05) * mm]});
            skFitSpline(sketch, "E919", {"points": [v(35.56, 8.05) * mm, v(35.6, 8.32) * mm, v(35.59, 8.53) * mm, v(35.53, 8.7) * mm]});
            skFitSpline(sketch, "E920", {"points": [v(35.53, 8.7) * mm, v(35.5, 8.89) * mm, v(35.47, 9.05) * mm, v(35.43, 9.18) * mm]});
            skFitSpline(sketch, "E921", {"points": [v(35.43, 9.15) * mm, v(35.4, 9.24) * mm, v(35.38, 9.3) * mm, v(35.38, 9.36) * mm]});
            skFitSpline(sketch, "E922", {"points": [v(35.38, 9.36) * mm, v(35.38, 9.4) * mm, v(35.38, 9.46) * mm, v(35.38, 9.53) * mm]});
            skFitSpline(sketch, "E923", {"points": [v(35.38, 9.53) * mm, v(35.4, 9.77) * mm, v(35.5, 9.93) * mm, v(35.69, 10) * mm]});
            skFitSpline(sketch, "E924", {"points": [v(35.69, 10) * mm, v(35.88, 10.1) * mm, v(36.1, 10.13) * mm, v(36.33, 10.13) * mm]});
            skFitSpline(sketch, "E925", {"points": [v(36.33, 10.13) * mm, v(36.67, 10.13) * mm, v(37.01, 10.08) * mm, v(37.36, 9.98) * mm]});
            skFitSpline(sketch, "E926", {"points": [v(37.36, 9.98) * mm, v(37.72, 9.88) * mm, v(37.97, 9.8) * mm, v(38.13, 9.7) * mm]});
            skFitSpline(sketch, "E927", {"points": [v(65.32, -2.03) * mm, v(64.86, -2.84) * mm, v(64.35, -3.69) * mm, v(63.78, -4.57) * mm]});
            skFitSpline(sketch, "E928", {"points": [v(63.78, -4.57) * mm, v(63.22, -5.45) * mm, v(62.57, -6.24) * mm, v(61.83, -6.96) * mm]});
            skFitSpline(sketch, "E929", {"points": [v(61.83, -6.96) * mm, v(61.12, -7.68) * mm, v(60.29, -8.28) * mm, v(59.35, -8.75) * mm]});
            skFitSpline(sketch, "E930", {"points": [v(59.35, -8.75) * mm, v(58.42, -9.22) * mm, v(57.36, -9.45) * mm, v(56.16, -9.45) * mm]});
            skFitSpline(sketch, "E931", {"points": [v(56.16, -9.45) * mm, v(55.27, -9.45) * mm, v(54.51, -9.27) * mm, v(53.88, -8.9) * mm]});
            skFitSpline(sketch, "E932", {"points": [v(53.88, -8.9) * mm, v(53.26, -8.53) * mm, v(52.76, -8.04) * mm, v(52.37, -7.44) * mm]});
            skFitSpline(sketch, "E933", {"points": [v(52.37, -7.44) * mm, v(51.99, -6.82) * mm, v(51.72, -6.12) * mm, v(51.54, -5.33) * mm]});
            skFitSpline(sketch, "E934", {"points": [v(51.54, -5.33) * mm, v(51.37, -4.52) * mm, v(51.29, -3.69) * mm, v(51.29, -2.81) * mm]});
            skFitSpline(sketch, "E935", {"points": [v(51.29, -2.81) * mm, v(51.29, -2.6) * mm, v(51.29, -2.39) * mm, v(51.29, -2.18) * mm]});
            skFitSpline(sketch, "E936", {"points": [v(51.29, -2.18) * mm, v(51.29, -1.97) * mm, v(51.3, -1.74) * mm, v(51.34, -1.5) * mm]});
            skFitSpline(sketch, "E937", {"points": [v(51.34, -1.53) * mm, v(51.34, -1.48) * mm, v(51.35, -1.42) * mm, v(51.36, -1.37) * mm]});
            skFitSpline(sketch, "E938", {"points": [v(52.3, 2.75) * mm, v(52.45, 3.22) * mm, v(52.63, 3.68) * mm, v(52.83, 4.13) * mm]});
            skFitSpline(sketch, "E939", {"points": [v(52.83, 4.13) * mm, v(53.24, 5.05) * mm, v(53.7, 5.9) * mm, v(54.24, 6.7) * mm]});
            skFitSpline(sketch, "E940", {"points": [v(54.24, 6.7) * mm, v(54.77, 7.5) * mm, v(55.35, 8.2) * mm, v(55.98, 8.8) * mm]});
            skFitSpline(sketch, "E941", {"points": [v(55.98, 8.8) * mm, v(56.63, 9.4) * mm, v(57.32, 9.88) * mm, v(58.04, 10.21) * mm]});
            skFitSpline(sketch, "E942", {"points": [v(58.04, 10.21) * mm, v(58.77, 10.56) * mm, v(59.53, 10.74) * mm, v(60.32, 10.74) * mm]});
            skFitSpline(sketch, "E943", {"points": [v(60.32, 10.74) * mm, v(61.07, 10.74) * mm, v(61.74, 10.58) * mm, v(62.32, 10.26) * mm]});
            skFitSpline(sketch, "E944", {"points": [v(62.32, 10.26) * mm, v(62.92, 9.94) * mm, v(63.42, 9.52) * mm, v(63.81, 9) * mm]});
            skFitSpline(sketch, "E945", {"points": [v(63.81, 9) * mm, v(64.22, 8.5) * mm, v(64.52, 7.92) * mm, v(64.7, 7.27) * mm]});
            skFitSpline(sketch, "E946", {"points": [v(64.7, 7.27) * mm, v(64.91, 6.63) * mm, v(65, 5.98) * mm, v(64.97, 5.3) * mm]});
            skFitSpline(sketch, "E947", {"points": [v(64.97, 5.3) * mm, v(64.86, 4.37) * mm, v(64.52, 3.5) * mm, v(63.94, 2.72) * mm]});
            skFitSpline(sketch, "E948", {"points": [v(63.94, 2.72) * mm, v(63.36, 1.93) * mm, v(62.66, 1.23) * mm, v(61.83, 0.63) * mm]});
            skFitSpline(sketch, "E949", {"points": [v(61.83, 0.63) * mm, v(61.01, 0.03) * mm, v(60.12, -0.48) * mm, v(59.17, -0.88) * mm]});
            skFitSpline(sketch, "E950", {"points": [v(59.17, -0.88) * mm, v(58.22, -1.28) * mm, v(57.32, -1.57) * mm, v(56.45, -1.76) * mm]});
            skFitSpline(sketch, "E951", {"points": [v(56.45, -1.76) * mm, v(56.38, -2.04) * mm, v(56.32, -2.34) * mm, v(56.27, -2.64) * mm]});
            skFitSpline(sketch, "E952", {"points": [v(56.27, -2.64) * mm, v(56.23, -2.94) * mm, v(56.2, -3.26) * mm, v(56.16, -3.6) * mm]});
            skFitSpline(sketch, "E953", {"points": [v(56.16, -3.6) * mm, v(56.15, -3.73) * mm, v(56.14, -3.87) * mm, v(56.14, -4.02) * mm]});
            skFitSpline(sketch, "E954", {"points": [v(56.14, -4.02) * mm, v(56.14, -4.15) * mm, v(56.14, -4.29) * mm, v(56.14, -4.42) * mm]});
            skFitSpline(sketch, "E955", {"points": [v(56.14, -4.42) * mm, v(56.14, -4.8) * mm, v(56.16, -5.15) * mm, v(56.21, -5.5) * mm]});
            skFitSpline(sketch, "E956", {"points": [v(56.21, -5.5) * mm, v(56.28, -5.84) * mm, v(56.4, -6.15) * mm, v(56.55, -6.43) * mm]});
            skFitSpline(sketch, "E957", {"points": [v(56.55, -6.43) * mm, v(56.7, -6.7) * mm, v(56.92, -6.93) * mm, v(57.19, -7.11) * mm]});
            skFitSpline(sketch, "E958", {"points": [v(57.19, -7.11) * mm, v(57.46, -7.28) * mm, v(57.8, -7.38) * mm, v(58.22, -7.41) * mm]});
            skFitSpline(sketch, "E959", {"points": [v(58.22, -7.41) * mm, v(58.87, -7.4) * mm, v(59.48, -7.2) * mm, v(60.06, -6.81) * mm]});
            skFitSpline(sketch, "E960", {"points": [v(60.06, -6.81) * mm, v(60.65, -6.43) * mm, v(61.18, -5.96) * mm, v(61.68, -5.4) * mm]});
            skFitSpline(sketch, "E961", {"points": [v(61.68, -5.4) * mm, v(62.2, -4.83) * mm, v(62.66, -4.23) * mm, v(63.07, -3.6) * mm]});
            skFitSpline(sketch, "E962", {"points": [v(63.07, -3.6) * mm, v(63.5, -2.94) * mm, v(63.87, -2.34) * mm, v(64.2, -1.8) * mm]});
            skFitSpline(sketch, "E963", {"points": [v(64.2, -1.83) * mm, v(64.6, -1.13) * mm, v(64.98, -0.44) * mm, v(65.32, 0.23) * mm]});
            skFitSpline(sketch, "E964", {"points": [v(65.32, 0.23) * mm, v(65.68, 0.92) * mm, v(66, 1.54) * mm, v(66.3, 2.09) * mm]});
            skFitSpline(sketch, "E965", {"points": [v(66.3, 2.09) * mm, v(66.44, 2.34) * mm, v(66.6, 2.63) * mm, v(66.76, 2.94) * mm]});
            skFitSpline(sketch, "E966", {"points": [v(66.76, 2.94) * mm, v(66.93, 3.26) * mm, v(67.09, 3.54) * mm, v(67.22, 3.77) * mm]});
            skFitSpline(sketch, "E967", {"points": [v(67.22, 3.77) * mm, v(67.43, 3.86) * mm, v(67.56, 3.9) * mm, v(67.6, 3.9) * mm]});
            skFitSpline(sketch, "E968", {"points": [v(67.6, 3.9) * mm, v(67.76, 3.9) * mm, v(67.88, 3.85) * mm, v(67.97, 3.75) * mm]});
            skFitSpline(sketch, "E969", {"points": [v(67.97, 3.75) * mm, v(68.07, 3.66) * mm, v(68.16, 3.56) * mm, v(68.22, 3.42) * mm]});
            skFitSpline(sketch, "E970", {"points": [v(67.97, 2.87) * mm, v(67.66, 2.25) * mm, v(67.27, 1.5) * mm, v(66.81, 0.63) * mm]});
            skFitSpline(sketch, "E971", {"points": [v(66.81, 0.63) * mm, v(66.37, -0.22) * mm, v(65.87, -1.11) * mm, v(65.32, -2.03) * mm]});
            skFitSpline(sketch, "E972", {"points": [v(63.35, 7.02) * mm, v(63.1, 7.5) * mm, v(62.78, 7.75) * mm, v(62.42, 7.75) * mm]});
            skFitSpline(sketch, "E973", {"points": [v(62.42, 7.75) * mm, v(62.1, 7.75) * mm, v(61.74, 7.6) * mm, v(61.35, 7.3) * mm]});
            skFitSpline(sketch, "E974", {"points": [v(61.35, 7.3) * mm, v(60.97, 7) * mm, v(60.59, 6.6) * mm, v(60.2, 6.11) * mm]});
            skFitSpline(sketch, "E975", {"points": [v(60.2, 6.11) * mm, v(59.82, 5.63) * mm, v(59.44, 5.08) * mm, v(59.06, 4.48) * mm]});
            skFitSpline(sketch, "E976", {"points": [v(59.06, 4.48) * mm, v(58.69, 3.87) * mm, v(58.34, 3.27) * mm, v(58.04, 2.67) * mm]});
            skFitSpline(sketch, "E977", {"points": [v(58.04, 2.67) * mm, v(57.75, 2.06) * mm, v(57.48, 1.49) * mm, v(57.24, 0.93) * mm]});
            skFitSpline(sketch, "E978", {"points": [v(57.24, 0.93) * mm, v(57.02, 0.4) * mm, v(56.86, -0.05) * mm, v(56.78, -0.4) * mm]});
            skFitSpline(sketch, "E979", {"points": [v(56.78, -0.4) * mm, v(57.36, -0.33) * mm, v(58.04, -0.15) * mm, v(58.8, 0.15) * mm]});
            skFitSpline(sketch, "E980", {"points": [v(58.8, 0.15) * mm, v(59.58, 0.46) * mm, v(60.31, 0.85) * mm, v(61.01, 1.34) * mm]});
            skFitSpline(sketch, "E981", {"points": [v(61.01, 1.34) * mm, v(61.73, 1.82) * mm, v(62.35, 2.38) * mm, v(62.86, 3.02) * mm]});
            skFitSpline(sketch, "E982", {"points": [v(62.86, 3.02) * mm, v(63.37, 3.66) * mm, v(63.66, 4.35) * mm, v(63.73, 5.1) * mm]});
            skFitSpline(sketch, "E983", {"points": [v(63.73, 5.1) * mm, v(63.8, 5.73) * mm, v(63.67, 6.36) * mm, v(63.35, 7.02) * mm]});
            skFitSpline(sketch, "E984", {"points": [v(79.79, -2.84) * mm, v(79.89, -3.32) * mm, v(80.08, -3.76) * mm, v(80.35, -4.15) * mm]});
            skFitSpline(sketch, "E985", {"points": [v(80.35, -4.15) * mm, v(80.64, -4.51) * mm, v(81, -4.84) * mm, v(81.4, -5.13) * mm]});
            skFitSpline(sketch, "E986", {"points": [v(81.4, -5.13) * mm, v(81.81, -5.41) * mm, v(82.27, -5.65) * mm, v(82.76, -5.83) * mm]});
            skFitSpline(sketch, "E987", {"points": [v(82.76, -5.83) * mm, v(83.27, -6) * mm, v(83.81, -6.12) * mm, v(84.38, -6.18) * mm]});
            skFitSpline(sketch, "E988", {"points": [v(84.38, -6.18) * mm, v(85.32, -6.3) * mm, v(86.22, -6.2) * mm, v(87.07, -5.88) * mm]});
            skFitSpline(sketch, "E989", {"points": [v(87.07, -5.88) * mm, v(87.95, -5.56) * mm, v(88.72, -5.1) * mm, v(89.4, -4.47) * mm]});
            skFitSpline(sketch, "E990", {"points": [v(89.4, -4.47) * mm, v(90.1, -3.85) * mm, v(90.65, -3.1) * mm, v(91.08, -2.24) * mm]});
            skFitSpline(sketch, "E991", {"points": [v(91.08, -2.24) * mm, v(91.5, -1.35) * mm, v(91.75, -0.4) * mm, v(91.82, 0.6) * mm]});
            skFitSpline(sketch, "E992", {"points": [v(91.82, 0.6) * mm, v(91.89, 1.73) * mm, v(91.8, 2.7) * mm, v(91.54, 3.52) * mm]});
            skFitSpline(sketch, "E993", {"points": [v(91.54, 3.52) * mm, v(91.28, 4.34) * mm, v(90.88, 5) * mm, v(90.33, 5.48) * mm]});
            skFitSpline(sketch, "E994", {"points": [v(90.33, 5.48) * mm, v(89.8, 5.99) * mm, v(89.13, 6.31) * mm, v(88.33, 6.46) * mm]});
            skFitSpline(sketch, "E995", {"points": [v(88.33, 6.46) * mm, v(87.54, 6.61) * mm, v(86.64, 6.58) * mm, v(85.64, 6.36) * mm]});
            skFitSpline(sketch, "E996", {"points": [v(85.64, 6.36) * mm, v(85.34, 6.3) * mm, v(85.08, 6.27) * mm, v(84.84, 6.29) * mm]});
            skFitSpline(sketch, "E997", {"points": [v(84.84, 6.29) * mm, v(84.6, 6.3) * mm, v(84.39, 6.38) * mm, v(84.2, 6.51) * mm]});
            skFitSpline(sketch, "E998", {"points": [v(84.2, 6.51) * mm, v(84.01, 6.63) * mm, v(83.9, 6.74) * mm, v(83.87, 6.84) * mm]});
            skFitSpline(sketch, "E999", {"points": [v(83.87, 6.84) * mm, v(83.83, 6.96) * mm, v(83.83, 7.07) * mm, v(83.87, 7.17) * mm]});
            skFitSpline(sketch, "E1000", {"points": [v(83.87, 7.17) * mm, v(83.92, 7.27) * mm, v(84, 7.37) * mm, v(84.1, 7.47) * mm]});
            skFitSpline(sketch, "E1001", {"points": [v(84.1, 7.47) * mm, v(84.2, 7.57) * mm, v(84.3, 7.69) * mm, v(84.43, 7.82) * mm]});
            skFitSpline(sketch, "E1002", {"points": [v(84.43, 7.82) * mm, v(84.84, 8.3) * mm, v(85.22, 8.75) * mm, v(85.56, 9.15) * mm]});
            skFitSpline(sketch, "E1003", {"points": [v(85.56, 9.15) * mm, v(85.92, 9.57) * mm, v(86.26, 9.97) * mm, v(86.59, 10.34) * mm]});
            skFitSpline(sketch, "E1004", {"points": [v(86.59, 10.34) * mm, v(87.68, 11.6) * mm, v(88.52, 12.6) * mm, v(89.1, 13.3) * mm]});
            skFitSpline(sketch, "E1005", {"points": [v(89.1, 13.3) * mm, v(89.7, 14) * mm, v(90.13, 14.53) * mm, v(90.38, 14.86) * mm]});
            skFitSpline(sketch, "E1006", {"points": [v(90.38, 14.86) * mm, v(90.66, 15.2) * mm, v(90.8, 15.39) * mm, v(90.82, 15.44) * mm]});
            skFitSpline(sketch, "E1007", {"points": [v(90.82, 15.44) * mm, v(90.85, 15.5) * mm, v(90.86, 15.54) * mm, v(90.84, 15.54) * mm]});
            skFitSpline(sketch, "E1008", {"points": [v(90.84, 15.54) * mm, v(89.97, 15.46) * mm, v(89.08, 15.36) * mm, v(88.18, 15.26) * mm]});
            skFitSpline(sketch, "E1009", {"points": [v(88.18, 15.26) * mm, v(87.29, 15.16) * mm, v(86.37, 15.1) * mm, v(85.43, 15.06) * mm]});
            skFitSpline(sketch, "E1010", {"points": [v(85.43, 15.06) * mm, v(85.16, 15.03) * mm, v(84.8, 15) * mm, v(84.35, 14.99) * mm]});
            skFitSpline(sketch, "E1011", {"points": [v(84.35, 14.99) * mm, v(83.92, 14.97) * mm, v(83.48, 14.98) * mm, v(83.02, 15.01) * mm]});
            skFitSpline(sketch, "E1012", {"points": [v(83.02, 15.01) * mm, v(82.56, 15.06) * mm, v(82.11, 15.15) * mm, v(81.68, 15.29) * mm]});
            skFitSpline(sketch, "E1013", {"points": [v(81.68, 15.29) * mm, v(81.27, 15.44) * mm, v(80.95, 15.67) * mm, v(80.7, 15.97) * mm]});
            skFitSpline(sketch, "E1014", {"points": [v(80.7, 15.97) * mm, v(80.54, 16.27) * mm, v(80.4, 16.62) * mm, v(80.32, 17.02) * mm]});
            skFitSpline(sketch, "E1015", {"points": [v(80.32, 17.02) * mm, v(80.24, 17.43) * mm, v(80.24, 17.95) * mm, v(80.32, 18.58) * mm]});
            skFitSpline(sketch, "E1016", {"points": [v(80.32, 18.58) * mm, v(80.36, 18.78) * mm, v(80.4, 18.95) * mm, v(80.45, 19.09) * mm]});
            skFitSpline(sketch, "E1017", {"points": [v(80.45, 19.09) * mm, v(80.52, 19.22) * mm, v(80.6, 19.28) * mm, v(80.68, 19.26) * mm]});
            skFitSpline(sketch, "E1018", {"points": [v(80.68, 19.26) * mm, v(80.79, 19.23) * mm, v(80.92, 19.15) * mm, v(81.1, 19.04) * mm]});
            skFitSpline(sketch, "E1019", {"points": [v(81.1, 19.04) * mm, v(81.28, 18.92) * mm, v(81.52, 18.84) * mm, v(81.81, 18.8) * mm]});
            skFitSpline(sketch, "E1020", {"points": [v(81.81, 18.8) * mm, v(82.1, 18.74) * mm, v(82.53, 18.7) * mm, v(83.1, 18.7) * mm]});
            skFitSpline(sketch, "E1021", {"points": [v(83.1, 18.7) * mm, v(83.68, 18.73) * mm, v(84.33, 18.75) * mm, v(85.05, 18.78) * mm]});
            skFitSpline(sketch, "E1022", {"points": [v(85.05, 18.78) * mm, v(85.76, 18.83) * mm, v(86.53, 18.88) * mm, v(87.33, 18.93) * mm]});
            skFitSpline(sketch, "E1023", {"points": [v(87.33, 18.93) * mm, v(88.15, 18.99) * mm, v(88.95, 19.03) * mm, v(89.72, 19.06) * mm]});
            skFitSpline(sketch, "E1024", {"points": [v(89.72, 19.06) * mm, v(90.5, 19.11) * mm, v(91.23, 19.13) * mm, v(91.9, 19.11) * mm]});
            skFitSpline(sketch, "E1025", {"points": [v(91.9, 19.11) * mm, v(92.56, 19.11) * mm, v(93.12, 19.07) * mm, v(93.56, 18.99) * mm]});
            skFitSpline(sketch, "E1026", {"points": [v(93.56, 18.99) * mm, v(94.23, 18.85) * mm, v(94.7, 18.6) * mm, v(94.98, 18.2) * mm]});
            skFitSpline(sketch, "E1027", {"points": [v(94.98, 18.2) * mm, v(95.25, 17.82) * mm, v(95.39, 17.37) * mm, v(95.39, 16.85) * mm]});
            skFitSpline(sketch, "E1028", {"points": [v(95.39, 16.85) * mm, v(95.39, 16.04) * mm, v(95.22, 15.27) * mm, v(94.87, 14.53) * mm]});
            skFitSpline(sketch, "E1029", {"points": [v(94.87, 14.53) * mm, v(94.55, 13.8) * mm, v(94.14, 13.08) * mm, v(93.64, 12.37) * mm]});
            skFitSpline(sketch, "E1030", {"points": [v(93.64, 12.37) * mm, v(93.15, 11.69) * mm, v(92.6, 11) * mm, v(92, 10.34) * mm]});
            skFitSpline(sketch, "E1031", {"points": [v(92, 10.34) * mm, v(91.42, 9.68) * mm, v(90.87, 9.02) * mm, v(90.36, 8.35) * mm]});
            skFitSpline(sketch, "E1032", {"points": [v(90.36, 8.35) * mm, v(91.06, 8.33) * mm, v(91.74, 8.17) * mm, v(92.4, 7.85) * mm]});
            skFitSpline(sketch, "E1033", {"points": [v(92.4, 7.85) * mm, v(93.1, 7.53) * mm, v(93.7, 7.1) * mm, v(94.23, 6.59) * mm]});
            skFitSpline(sketch, "E1034", {"points": [v(94.23, 6.59) * mm, v(94.78, 6.07) * mm, v(95.23, 5.48) * mm, v(95.6, 4.8) * mm]});
            skFitSpline(sketch, "E1035", {"points": [v(95.6, 4.8) * mm, v(95.95, 4.13) * mm, v(96.16, 3.45) * mm, v(96.23, 2.74) * mm]});
            skFitSpline(sketch, "E1036", {"points": [v(96.23, 2.74) * mm, v(96.37, 1.03) * mm, v(96.2, -0.52) * mm, v(95.72, -1.9) * mm]});
            skFitSpline(sketch, "E1037", {"points": [v(95.72, -1.9) * mm, v(95.7, -1.94) * mm, v(95.7, -1.98) * mm, v(95.68, -2.01) * mm]});
            skFitSpline(sketch, "E1038", {"points": [v(93.54, -5.45) * mm, v(92.56, -6.43) * mm, v(91.34, -7.18) * mm, v(89.87, -7.72) * mm]});
            skFitSpline(sketch, "E1039", {"points": [v(89.87, -7.72) * mm, v(88.42, -8.24) * mm, v(86.77, -8.5) * mm, v(84.94, -8.5) * mm]});
            skFitSpline(sketch, "E1040", {"points": [v(84.94, -8.5) * mm, v(84.3, -8.5) * mm, v(83.57, -8.37) * mm, v(82.79, -8.12) * mm]});
            skFitSpline(sketch, "E1041", {"points": [v(82.79, -8.12) * mm, v(82.02, -7.87) * mm, v(81.3, -7.52) * mm, v(80.6, -7.06) * mm]});
            skFitSpline(sketch, "E1042", {"points": [v(80.6, -7.06) * mm, v(79.94, -6.6) * mm, v(79.38, -6.08) * mm, v(78.94, -5.48) * mm]});
            skFitSpline(sketch, "E1043", {"points": [v(78.94, -5.48) * mm, v(78.51, -4.88) * mm, v(78.33, -4.22) * mm, v(78.4, -3.52) * mm]});
            skFitSpline(sketch, "E1044", {"points": [v(78.4, -3.52) * mm, v(78.42, -3.4) * mm, v(78.44, -3.27) * mm, v(78.48, -3.14) * mm]});
            skFitSpline(sketch, "E1045", {"points": [v(78.48, -3.14) * mm, v(78.5, -3) * mm, v(78.54, -2.86) * mm, v(78.6, -2.71) * mm]});
            skFitSpline(sketch, "E1046", {"points": [v(78.6, -2.71) * mm, v(78.66, -2.63) * mm, v(78.74, -2.55) * mm, v(78.86, -2.49) * mm]});
            skFitSpline(sketch, "E1047", {"points": [v(78.86, -2.49) * mm, v(79, -2.42) * mm, v(79.14, -2.39) * mm, v(79.27, -2.39) * mm]});
            skFitSpline(sketch, "E1048", {"points": [v(79.27, -2.39) * mm, v(79.4, -2.39) * mm, v(79.52, -2.42) * mm, v(79.6, -2.49) * mm]});
            skFitSpline(sketch, "E1049", {"points": [v(79.6, -2.49) * mm, v(79.7, -2.55) * mm, v(79.76, -2.67) * mm, v(79.76, -2.84) * mm]});
            skFitSpline(sketch, "E1050", {"points": [v(115.97, 16.04) * mm, v(115.8, 14.89) * mm, v(115.59, 13.56) * mm, v(115.33, 12.07) * mm]});
            skFitSpline(sketch, "E1051", {"points": [v(115.33, 12.07) * mm, v(115.1, 10.58) * mm, v(114.83, 9.01) * mm, v(114.56, 7.37) * mm]});
            skFitSpline(sketch, "E1052", {"points": [v(114.56, 7.37) * mm, v(114.29, 5.74) * mm, v(114, 4.1) * mm, v(113.71, 2.44) * mm]});
            skFitSpline(sketch, "E1053", {"points": [v(113.71, 2.44) * mm, v(113.42, 0.8) * mm, v(113.15, -0.75) * mm, v(112.9, -2.21) * mm]});
            skFitSpline(sketch, "E1054", {"points": [v(112.9, -2.21) * mm, v(112.64, -3.65) * mm, v(112.4, -4.95) * mm, v(112.17, -6.1) * mm]});
            skFitSpline(sketch, "E1055", {"points": [v(112.17, -6.1) * mm, v(111.97, -7.26) * mm, v(111.8, -8.15) * mm, v(111.69, -8.77) * mm]});
            skFitSpline(sketch, "E1056", {"points": [v(111.69, -8.75) * mm, v(111.53, -9.18) * mm, v(111.34, -9.61) * mm, v(111.1, -10.03) * mm]});
            skFitSpline(sketch, "E1057", {"points": [v(111.1, -10.03) * mm, v(110.87, -10.47) * mm, v(110.6, -10.84) * mm, v(110.25, -11.16) * mm]});
            skFitSpline(sketch, "E1058", {"points": [v(110.25, -11.16) * mm, v(109.92, -11.5) * mm, v(109.53, -11.76) * mm, v(109.07, -11.97) * mm]});
            skFitSpline(sketch, "E1059", {"points": [v(109.07, -11.97) * mm, v(108.6, -12.17) * mm, v(108.06, -12.27) * mm, v(107.43, -12.27) * mm]});
            skFitSpline(sketch, "E1060", {"points": [v(107.43, -12.27) * mm, v(107.14, -12.27) * mm, v(106.93, -12.27) * mm, v(106.81, -12.27) * mm]});
            skFitSpline(sketch, "E1061", {"points": [v(106.81, -12.27) * mm, v(106.7, -12.27) * mm, v(106.62, -12.26) * mm, v(106.55, -12.24) * mm]});
            skFitSpline(sketch, "E1062", {"points": [v(106.58, -12.24) * mm, v(106.27, -12.12) * mm, v(106.02, -12) * mm, v(105.81, -11.84) * mm]});
            skFitSpline(sketch, "E1063", {"points": [v(105.81, -11.84) * mm, v(105.6, -11.7) * mm, v(105.57, -11.49) * mm, v(105.7, -11.19) * mm]});
            skFitSpline(sketch, "E1064", {"points": [v(105.7, -11.19) * mm, v(105.67, -11.09) * mm, v(105.68, -10.98) * mm, v(105.73, -10.88) * mm]});
            skFitSpline(sketch, "E1065", {"points": [v(105.73, -10.88) * mm, v(105.78, -10.8) * mm, v(105.83, -10.72) * mm, v(105.86, -10.66) * mm]});
            skFitSpline(sketch, "E1066", {"points": [v(105.86, -10.66) * mm, v(105.95, -10.52) * mm, v(106.05, -10.34) * mm, v(106.17, -10.1) * mm]});
            skFitSpline(sketch, "E1067", {"points": [v(106.17, -10.1) * mm, v(106.3, -9.89) * mm, v(106.44, -9.64) * mm, v(106.58, -9.35) * mm]});
            skFitSpline(sketch, "E1068", {"points": [v(106.58, -9.35) * mm, v(106.87, -8.43) * mm, v(107.14, -7.36) * mm, v(107.4, -6.13) * mm]});
            skFitSpline(sketch, "E1069", {"points": [v(107.4, -6.13) * mm, v(107.66, -4.9) * mm, v(107.89, -3.6) * mm, v(108.1, -2.26) * mm]});
            skFitSpline(sketch, "E1070", {"points": [v(108.1, -2.26) * mm, v(108.32, -0.92) * mm, v(108.52, 0.43) * mm, v(108.7, 1.79) * mm]});
            skFitSpline(sketch, "E1071", {"points": [v(108.7, 1.79) * mm, v(108.9, 3.15) * mm, v(109.07, 4.42) * mm, v(109.22, 5.6) * mm]});
            skFitSpline(sketch, "E1072", {"points": [v(109.4, 6.97) * mm, v(109.52, 7.82) * mm, v(109.63, 8.65) * mm, v(109.74, 9.46) * mm]});
            skFitSpline(sketch, "E1073", {"points": [v(109.74, 9.46) * mm, v(109.86, 10.28) * mm, v(109.97, 11.05) * mm, v(110.07, 11.77) * mm]});
            skFitSpline(sketch, "E1074", {"points": [v(110.07, 11.77) * mm, v(110.19, 12.49) * mm, v(110.3, 13.14) * mm, v(110.43, 13.73) * mm]});
            skFitSpline(sketch, "E1075", {"points": [v(110.43, 13.73) * mm, v(110.55, 14.33) * mm, v(110.68, 14.84) * mm, v(110.81, 15.24) * mm]});
            skFitSpline(sketch, "E1076", {"points": [v(110.81, 15.24) * mm, v(110.4, 15) * mm, v(109.95, 14.77) * mm, v(109.45, 14.53) * mm]});
            skFitSpline(sketch, "E1077", {"points": [v(109.45, 14.53) * mm, v(108.98, 14.32) * mm, v(108.49, 14.1) * mm, v(108, 13.9) * mm]});
            skFitSpline(sketch, "E1078", {"points": [v(108, 13.9) * mm, v(107.5, 13.72) * mm, v(107, 13.55) * mm, v(106.5, 13.4) * mm]});
            skFitSpline(sketch, "E1079", {"points": [v(106.5, 13.4) * mm, v(106, 13.27) * mm, v(105.54, 13.17) * mm, v(105.1, 13.1) * mm]});
            skFitSpline(sketch, "E1080", {"points": [v(105.1, 13.1) * mm, v(104.58, 13.05) * mm, v(104.1, 13.07) * mm, v(103.65, 13.15) * mm]});
            skFitSpline(sketch, "E1081", {"points": [v(103.65, 13.15) * mm, v(103.21, 13.24) * mm, v(102.82, 13.37) * mm, v(102.47, 13.55) * mm]});
            skFitSpline(sketch, "E1082", {"points": [v(102.47, 13.55) * mm, v(102.15, 13.76) * mm, v(101.88, 14) * mm, v(101.68, 14.3) * mm]});
            skFitSpline(sketch, "E1083", {"points": [v(101.68, 14.3) * mm, v(101.5, 14.61) * mm, v(101.4, 14.96) * mm, v(101.4, 15.36) * mm]});
            skFitSpline(sketch, "E1084", {"points": [v(101.4, 15.36) * mm, v(101.4, 15.95) * mm, v(101.69, 16.67) * mm, v(102.27, 17.53) * mm]});
            skFitSpline(sketch, "E1085", {"points": [v(102.27, 17.53) * mm, v(102.71, 18.1) * mm, v(103.27, 18.65) * mm, v(103.94, 19.19) * mm]});
            skFitSpline(sketch, "E1086", {"points": [v(103.94, 19.19) * mm, v(104.6, 19.72) * mm, v(105.29, 20.2) * mm, v(105.99, 20.64) * mm]});
            skFitSpline(sketch, "E1087", {"points": [v(105.99, 20.64) * mm, v(106.7, 21.1) * mm, v(107.37, 21.5) * mm, v(108.02, 21.83) * mm]});
            skFitSpline(sketch, "E1088", {"points": [v(108.02, 21.83) * mm, v(108.67, 22.16) * mm, v(109.21, 22.43) * mm, v(109.66, 22.63) * mm]});
            skFitSpline(sketch, "E1089", {"points": [v(109.66, 22.63) * mm, v(111.6, 23.49) * mm, v(113.45, 24.1) * mm, v(115.18, 24.5) * mm]});
            skFitSpline(sketch, "E1090", {"points": [v(115.18, 24.5) * mm, v(116.9, 24.9) * mm, v(118.49, 25.1) * mm, v(119.92, 25.1) * mm]});
            skFitSpline(sketch, "E1091", {"points": [v(119.92, 25.1) * mm, v(122.08, 25.1) * mm, v(123.94, 24.7) * mm, v(125.5, 23.91) * mm]});
            skFitSpline(sketch, "E1092", {"points": [v(125.5, 23.91) * mm, v(127.07, 23.13) * mm, v(128.37, 22.04) * mm, v(129.4, 20.67) * mm]});
            skFitSpline(sketch, "E1093", {"points": [v(129.4, 20.67) * mm, v(130.42, 19.31) * mm, v(131.18, 17.72) * mm, v(131.68, 15.9) * mm]});
            skFitSpline(sketch, "E1094", {"points": [v(131.68, 15.9) * mm, v(132.17, 14.07) * mm, v(132.42, 12.11) * mm, v(132.42, 10.03) * mm]});
            skFitSpline(sketch, "E1095", {"points": [v(132.42, 10.03) * mm, v(132.42, 9.26) * mm, v(132.37, 8.44) * mm, v(132.27, 7.57) * mm]});
            skFitSpline(sketch, "E1096", {"points": [v(132.27, 7.57) * mm, v(132.18, 6.7) * mm, v(132.06, 5.81) * mm, v(131.9, 4.9) * mm]});
            skFitSpline(sketch, "E1097", {"points": [v(131.9, 4.9) * mm, v(131.75, 4) * mm, v(131.56, 3.1) * mm, v(131.34, 2.22) * mm]});
            skFitSpline(sketch, "E1098", {"points": [v(131.34, 2.22) * mm, v(131.14, 1.33) * mm, v(130.91, 0.49) * mm, v(130.68, -0.3) * mm]});
            skFitSpline(sketch, "E1099", {"points": [v(130.68, -0.3) * mm, v(129.96, -2.24) * mm, v(129, -4.2) * mm, v(127.83, -6.16) * mm]});
            skFitSpline(sketch, "E1100", {"points": [v(127.83, -6.16) * mm, v(126.65, -8.12) * mm, v(125.29, -9.96) * mm, v(123.75, -11.69) * mm]});
            skFitSpline(sketch, "E1101", {"points": [v(123.75, -11.69) * mm, v(122.22, -13.42) * mm, v(120.55, -14.96) * mm, v(118.72, -16.31) * mm]});
            skFitSpline(sketch, "E1102", {"points": [v(118.72, -16.31) * mm, v(116.9, -17.69) * mm, v(115, -18.75) * mm, v(113, -19.5) * mm]});
            skFitSpline(sketch, "E1103", {"points": [v(113, -19.5) * mm, v(111.87, -19.84) * mm, v(110.69, -20.12) * mm, v(109.45, -20.34) * mm]});
            skFitSpline(sketch, "E1104", {"points": [v(109.45, -20.34) * mm, v(108.22, -20.56) * mm, v(107.04, -20.66) * mm, v(105.91, -20.66) * mm]});
            skFitSpline(sketch, "E1105", {"points": [v(105.91, -20.66) * mm, v(104.4, -20.66) * mm, v(102.94, -20.45) * mm, v(101.5, -20.04) * mm]});
            skFitSpline(sketch, "E1106", {"points": [v(101.5, -20.04) * mm, v(100.06, -19.63) * mm, v(98.75, -19.03) * mm, v(97.57, -18.23) * mm]});
            skFitSpline(sketch, "E1107", {"points": [v(97.57, -18.23) * mm, v(96.24, -17.19) * mm, v(95.15, -15.9) * mm, v(94.31, -14.38) * mm]});
            skFitSpline(sketch, "E1108", {"points": [v(94.31, -14.38) * mm, v(93.46, -12.87) * mm, v(93.03, -11.2) * mm, v(93.03, -9.35) * mm]});
            skFitSpline(sketch, "E1109", {"points": [v(93.03, -9.35) * mm, v(93.03, -8.75) * mm, v(93.1, -8.1) * mm, v(93.21, -7.39) * mm]});
            skFitSpline(sketch, "E1110", {"points": [v(93.21, -7.39) * mm, v(93.33, -6.67) * mm, v(93.48, -5.97) * mm, v(93.67, -5.3) * mm]});
            skFitSpline(sketch, "E1111", {"points": [v(95.68, -2.01) * mm, v(96.37, -1.2) * mm, v(97.1, -0.5) * mm, v(97.9, 0.1) * mm]});
            skFitSpline(sketch, "E1112", {"points": [v(97.9, 0.1) * mm, v(98.83, 0.8) * mm, v(99.77, 1.36) * mm, v(100.73, 1.76) * mm]});
            skFitSpline(sketch, "E1113", {"points": [v(100.73, 1.76) * mm, v(101.7, 2.18) * mm, v(102.62, 2.4) * mm, v(103.48, 2.4) * mm]});
            skFitSpline(sketch, "E1114", {"points": [v(103.48, 2.4) * mm, v(104.02, 2.4) * mm, v(104.53, 2.3) * mm, v(104.99, 2.14) * mm]});
            skFitSpline(sketch, "E1115", {"points": [v(104.99, 2.14) * mm, v(105.45, 1.99) * mm, v(105.85, 1.74) * mm, v(106.2, 1.39) * mm]});
            skFitSpline(sketch, "E1116", {"points": [v(106.2, 1.39) * mm, v(106.54, 1.03) * mm, v(106.8, 0.59) * mm, v(107, 0.05) * mm]});
            skFitSpline(sketch, "E1117", {"points": [v(107, 0.05) * mm, v(107.2, -0.48) * mm, v(107.3, -1.13) * mm, v(107.3, -1.88) * mm]});
            skFitSpline(sketch, "E1118", {"points": [v(107.3, -1.88) * mm, v(107.3, -2.57) * mm, v(107.24, -3.2) * mm, v(107.12, -3.77) * mm]});
            skFitSpline(sketch, "E1119", {"points": [v(107.12, -3.74) * mm, v(106.93, -4.06) * mm, v(106.73, -4.22) * mm, v(106.53, -4.22) * mm]});
            skFitSpline(sketch, "E1120", {"points": [v(106.53, -4.22) * mm, v(106.32, -4.2) * mm, v(106.15, -4.13) * mm, v(106.02, -4) * mm]});
            skFitSpline(sketch, "E1121", {"points": [v(106.02, -4) * mm, v(106.03, -3.81) * mm, v(106.04, -3.63) * mm, v(106.04, -3.47) * mm]});
            skFitSpline(sketch, "E1122", {"points": [v(106.04, -3.47) * mm, v(106.06, -3.3) * mm, v(106.07, -3.14) * mm, v(106.07, -2.99) * mm]});
            skFitSpline(sketch, "E1123", {"points": [v(106.07, -2.99) * mm, v(106.07, -1.77) * mm, v(105.86, -0.89) * mm, v(105.45, -0.35) * mm]});
            skFitSpline(sketch, "E1124", {"points": [v(105.45, -0.35) * mm, v(105.04, 0.2) * mm, v(104.51, 0.48) * mm, v(103.86, 0.48) * mm]});
            skFitSpline(sketch, "E1125", {"points": [v(103.86, 0.48) * mm, v(103.31, 0.48) * mm, v(102.71, 0.31) * mm, v(102.06, -0.02) * mm]});
            skFitSpline(sketch, "E1126", {"points": [v(102.06, -0.02) * mm, v(101.43, -0.36) * mm, v(100.82, -0.81) * mm, v(100.22, -1.38) * mm]});
            skFitSpline(sketch, "E1127", {"points": [v(100.22, -1.38) * mm, v(99.62, -1.95) * mm, v(99.06, -2.61) * mm, v(98.55, -3.37) * mm]});
            skFitSpline(sketch, "E1128", {"points": [v(98.55, -3.37) * mm, v(98.05, -4.12) * mm, v(97.67, -4.92) * mm, v(97.4, -5.76) * mm]});
            skFitSpline(sketch, "E1129", {"points": [v(97.4, -5.76) * mm, v(97.15, -6.56) * mm, v(96.97, -7.35) * mm, v(96.83, -8.12) * mm]});
            skFitSpline(sketch, "E1130", {"points": [v(96.83, -8.12) * mm, v(96.7, -8.89) * mm, v(96.62, -9.6) * mm, v(96.62, -10.26) * mm]});
            skFitSpline(sketch, "E1131", {"points": [v(96.62, -10.26) * mm, v(96.62, -11.61) * mm, v(96.84, -12.85) * mm, v(97.27, -13.98) * mm]});
            skFitSpline(sketch, "E1132", {"points": [v(97.27, -13.98) * mm, v(97.71, -15.12) * mm, v(98.37, -16.09) * mm, v(99.24, -16.9) * mm]});
            skFitSpline(sketch, "E1133", {"points": [v(99.24, -16.9) * mm, v(100.01, -17.65) * mm, v(100.9, -18.18) * mm, v(101.9, -18.5) * mm]});
            skFitSpline(sketch, "E1134", {"points": [v(101.9, -18.5) * mm, v(102.94, -18.84) * mm, v(104.01, -19) * mm, v(105.14, -19) * mm]});
            skFitSpline(sketch, "E1135", {"points": [v(105.14, -19) * mm, v(106.27, -19) * mm, v(107.4, -18.85) * mm, v(108.53, -18.53) * mm]});
            skFitSpline(sketch, "E1136", {"points": [v(108.53, -18.53) * mm, v(109.66, -18.23) * mm, v(110.71, -17.8) * mm, v(111.69, -17.27) * mm]});
            skFitSpline(sketch, "E1137", {"points": [v(111.69, -17.27) * mm, v(112.94, -16.53) * mm, v(114.15, -15.54) * mm, v(115.33, -14.28) * mm]});
            skFitSpline(sketch, "E1138", {"points": [v(115.33, -14.28) * mm, v(116.53, -13.04) * mm, v(117.64, -11.64) * mm, v(118.67, -10.08) * mm]});
            skFitSpline(sketch, "E1139", {"points": [v(118.67, -10.08) * mm, v(119.7, -8.52) * mm, v(120.62, -6.86) * mm, v(121.46, -5.1) * mm]});
            skFitSpline(sketch, "E1140", {"points": [v(121.46, -5.1) * mm, v(122.32, -3.34) * mm, v(123.04, -1.56) * mm, v(123.62, 0.23) * mm]});
            skFitSpline(sketch, "E1141", {"points": [v(123.62, 0.23) * mm, v(123.9, 1.13) * mm, v(124.14, 2.06) * mm, v(124.36, 3) * mm]});
            skFitSpline(sketch, "E1142", {"points": [v(124.36, 3) * mm, v(124.6, 3.93) * mm, v(124.8, 4.87) * mm, v(124.98, 5.81) * mm]});
            skFitSpline(sketch, "E1143", {"points": [v(124.98, 5.81) * mm, v(125.15, 6.75) * mm, v(125.28, 7.67) * mm, v(125.36, 8.58) * mm]});
            skFitSpline(sketch, "E1144", {"points": [v(125.36, 8.58) * mm, v(125.45, 9.48) * mm, v(125.5, 10.34) * mm, v(125.5, 11.17) * mm]});
            skFitSpline(sketch, "E1145", {"points": [v(125.5, 11.17) * mm, v(125.5, 12.77) * mm, v(125.33, 14.27) * mm, v(125, 15.64) * mm]});
            skFitSpline(sketch, "E1146", {"points": [v(125, 15.64) * mm, v(124.7, 17.03) * mm, v(124.2, 18.23) * mm, v(123.54, 19.24) * mm]});
            skFitSpline(sketch, "E1147", {"points": [v(123.54, 19.24) * mm, v(122.87, 20.26) * mm, v(122.01, 21.06) * mm, v(120.95, 21.62) * mm]});
            skFitSpline(sketch, "E1148", {"points": [v(120.95, 21.62) * mm, v(119.9, 22.21) * mm, v(118.65, 22.5) * mm, v(117.18, 22.5) * mm]});
            skFitSpline(sketch, "E1149", {"points": [v(117.18, 22.5) * mm, v(116.25, 22.5) * mm, v(115.2, 22.36) * mm, v(114.02, 22.08) * mm]});
            skFitSpline(sketch, "E1150", {"points": [v(114.02, 22.08) * mm, v(112.86, 21.8) * mm, v(111.62, 21.4) * mm, v(110.3, 20.85) * mm]});
            skFitSpline(sketch, "E1151", {"points": [v(110.3, 20.85) * mm, v(108.92, 20.28) * mm, v(107.68, 19.66) * mm, v(106.6, 18.99) * mm]});
            skFitSpline(sketch, "E1152", {"points": [v(106.6, 18.99) * mm, v(105.53, 18.33) * mm, v(104.73, 17.73) * mm, v(104.22, 17.17) * mm]});
            skFitSpline(sketch, "E1153", {"points": [v(104.22, 17.17) * mm, v(103.62, 16.5) * mm, v(103.32, 15.94) * mm, v(103.32, 15.5) * mm]});
            skFitSpline(sketch, "E1154", {"points": [v(103.32, 15.5) * mm, v(103.32, 15.24) * mm, v(103.45, 15.05) * mm, v(103.7, 14.94) * mm]});
            skFitSpline(sketch, "E1155", {"points": [v(103.7, 14.94) * mm, v(103.98, 14.82) * mm, v(104.37, 14.82) * mm, v(104.89, 14.94) * mm]});
            skFitSpline(sketch, "E1156", {"points": [v(104.89, 14.94) * mm, v(105.23, 15.04) * mm, v(105.6, 15.17) * mm, v(105.99, 15.34) * mm]});
            skFitSpline(sketch, "E1157", {"points": [v(105.99, 15.34) * mm, v(106.4, 15.52) * mm, v(106.82, 15.72) * mm, v(107.25, 15.92) * mm]});
            skFitSpline(sketch, "E1158", {"points": [v(107.25, 15.92) * mm, v(107.67, 16.14) * mm, v(108.1, 16.35) * mm, v(108.5, 16.57) * mm]});
            skFitSpline(sketch, "E1159", {"points": [v(108.5, 16.57) * mm, v(108.92, 16.8) * mm, v(109.3, 17.03) * mm, v(109.69, 17.25) * mm]});
            skFitSpline(sketch, "E1160", {"points": [v(110.74, 17.85) * mm, v(111.11, 18.05) * mm, v(111.45, 18.23) * mm, v(111.74, 18.38) * mm]});
            skFitSpline(sketch, "E1161", {"points": [v(111.74, 18.38) * mm, v(112.05, 18.55) * mm, v(112.3, 18.67) * mm, v(112.48, 18.73) * mm]});
            skFitSpline(sketch, "E1162", {"points": [v(112.48, 18.73) * mm, v(112.84, 18.87) * mm, v(113.18, 18.97) * mm, v(113.5, 19.04) * mm]});
            skFitSpline(sketch, "E1163", {"points": [v(113.5, 19.04) * mm, v(113.83, 19.12) * mm, v(114.1, 19.16) * mm, v(114.33, 19.16) * mm]});
            skFitSpline(sketch, "E1164", {"points": [v(114.33, 19.16) * mm, v(114.7, 19.16) * mm, v(115, 19.09) * mm, v(115.23, 18.93) * mm]});
            skFitSpline(sketch, "E1165", {"points": [v(115.23, 18.93) * mm, v(115.45, 18.78) * mm, v(115.62, 18.57) * mm, v(115.74, 18.28) * mm]});
            skFitSpline(sketch, "E1166", {"points": [v(115.74, 18.28) * mm, v(115.86, 18.01) * mm, v(115.93, 17.69) * mm, v(115.95, 17.3) * mm]});
            skFitSpline(sketch, "E1167", {"points": [v(115.95, 17.3) * mm, v(115.98, 16.93) * mm, v(115.99, 16.52) * mm, v(115.97, 16.07) * mm]});
            skSolve(sketch);
        }
        {
            var Q0;
            Q0=qSketchRegion(id+"F0",true);
            extrude(context, id + "F1", {"entities" : qUnion([Q0]), "depth" : 5 * mm});
        }
    });
